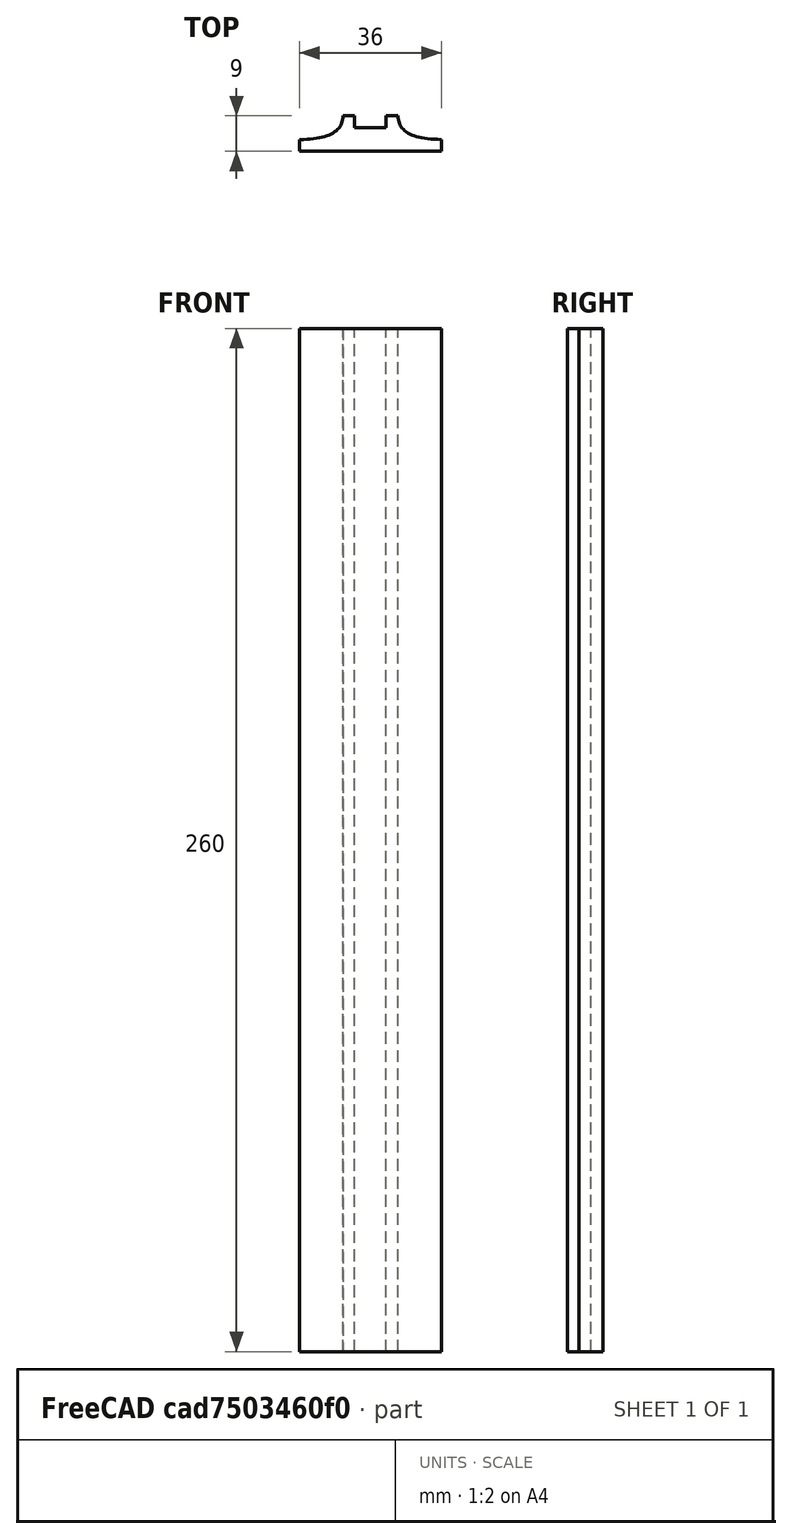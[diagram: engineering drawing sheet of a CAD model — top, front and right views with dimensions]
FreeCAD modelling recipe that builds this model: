
FCSTD DOCUMENT  (FreeCAD 0.19R0.19.2)
Label: laptopStand303.FCStd
License: All rights reserved
LicenseURL: http://en.wikipedia.org/wiki/All_rights_reserved
objects: Sketcher::SketchObject×12, Part::Extrusion×1
note: 13 computed .brp shape members not serialized (recipe doc carries the construction recipe); baked Part::Feature solids carry a one-line shape summary decoded from their .brp

FEATURE [Sketcher::SketchObject] Sketch001  label="legTop"
  FullyConstrained = true
  MapMode = 4
  Placement = pos=(0,0,0) rot=(0.57735,0.57735,0.57735;2.0944rad)
  sketch-geometry (41):
    g0: BSplineCurve PolesCount=3 KnotsCount=2 Degree=2 IsPeriodic=0
    g1: ArcOfCircle CenterX=73.1223 CenterY=-32.291 CenterZ=0 NormalX=0 NormalY=0 NormalZ=1 AngleXU=0 Radius=13 StartAngle=5.92268 EndAngle=9.06428
    g2: ArcOfCircle CenterX=66.7816 CenterY=-49.1439 CenterZ=0 NormalX=0 NormalY=0 NormalZ=1 AngleXU=0 Radius=13 StartAngle=2.78068 EndAngle=5.92131
    g3-g6: Circle x4 (B-spline internal-alignment scaffolding for g7; pole/knot coordinates omitted)
    g7: BSplineCurve PolesCount=4 KnotsCount=2 Degree=3 IsPeriodic=0
    g8: GeomPoint X=28.8094 Y=-19.0875 Z=0
    g9: GeomPoint X=47.0443 Y=-50.4712 Z=0
    g10: Circle CenterX=53.5586 CenterY=-23.2695 CenterZ=0 NormalX=0 NormalY=0 NormalZ=1 AngleXU=0 Radius=3.24518
    g11: LineSegment StartX=17.2232 StartY=-16.0875 StartZ=0 EndX=17.2232 EndY=-19.0875 EndZ=0
    g12: ArcOfCircle CenterX=17.2475 CenterY=-181.166 CenterZ=0 NormalX=0 NormalY=0 NormalZ=1 AngleXU=0 Radius=13 StartAngle=5.92268 EndAngle=7.49361
    g13: ArcOfCircle CenterX=29.5716 CenterY=-148.408 CenterZ=0 NormalX=0 NormalY=0 NormalZ=1 AngleXU=0 Radius=13 StartAngle=4.35228 EndAngle=5.92131
    g14: ArcOfCircle CenterX=35.8967 CenterY=-131.555 CenterZ=0 NormalX=0 NormalY=0 NormalZ=1 AngleXU=0 Radius=13 StartAngle=5.92268 EndAngle=7.49902
    g15: ArcOfCircle CenterX=48.1805 CenterY=-98.7782 CenterZ=0 NormalX=0 NormalY=0 NormalZ=1 AngleXU=0 Radius=13 StartAngle=4.34921 EndAngle=5.92131
    g16: ArcOfCircle CenterX=54.5183 CenterY=-81.9247 CenterZ=0 NormalX=0 NormalY=0 NormalZ=1 AngleXU=0 Radius=13 StartAngle=5.92268 EndAngle=8.70432
    g17: ArcOfCircle CenterX=20.184 CenterY=-217.506 CenterZ=0 NormalX=0 NormalY=0 NormalZ=1 AngleXU=0 Radius=3.81084 StartAngle=1.88136 EndAngle=6.80465
    g18: ArcOfCircle CenterX=36.3663 CenterY=-113.042 CenterZ=0 NormalX=0 NormalY=0 NormalZ=1 AngleXU=0 Radius=3.60555 StartAngle=0.230024 EndAngle=5.3372
    g19: ArcOfCircle CenterX=17.7945 CenterY=-162.686 CenterZ=0 NormalX=0 NormalY=0 NormalZ=1 AngleXU=0 Radius=3.60555 StartAngle=0.230024 EndAngle=5.3372
    g20: ArcOfCircle CenterX=49.8795 CenterY=-62.6074 CenterZ=0 NormalX=0 NormalY=0 NormalZ=1 AngleXU=0 Radius=3.84187 StartAngle=4.46973 EndAngle=9.40343
    g21: LineSegment StartX=48.9563 StartY=-66.3367 StartZ=0 EndX=44.7488 EndY=-73.3482 EndZ=0
    g22: LineSegment StartX=41.085 StartY=-66.3176 StartZ=0 EndX=46.0385 EndY=-62.5254 EndZ=0
    g23: LineSegment StartX=47.0443 StartY=-50.4712 StartZ=0 EndX=41.085 EndY=-66.3176 EndZ=0
    g24: LineSegment StartX=17.2232 StartY=-16.0875 StartZ=0 EndX=117.223 EndY=-16.0875 EndZ=0
    g25: LineSegment StartX=28.8094 StartY=-19.0875 StartZ=0 EndX=17.2232 EndY=-19.0875 EndZ=0
    g26: LineSegment StartX=117.223 StartY=-16.0875 StartZ=0 EndX=117.223 EndY=-19.0875 EndZ=0
    g27: LineSegment StartX=85.2866 StartY=-36.8766 StartZ=0 EndX=78.9396 EndY=-53.7463 EndZ=0
    g28: LineSegment StartX=60.9579 StartY=-27.7053 StartZ=0 EndX=54.6191 EndY=-44.5532 EndZ=0
    g29: LineSegment StartX=23.4884 StartY=-215.608 StartZ=0 EndX=94.6579 EndY=-26.1359 EndZ=0
    g30: LineSegment StartX=19.0195 StartY=-213.878 StartZ=0 EndX=29.4118 EndY=-185.752 EndZ=0
    g31: LineSegment StartX=22.7134 StartY=-166.661 StartZ=0 EndX=21.8316 EndY=-169.001 EndZ=0
    g32: LineSegment StartX=19.9036 StartY=-165.61 StartZ=0 EndX=22.7134 EndY=-166.661 EndZ=0
    g33: LineSegment StartX=21.3051 StartY=-161.864 StartZ=0 EndX=24.1149 EndY=-162.915 EndZ=0
    g34: LineSegment StartX=24.1149 StartY=-162.915 StartZ=0 EndX=24.9906 EndY=-160.574 EndZ=0
    g35: LineSegment StartX=41.7296 StartY=-153.01 StartZ=0 EndX=48.061 EndY=-136.14 EndZ=0
    g36: LineSegment StartX=41.2852 StartY=-117.017 StartZ=0 EndX=40.4148 EndY=-119.365 EndZ=0
    g37: LineSegment StartX=38.4753 StartY=-115.966 StartZ=0 EndX=41.2852 EndY=-117.017 EndZ=0
    g38: LineSegment StartX=39.8769 StartY=-112.22 StartZ=0 EndX=42.6867 EndY=-113.271 EndZ=0
    g39: LineSegment StartX=42.6867 StartY=-113.271 StartZ=0 EndX=43.5622 EndY=-110.93 EndZ=0
    g40: LineSegment StartX=66.6827 StartY=-86.5104 StartZ=0 EndX=60.3386 EndY=-103.381 EndZ=0
  constraints (65):
    c: Block(g0)
    c: Block(g1)
    c: Block(g2)
    c: Weight(g3) = 1
    c: Equal(g3,g4)
    c: Equal(g3,g5)
    c: Equal(g3,g6)
    c: InternalAlignment(g3-g6 -> g7) x4
    c: InternalAlignment(g8,g7)
    c: InternalAlignment(g9,g7)
    c: Block(g10)
    c: Block(g7)
    c: Vertical(g11)
    c: Block(g12)
    c: Block(g13)
    c: Block(g14)
    c: Block(g15)
    c: Block(g16)
    c: Block(g17)
    c: Block(g18)
    c: Block(g19)
    c: Block(g20)
    c: Coincident(g21,g20)
    c: Coincident(g21,g16)
    c: Coincident(g22,g20)
    c: Block(g22)
    c: Coincident(g23,g7)
    c: Coincident(g23,g22)
    c: Coincident(g24,g11)
    c: Horizontal(g24)
    c: Coincident(g25,g7)
    c: Coincident(g25,g11)
    c: Horizontal(g25)
    c: Coincident(g26,g24)
    c: Coincident(g26,g0)
    c: Vertical(g26)
    c: Block(g24)
    c: Coincident(g27,g1)
    c: Coincident(g27,g2)
    c: Coincident(g28,g1)
    c: Coincident(g28,g2)
    c: Coincident(g29,g17)
    c: Coincident(g29,g0)
    c: Coincident(g30,g17)
    c: Coincident(g30,g12)
    c: Coincident(g31,g12)
    c: Coincident(g32,g19)
    c: Coincident(g32,g31)
    c: Block(g31)
    c: Coincident(g33,g19)
    c: Coincident(g34,g33)
    c: Coincident(g34,g13)
    c: Block(g34)
    c: Coincident(g35,g13)
    c: Coincident(g35,g14)
    c: Coincident(g36,g14)
    c: Coincident(g37,g18)
    c: Coincident(g37,g36)
    c: Block(g36)
    c: Coincident(g38,g18)
    c: Coincident(g39,g38)
    c: Coincident(g39,g15)
    c: Block(g39)
    c: Coincident(g40,g16)
    c: Coincident(g40,g15)
FEATURE [Sketcher::SketchObject] Sketch002
  FullyConstrained = true
  sketch-geometry (20):
    g0: LineSegment StartX=-2.77179 StartY=-200.304 StartZ=0 EndX=5.22821 EndY=-200.304 EndZ=0
    g1: LineSegment StartX=5.22821 StartY=-200.304 StartZ=0 EndX=5.22821 EndY=-197.304 EndZ=0
    g2: LineSegment StartX=-2.77179 StartY=-200.304 StartZ=0 EndX=-2.77179 EndY=-197.304 EndZ=0
    g3: LineSegment StartX=5.22821 StartY=-197.304 StartZ=0 EndX=8.22821 EndY=-197.304 EndZ=0
    g4: LineSegment StartX=-2.77179 StartY=-197.304 StartZ=0 EndX=-5.77179 EndY=-197.304 EndZ=0
    g5: LineSegment StartX=19.2282 StartY=-203.304 StartZ=0 EndX=19.2282 EndY=-206.304 EndZ=0
    g6: LineSegment StartX=-16.7718 StartY=-203.304 StartZ=0 EndX=-16.7718 EndY=-206.304 EndZ=0
    g7: LineSegment StartX=-16.7718 StartY=-206.304 StartZ=0 EndX=19.2282 EndY=-206.304 EndZ=0
    g8: Circle CenterX=-16.7718 CenterY=-203.304 CenterZ=0 NormalX=0 NormalY=0 NormalZ=1 AngleXU=0 Radius=1
    g9: Circle CenterX=-5.77179 CenterY=-203.304 CenterZ=0 NormalX=0 NormalY=0 NormalZ=1 AngleXU=0 Radius=1
    g10: Circle CenterX=-5.77179 CenterY=-197.304 CenterZ=0 NormalX=0 NormalY=0 NormalZ=1 AngleXU=0 Radius=1
    g11: BSplineCurve PolesCount=3 KnotsCount=2 Degree=2 IsPeriodic=0
    g12: GeomPoint X=-16.7718 Y=-203.304 Z=0
    g13: GeomPoint X=-5.77179 Y=-197.304 Z=0
    g14: Circle CenterX=19.2282 CenterY=-203.304 CenterZ=0 NormalX=0 NormalY=0 NormalZ=1 AngleXU=0 Radius=1
    g15: Circle CenterX=8.22821 CenterY=-203.304 CenterZ=0 NormalX=0 NormalY=0 NormalZ=1 AngleXU=0 Radius=1
    g16: Circle CenterX=8.22821 CenterY=-197.304 CenterZ=0 NormalX=0 NormalY=0 NormalZ=1 AngleXU=0 Radius=1
    g17: BSplineCurve PolesCount=3 KnotsCount=2 Degree=2 IsPeriodic=0
    g18: GeomPoint X=19.2282 Y=-203.304 Z=0
    g19: GeomPoint X=8.22821 Y=-197.304 Z=0
  constraints (41):
    c: Horizontal(g0)
    c: Distance(g0) = 8
    c: Coincident(g1,g0)
    c: Vertical(g1)
    c: Distance(g1) = 3
    c: Coincident(g2,g0)
    c: Vertical(g2)
    c: Distance(g2) = 3
    c: Coincident(g3,g1)
    c: Horizontal(g3)
    c: Distance(g3) = 3
    c: Coincident(g4,g2)
    c: Horizontal(g4)
    c: Distance(g4) = 3
    c: Vertical(g5)
    c: Vertical(g6)
    c: Coincident(g7,g6)
    c: Coincident(g7,g5)
    c: Weight(g8) = 1
    c: Equal(g8,g9)
    c: Equal(g8,g10)
    c: Coincident(g11,g4)
    c: InternalAlignment(g8,g11)
    c: InternalAlignment(g9,g11)
    c: InternalAlignment(g10,g11)
    c: InternalAlignment(g12,g11)
    c: InternalAlignment(g13,g11)
    c: Coincident(g17,g5)
    c: Weight(g14) = 1
    c: Equal(g14,g15)
    c: Equal(g14,g16)
    c: Coincident(g17,g3)
    c: InternalAlignment(g14,g17)
    c: InternalAlignment(g15,g17)
    c: InternalAlignment(g16,g17)
    c: InternalAlignment(g18,g17)
    c: InternalAlignment(g19,g17)
    c: Block(g7)
    c: Block(g17)
    c: Block(g11)
    c: Block(g6)
FEATURE [Part::Extrusion] Extrude003
  Base = -> Sketch002
  Dir = (0,0,1)
  DirMode = 2
  FaceMakerClass = Part::FaceMakerBullseye
  LengthFwd = 260
  LengthRev = 0
  Solid = true
  Symmetric = false
FEATURE [Sketcher::SketchObject] Sketch003  label="original"
  FullyConstrained = false
  sketch-geometry (469):
    g0: LineSegment StartX=-42.9272 StartY=136.221 StartZ=0 EndX=-42.9272 EndY=-103.779 EndZ=0
    g1: LineSegment StartX=407.073 StartY=136.221 StartZ=0 EndX=407.073 EndY=-103.779 EndZ=0
    g2: ArcOfCircle CenterX=-26.9272 CenterY=-83.7794 CenterZ=0 NormalX=0 NormalY=0 NormalZ=1 AngleXU=0 Radius=8 StartAngle=3.14159 EndAngle=6.28319
    g3: ArcOfCircle CenterX=391.073 CenterY=-83.7794 CenterZ=0 NormalX=0 NormalY=0 NormalZ=1 AngleXU=0 Radius=8 StartAngle=3.14159 EndAngle=6.28319
    g4: Circle CenterX=175.022 CenterY=27.0628 CenterZ=0 NormalX=0 NormalY=0 NormalZ=1 AngleXU=0 Radius=1
    g5: Circle CenterX=179.022 CenterY=24.8665 CenterZ=0 NormalX=0 NormalY=0 NormalZ=1 AngleXU=0 Radius=1
    g6: Circle CenterX=179.022 CenterY=27.0628 CenterZ=0 NormalX=0 NormalY=0 NormalZ=1 AngleXU=0 Radius=1
    g7: BSplineCurve PolesCount=3 KnotsCount=2 Degree=2 IsPeriodic=0
    g8: GeomPoint X=175.022 Y=27.0628 Z=0
    g9: GeomPoint X=179.022 Y=27.0628 Z=0
    g10: Circle CenterX=189.124 CenterY=27.0628 CenterZ=0 NormalX=0 NormalY=0 NormalZ=1 AngleXU=0 Radius=1
    g11: Circle CenterX=185.124 CenterY=24.8665 CenterZ=0 NormalX=0 NormalY=0 NormalZ=1 AngleXU=0 Radius=1
    g12: Circle CenterX=185.124 CenterY=27.0628 CenterZ=0 NormalX=0 NormalY=0 NormalZ=1 AngleXU=0 Radius=1
    g13: BSplineCurve PolesCount=3 KnotsCount=2 Degree=2 IsPeriodic=0
    g14: GeomPoint X=189.124 Y=27.0628 Z=0
    g15: GeomPoint X=185.124 Y=27.0628 Z=0
    g16: Circle CenterX=175.022 CenterY=5.37834 CenterZ=0 NormalX=0 NormalY=0 NormalZ=1 AngleXU=0 Radius=1
    g17: Circle CenterX=179.022 CenterY=7.57463 CenterZ=0 NormalX=0 NormalY=0 NormalZ=1 AngleXU=0 Radius=1
    g18: Circle CenterX=179.022 CenterY=5.34704 CenterZ=0 NormalX=0 NormalY=0 NormalZ=1 AngleXU=0 Radius=1
    g19: BSplineCurve PolesCount=3 KnotsCount=2 Degree=2 IsPeriodic=0
    g20: GeomPoint X=175.022 Y=5.37834 Z=0
    g21: GeomPoint X=179.022 Y=5.34704 Z=0
    g22: Circle CenterX=189.124 CenterY=5.37834 CenterZ=0 NormalX=0 NormalY=0 NormalZ=1 AngleXU=0 Radius=1
    g23: Circle CenterX=185.124 CenterY=7.57463 CenterZ=0 NormalX=0 NormalY=0 NormalZ=1 AngleXU=0 Radius=1
    g24: Circle CenterX=185.124 CenterY=5.34704 CenterZ=0 NormalX=0 NormalY=0 NormalZ=1 AngleXU=0 Radius=1
    g25: BSplineCurve PolesCount=3 KnotsCount=2 Degree=2 IsPeriodic=0
    g26: GeomPoint X=189.124 Y=5.37834 Z=0
    g27: GeomPoint X=185.124 Y=5.34704 Z=0
    g28: Circle CenterX=165.871 CenterY=18.1458 CenterZ=0 NormalX=0 NormalY=0 NormalZ=1 AngleXU=0 Radius=1
    g29: Circle CenterX=169.377 CenterY=16.2206 CenterZ=0 NormalX=0 NormalY=0 NormalZ=1 AngleXU=0 Radius=1
    g30: Circle CenterX=165.871 CenterY=14.2956 CenterZ=0 NormalX=0 NormalY=0 NormalZ=1 AngleXU=0 Radius=1
    g31: BSplineCurve PolesCount=3 KnotsCount=2 Degree=2 IsPeriodic=0
    g32: GeomPoint X=165.871 Y=18.1458 Z=0
    g33: GeomPoint X=165.871 Y=14.2956 Z=0
    g34: Circle CenterX=198.275 CenterY=18.1318 CenterZ=0 NormalX=0 NormalY=0 NormalZ=1 AngleXU=0 Radius=1
    g35: Circle CenterX=194.768 CenterY=16.2206 CenterZ=0 NormalX=0 NormalY=0 NormalZ=1 AngleXU=0 Radius=1
    g36: Circle CenterX=198.264 CenterY=14.2963 CenterZ=0 NormalX=0 NormalY=0 NormalZ=1 AngleXU=0 Radius=1
    g37: BSplineCurve PolesCount=3 KnotsCount=2 Degree=2 IsPeriodic=0
    g38: GeomPoint X=198.275 Y=18.1318 Z=0
    g39: GeomPoint X=198.264 Y=14.2963 Z=0
    g40: LineSegment StartX=407.073 StartY=-103.779 StartZ=0 EndX=-42.9272 EndY=-103.779 EndZ=0
    g41: Circle CenterX=125.607 CenterY=54.1951 CenterZ=0 NormalX=0 NormalY=0 NormalZ=1 AngleXU=0 Radius=1
    g42: Circle CenterX=139.632 CenterY=46.4944 CenterZ=0 NormalX=0 NormalY=0 NormalZ=1 AngleXU=0 Radius=1
    g43: Circle CenterX=127.326 CenterY=56.7187 CenterZ=0 NormalX=0 NormalY=0 NormalZ=1 AngleXU=0 Radius=1
    g44: BSplineCurve PolesCount=3 KnotsCount=2 Degree=2 IsPeriodic=0
    g45: GeomPoint X=125.607 Y=54.1951 Z=0
    g46: GeomPoint X=127.326 Y=56.7187 Z=0
    g47: Circle CenterX=236.824 CenterY=56.7187 CenterZ=0 NormalX=0 NormalY=0 NormalZ=1 AngleXU=0 Radius=1
    g48: Circle CenterX=224.513 CenterY=46.4944 CenterZ=0 NormalX=0 NormalY=0 NormalZ=1 AngleXU=0 Radius=1
    g49: Circle CenterX=238.538 CenterY=54.1951 CenterZ=0 NormalX=0 NormalY=0 NormalZ=1 AngleXU=0 Radius=1
    g50: BSplineCurve PolesCount=3 KnotsCount=2 Degree=2 IsPeriodic=0
    g51: GeomPoint X=236.824 Y=56.7187 Z=0
    g52: GeomPoint X=238.538 Y=54.1951 Z=0
    g53: Circle CenterX=238.538 CenterY=-21.7516 CenterZ=0 NormalX=0 NormalY=0 NormalZ=1 AngleXU=0 Radius=1
    g54: Circle CenterX=224.513 CenterY=-14.0532 CenterZ=0 NormalX=0 NormalY=0 NormalZ=1 AngleXU=0 Radius=1
    g55: Circle CenterX=236.584 CenterY=-24.2775 CenterZ=0 NormalX=0 NormalY=0 NormalZ=1 AngleXU=0 Radius=1
    g56: BSplineCurve PolesCount=3 KnotsCount=2 Degree=2 IsPeriodic=0
    g57: GeomPoint X=238.538 Y=-21.7516 Z=0
    g58: GeomPoint X=236.584 Y=-24.2775 Z=0
    g59: Circle CenterX=125.607 CenterY=-21.7539 CenterZ=0 NormalX=0 NormalY=0 NormalZ=1 AngleXU=0 Radius=1
    g60: Circle CenterX=139.632 CenterY=-14.0532 CenterZ=0 NormalX=0 NormalY=0 NormalZ=1 AngleXU=0 Radius=1
    g61: Circle CenterX=127.325 CenterY=-24.2775 CenterZ=0 NormalX=0 NormalY=0 NormalZ=1 AngleXU=0 Radius=1
    g62: BSplineCurve PolesCount=3 KnotsCount=2 Degree=2 IsPeriodic=0
    g63: GeomPoint X=125.607 Y=-21.7539 Z=0
    g64: GeomPoint X=127.325 Y=-24.2775 Z=0
    g65: Circle CenterX=302.996 CenterY=111.695 CenterZ=0 NormalX=0 NormalY=0 NormalZ=1 AngleXU=0 Radius=1
    g66: Circle CenterX=306.073 CenterY=114.251 CenterZ=0 NormalX=0 NormalY=0 NormalZ=1 AngleXU=0 Radius=1
    g67: Circle CenterX=306.073 CenterY=110.251 CenterZ=0 NormalX=0 NormalY=0 NormalZ=1 AngleXU=0 Radius=1
    g68: BSplineCurve PolesCount=3 KnotsCount=2 Degree=2 IsPeriodic=0
    g69: GeomPoint X=302.996 Y=111.695 Z=0
    g70: GeomPoint X=306.073 Y=110.251 Z=0
    g71: Circle CenterX=306.073 CenterY=95.2763 CenterZ=0 NormalX=0 NormalY=0 NormalZ=1 AngleXU=0 Radius=1
    g72: Circle CenterX=306.073 CenterY=91.2763 CenterZ=0 NormalX=0 NormalY=0 NormalZ=1 AngleXU=0 Radius=1
    g73: Circle CenterX=302.567 CenterY=89.3511 CenterZ=0 NormalX=0 NormalY=0 NormalZ=1 AngleXU=0 Radius=1
    g74: BSplineCurve PolesCount=3 KnotsCount=2 Degree=2 IsPeriodic=0
    g75: GeomPoint X=306.073 Y=95.2763 Z=0
    g76: GeomPoint X=302.567 Y=89.3511 Z=0
    g77: LineSegment StartX=306.073 StartY=110.251 StartZ=0 EndX=306.073 EndY=95.2763 EndZ=0
    g78: LineSegment StartX=302.996 StartY=111.695 StartZ=0 EndX=236.824 EndY=56.7187 EndZ=0
    g79: LineSegment StartX=238.538 StartY=54.1951 StartZ=0 EndX=302.567 EndY=89.3511 EndZ=0
    g80: Circle CenterX=61.1496 CenterY=111.695 CenterZ=0 NormalX=0 NormalY=0 NormalZ=1 AngleXU=0 Radius=1
    g81: Circle CenterX=58.0728 CenterY=114.251 CenterZ=0 NormalX=0 NormalY=0 NormalZ=1 AngleXU=0 Radius=1
    g82: Circle CenterX=58.0728 CenterY=110.251 CenterZ=0 NormalX=0 NormalY=0 NormalZ=1 AngleXU=0 Radius=1
    g83: BSplineCurve PolesCount=3 KnotsCount=2 Degree=2 IsPeriodic=0
    g84: GeomPoint X=61.1496 Y=111.695 Z=0
    g85: GeomPoint X=58.0728 Y=110.251 Z=0
    g86: Circle CenterX=61.5791 CenterY=89.3511 CenterZ=0 NormalX=0 NormalY=0 NormalZ=1 AngleXU=0 Radius=1
    g87: Circle CenterX=58.0728 CenterY=91.2763 CenterZ=0 NormalX=0 NormalY=0 NormalZ=1 AngleXU=0 Radius=1
    g88: Circle CenterX=58.0728 CenterY=95.2763 CenterZ=0 NormalX=0 NormalY=0 NormalZ=1 AngleXU=0 Radius=1
    g89: BSplineCurve PolesCount=3 KnotsCount=2 Degree=2 IsPeriodic=0
    g90: GeomPoint X=61.5791 Y=89.3511 Z=0
    g91: GeomPoint X=58.0728 Y=95.2763 Z=0
    g92: LineSegment StartX=58.0728 StartY=110.251 StartZ=0 EndX=58.0728 EndY=95.2763 EndZ=0
    g93: LineSegment StartX=61.1496 StartY=111.695 StartZ=0 EndX=127.326 EndY=56.7187 EndZ=0
    g94: LineSegment StartX=125.607 StartY=54.1951 StartZ=0 EndX=61.5791 EndY=89.3511 EndZ=0
    g95: Circle CenterX=61.5791 CenterY=-56.9099 CenterZ=0 NormalX=0 NormalY=0 NormalZ=1 AngleXU=0 Radius=1
    g96: Circle CenterX=58.0728 CenterY=-58.8351 CenterZ=0 NormalX=0 NormalY=0 NormalZ=1 AngleXU=0 Radius=1
    g97: Circle CenterX=58.0728 CenterY=-62.8351 CenterZ=0 NormalX=0 NormalY=0 NormalZ=1 AngleXU=0 Radius=1
    g98: BSplineCurve PolesCount=3 KnotsCount=2 Degree=2 IsPeriodic=0
    g99: GeomPoint X=61.5791 Y=-56.9099 Z=0
    g100: GeomPoint X=58.0728 Y=-62.8351 Z=0
    g101: Circle CenterX=58.0728 CenterY=-77.8102 CenterZ=0 NormalX=0 NormalY=0 NormalZ=1 AngleXU=0 Radius=1
    g102: Circle CenterX=58.0728 CenterY=-81.8102 CenterZ=0 NormalX=0 NormalY=0 NormalZ=1 AngleXU=0 Radius=1
    g103: Circle CenterX=61.1496 CenterY=-79.2541 CenterZ=0 NormalX=0 NormalY=0 NormalZ=1 AngleXU=0 Radius=1
    g104: BSplineCurve PolesCount=3 KnotsCount=2 Degree=2 IsPeriodic=0
    g105: GeomPoint X=58.0728 Y=-77.8102 Z=0
    g106: GeomPoint X=61.1496 Y=-79.2541 Z=0
    g107: LineSegment StartX=58.0728 StartY=-62.8351 StartZ=0 EndX=58.0728 EndY=-77.8102 EndZ=0
    g108: LineSegment StartX=61.1496 StartY=-79.2541 StartZ=0 EndX=127.325 EndY=-24.2775 EndZ=0
    g109: LineSegment StartX=125.607 StartY=-21.7539 StartZ=0 EndX=61.5791 EndY=-56.9099 EndZ=0
    g110: Circle CenterX=302.567 CenterY=-56.9099 CenterZ=0 NormalX=0 NormalY=0 NormalZ=1 AngleXU=0 Radius=1
    g111: Circle CenterX=306.073 CenterY=-58.8351 CenterZ=0 NormalX=0 NormalY=0 NormalZ=1 AngleXU=0 Radius=1
    g112: Circle CenterX=306.073 CenterY=-62.8351 CenterZ=0 NormalX=0 NormalY=0 NormalZ=1 AngleXU=0 Radius=1
    g113: BSplineCurve PolesCount=3 KnotsCount=2 Degree=2 IsPeriodic=0
    g114: GeomPoint X=302.567 Y=-56.9099 Z=0
    g115: GeomPoint X=306.073 Y=-62.8351 Z=0
    g116: Circle CenterX=302.996 CenterY=-79.2541 CenterZ=0 NormalX=0 NormalY=0 NormalZ=1 AngleXU=0 Radius=1
    g117: Circle CenterX=306.073 CenterY=-81.8102 CenterZ=0 NormalX=0 NormalY=0 NormalZ=1 AngleXU=0 Radius=1
    g118: Circle CenterX=306.073 CenterY=-77.8102 CenterZ=0 NormalX=0 NormalY=0 NormalZ=1 AngleXU=0 Radius=1
    g119: BSplineCurve PolesCount=3 KnotsCount=2 Degree=2 IsPeriodic=0
    g120: GeomPoint X=302.996 Y=-79.2541 Z=0
    g121: GeomPoint X=306.073 Y=-77.8102 Z=0
    g122: LineSegment StartX=306.073 StartY=-62.8351 StartZ=0 EndX=306.073 EndY=-77.8102 EndZ=0
    g123: LineSegment StartX=302.996 StartY=-79.2541 StartZ=0 EndX=236.584 EndY=-24.2775 EndZ=0
    g124: LineSegment StartX=238.538 StartY=-21.7516 StartZ=0 EndX=302.567 EndY=-56.9099 EndZ=0
    g125: Circle CenterX=61.6457 CenterY=-88.8112 CenterZ=0 NormalX=0 NormalY=0 NormalZ=1 AngleXU=0 Radius=1
    g126: Circle CenterX=58.0728 CenterY=-91.7794 CenterZ=0 NormalX=0 NormalY=0 NormalZ=1 AngleXU=0 Radius=1
    g127: Circle CenterX=63.9135 CenterY=-91.7791 CenterZ=0 NormalX=0 NormalY=0 NormalZ=1 AngleXU=0 Radius=1
    g128: BSplineCurve PolesCount=3 KnotsCount=2 Degree=2 IsPeriodic=0
    g129: GeomPoint X=61.6457 Y=-88.8112 Z=0
    g130: GeomPoint X=63.9135 Y=-91.7791 Z=0
    g131: Circle CenterX=179.022 CenterY=-85.8163 CenterZ=0 NormalX=0 NormalY=0 NormalZ=1 AngleXU=0 Radius=1
    g132: Circle CenterX=179.022 CenterY=-91.7794 CenterZ=0 NormalX=0 NormalY=0 NormalZ=1 AngleXU=0 Radius=1
    g133: Circle CenterX=171.895 CenterY=-91.7791 CenterZ=0 NormalX=0 NormalY=0 NormalZ=1 AngleXU=0 Radius=1
    g134: BSplineCurve PolesCount=3 KnotsCount=2 Degree=2 IsPeriodic=0
    g135: GeomPoint X=179.022 Y=-85.8163 Z=0
    g136: GeomPoint X=171.895 Y=-91.7791 Z=0
    g137: Circle CenterX=185.124 CenterY=-86.2028 CenterZ=0 NormalX=0 NormalY=0 NormalZ=1 AngleXU=0 Radius=1
    g138: Circle CenterX=185.124 CenterY=-91.7794 CenterZ=0 NormalX=0 NormalY=0 NormalZ=1 AngleXU=0 Radius=1
    g139: Circle CenterX=191.747 CenterY=-91.7794 CenterZ=0 NormalX=0 NormalY=0 NormalZ=1 AngleXU=0 Radius=1
    g140: BSplineCurve PolesCount=3 KnotsCount=2 Degree=2 IsPeriodic=0
    g141: GeomPoint X=185.124 Y=-86.2028 Z=0
    g142: GeomPoint X=191.747 Y=-91.7794 Z=0
    g143: Circle CenterX=299.888 CenterY=-86.6413 CenterZ=0 NormalX=0 NormalY=0 NormalZ=1 AngleXU=0 Radius=1
    g144: Circle CenterX=306.073 CenterY=-91.7794 CenterZ=0 NormalX=0 NormalY=0 NormalZ=1 AngleXU=0 Radius=1
    g145: Circle CenterX=298.776 CenterY=-91.7794 CenterZ=0 NormalX=0 NormalY=0 NormalZ=1 AngleXU=0 Radius=1
    g146: BSplineCurve PolesCount=3 KnotsCount=2 Degree=2 IsPeriodic=0
    g147: GeomPoint X=299.888 Y=-86.6413 Z=0
    g148: GeomPoint X=298.776 Y=-91.7794 Z=0
    g149: LineSegment StartX=189.124 StartY=5.37834 StartZ=0 EndX=299.888 EndY=-86.6413 EndZ=0
    g150: LineSegment StartX=298.776 StartY=-91.7794 StartZ=0 EndX=191.747 EndY=-91.7794 EndZ=0
    g151: LineSegment StartX=185.124 StartY=-86.2028 StartZ=0 EndX=185.124 EndY=5.34704 EndZ=0
    g152: LineSegment StartX=179.022 StartY=5.34704 StartZ=0 EndX=179.022 EndY=-85.8163 EndZ=0
    g153: LineSegment StartX=171.895 StartY=-91.7791 StartZ=0 EndX=63.9135 EndY=-91.7791 EndZ=0
    g154: LineSegment StartX=61.6457 StartY=-88.8112 StartZ=0 EndX=175.022 EndY=5.37834 EndZ=0
    g155: Circle CenterX=302.073 CenterY=124.221 CenterZ=0 NormalX=0 NormalY=0 NormalZ=1 AngleXU=0 Radius=1
    g156: Circle CenterX=306.073 CenterY=124.221 CenterZ=0 NormalX=0 NormalY=0 NormalZ=1 AngleXU=0 Radius=1
    g157: Circle CenterX=302.996 CenterY=121.665 CenterZ=0 NormalX=0 NormalY=0 NormalZ=1 AngleXU=0 Radius=1
    g158: BSplineCurve PolesCount=3 KnotsCount=2 Degree=2 IsPeriodic=0
    g159: GeomPoint X=302.073 Y=124.221 Z=0
    g160: GeomPoint X=302.996 Y=121.665 Z=0
    g161: Circle CenterX=189.124 CenterY=124.221 CenterZ=0 NormalX=0 NormalY=0 NormalZ=1 AngleXU=0 Radius=1
    g162: Circle CenterX=185.124 CenterY=124.221 CenterZ=0 NormalX=0 NormalY=0 NormalZ=1 AngleXU=0 Radius=1
    g163: Circle CenterX=185.124 CenterY=120.221 CenterZ=0 NormalX=0 NormalY=0 NormalZ=1 AngleXU=0 Radius=1
    g164: BSplineCurve PolesCount=3 KnotsCount=2 Degree=2 IsPeriodic=0
    g165: GeomPoint X=189.124 Y=124.221 Z=0
    g166: GeomPoint X=185.124 Y=120.221 Z=0
    g167: Circle CenterX=175.022 CenterY=124.221 CenterZ=0 NormalX=0 NormalY=0 NormalZ=1 AngleXU=0 Radius=1
    g168: Circle CenterX=179.022 CenterY=124.221 CenterZ=0 NormalX=0 NormalY=0 NormalZ=1 AngleXU=0 Radius=1
    g169: Circle CenterX=179.022 CenterY=120.221 CenterZ=0 NormalX=0 NormalY=0 NormalZ=1 AngleXU=0 Radius=1
    g170: BSplineCurve PolesCount=3 KnotsCount=2 Degree=2 IsPeriodic=0
    g171: GeomPoint X=175.022 Y=124.221 Z=0
    g172: GeomPoint X=179.022 Y=120.221 Z=0
    g173: Circle CenterX=62.0728 CenterY=124.221 CenterZ=0 NormalX=0 NormalY=0 NormalZ=1 AngleXU=0 Radius=1
    g174: Circle CenterX=58.0728 CenterY=124.221 CenterZ=0 NormalX=0 NormalY=0 NormalZ=1 AngleXU=0 Radius=1
    g175: Circle CenterX=61.1496 CenterY=121.665 CenterZ=0 NormalX=0 NormalY=0 NormalZ=1 AngleXU=0 Radius=1
    g176: BSplineCurve PolesCount=3 KnotsCount=2 Degree=2 IsPeriodic=0
    g177: GeomPoint X=62.0728 Y=124.221 Z=0
    g178: GeomPoint X=61.1496 Y=121.665 Z=0
    g179: LineSegment StartX=179.022 StartY=120.221 StartZ=0 EndX=179.022 EndY=27.0628 EndZ=0
    g180: LineSegment StartX=185.124 StartY=27.0628 StartZ=0 EndX=185.124 EndY=120.221 EndZ=0
    g181: LineSegment StartX=302.996 StartY=121.665 StartZ=0 EndX=189.124 EndY=27.0628 EndZ=0
    g182: LineSegment StartX=175.022 StartY=27.0628 StartZ=0 EndX=61.1496 EndY=121.665 EndZ=0
    g183: Circle CenterX=61.5791 CenterY=75.4095 CenterZ=0 NormalX=0 NormalY=0 NormalZ=1 AngleXU=0 Radius=1
    g184: Circle CenterX=58.0728 CenterY=77.3346 CenterZ=0 NormalX=0 NormalY=0 NormalZ=1 AngleXU=0 Radius=1
    g185: Circle CenterX=58.0728 CenterY=73.3346 CenterZ=0 NormalX=0 NormalY=0 NormalZ=1 AngleXU=0 Radius=1
    g186: BSplineCurve PolesCount=3 KnotsCount=2 Degree=2 IsPeriodic=0
    g187: GeomPoint X=61.5791 Y=75.4095 Z=0
    g188: GeomPoint X=58.0728 Y=73.3346 Z=0
    g189: Circle CenterX=58.0728 CenterY=-40.8935 CenterZ=0 NormalX=0 NormalY=0 NormalZ=1 AngleXU=0 Radius=1
    g190: Circle CenterX=58.0728 CenterY=-44.8935 CenterZ=0 NormalX=0 NormalY=0 NormalZ=1 AngleXU=0 Radius=1
    g191: Circle CenterX=61.5791 CenterY=-42.9683 CenterZ=0 NormalX=0 NormalY=0 NormalZ=1 AngleXU=0 Radius=1
    g192: BSplineCurve PolesCount=3 KnotsCount=2 Degree=2 IsPeriodic=0
    g193: GeomPoint X=58.0728 Y=-40.8935 Z=0
    g194: GeomPoint X=61.5791 Y=-42.9683 Z=0
    g195: LineSegment StartX=61.5791 StartY=-42.9683 StartZ=0 EndX=165.871 EndY=14.2956 EndZ=0
    g196: LineSegment StartX=165.871 StartY=18.1458 StartZ=0 EndX=61.5791 EndY=75.4095 EndZ=0
    g197: LineSegment StartX=58.0728 StartY=73.3346 StartZ=0 EndX=58.0728 EndY=-40.8935 EndZ=0
    g198: Circle CenterX=302.567 CenterY=-42.9683 CenterZ=0 NormalX=0 NormalY=0 NormalZ=1 AngleXU=0 Radius=1
    g199: Circle CenterX=306.073 CenterY=-44.8935 CenterZ=0 NormalX=0 NormalY=0 NormalZ=1 AngleXU=0 Radius=1
    g200: Circle CenterX=306.073 CenterY=-40.8935 CenterZ=0 NormalX=0 NormalY=0 NormalZ=1 AngleXU=0 Radius=1
    g201: BSplineCurve PolesCount=3 KnotsCount=2 Degree=2 IsPeriodic=0
    g202: GeomPoint X=302.567 Y=-42.9683 Z=0
    g203: GeomPoint X=306.073 Y=-40.8935 Z=0
    g204: Circle CenterX=306.073 CenterY=73.3346 CenterZ=0 NormalX=0 NormalY=0 NormalZ=1 AngleXU=0 Radius=1
    g205: Circle CenterX=306.073 CenterY=77.3346 CenterZ=0 NormalX=0 NormalY=0 NormalZ=1 AngleXU=0 Radius=1
    g206: Circle CenterX=302.535 CenterY=75.4095 CenterZ=0 NormalX=0 NormalY=0 NormalZ=1 AngleXU=0 Radius=1
    g207: BSplineCurve PolesCount=3 KnotsCount=2 Degree=2 IsPeriodic=0
    g208: GeomPoint X=306.073 Y=73.3346 Z=0
    g209: GeomPoint X=302.535 Y=75.4095 Z=0
    g210: LineSegment StartX=302.567 StartY=-42.9683 StartZ=0 EndX=198.264 EndY=14.2963 EndZ=0
    g211: LineSegment StartX=198.275 StartY=18.1318 StartZ=0 EndX=302.535 EndY=75.4095 EndZ=0
    g212: LineSegment StartX=306.073 StartY=73.3346 StartZ=0 EndX=306.073 EndY=-40.8935 EndZ=0
    g213: LineSegment StartX=322.073 StartY=105.865 StartZ=0 EndX=328.643 EndY=105.865 EndZ=0
    g214: LineSegment StartX=318.073 StartY=120.221 StartZ=0 EndX=318.073 EndY=109.865 EndZ=0
    g215: LineSegment StartX=336.157 StartY=107.779 StartZ=0 EndX=362.567 EndY=122.294 EndZ=0
    g216: Circle CenterX=362.073 CenterY=124.221 CenterZ=0 NormalX=0 NormalY=0 NormalZ=1 AngleXU=0 Radius=1
    g217: Circle CenterX=366.073 CenterY=124.221 CenterZ=0 NormalX=0 NormalY=0 NormalZ=1 AngleXU=0 Radius=1
    g218: Circle CenterX=362.567 CenterY=122.294 CenterZ=0 NormalX=0 NormalY=0 NormalZ=1 AngleXU=0 Radius=1
    g219: BSplineCurve PolesCount=3 KnotsCount=2 Degree=2 IsPeriodic=0
    g220: GeomPoint X=362.073 Y=124.221 Z=0
    g221: GeomPoint X=362.567 Y=122.294 Z=0
    g222: Circle CenterX=322.073 CenterY=124.221 CenterZ=0 NormalX=0 NormalY=0 NormalZ=1 AngleXU=0 Radius=1
    g223: Circle CenterX=318.073 CenterY=124.221 CenterZ=0 NormalX=0 NormalY=0 NormalZ=1 AngleXU=0 Radius=1
    g224: Circle CenterX=318.073 CenterY=120.221 CenterZ=0 NormalX=0 NormalY=0 NormalZ=1 AngleXU=0 Radius=1
    g225: BSplineCurve PolesCount=3 KnotsCount=2 Degree=2 IsPeriodic=0
    g226: GeomPoint X=322.073 Y=124.221 Z=0
    g227: GeomPoint X=318.073 Y=120.221 Z=0
    g228: Circle CenterX=322.073 CenterY=105.865 CenterZ=0 NormalX=0 NormalY=0 NormalZ=1 AngleXU=0 Radius=1
    g229: Circle CenterX=318.073 CenterY=105.865 CenterZ=0 NormalX=0 NormalY=0 NormalZ=1 AngleXU=0 Radius=1
    g230: Circle CenterX=318.073 CenterY=109.865 CenterZ=0 NormalX=0 NormalY=0 NormalZ=1 AngleXU=0 Radius=1
    g231: BSplineCurve PolesCount=3 KnotsCount=2 Degree=2 IsPeriodic=0
    g232: GeomPoint X=322.073 Y=105.865 Z=0
    g233: GeomPoint X=318.073 Y=109.865 Z=0
    g234: Circle CenterX=336.157 CenterY=107.779 CenterZ=0 NormalX=0 NormalY=0 NormalZ=1 AngleXU=0 Radius=1
    g235: Circle CenterX=332.651 CenterY=105.853 CenterZ=0 NormalX=0 NormalY=0 NormalZ=1 AngleXU=0 Radius=1
    g236: Circle CenterX=328.643 CenterY=105.865 CenterZ=0 NormalX=0 NormalY=0 NormalZ=1 AngleXU=0 Radius=1
    g237: BSplineCurve PolesCount=3 KnotsCount=2 Degree=2 IsPeriodic=0
    g238: GeomPoint X=336.157 Y=107.779 Z=0
    g239: GeomPoint X=328.643 Y=105.865 Z=0
    g240: LineSegment StartX=322.073 StartY=124.221 StartZ=0 EndX=362.073 EndY=124.221 EndZ=0
    g241: Circle CenterX=371.567 CenterY=-80.8644 CenterZ=0 NormalX=0 NormalY=0 NormalZ=1 AngleXU=0 Radius=1
    g242: Circle CenterX=375.073 CenterY=-82.7896 CenterZ=0 NormalX=0 NormalY=0 NormalZ=1 AngleXU=0 Radius=1
    g243: Circle CenterX=375.073 CenterY=-78.7896 CenterZ=0 NormalX=0 NormalY=0 NormalZ=1 AngleXU=0 Radius=1
    g244: BSplineCurve PolesCount=3 KnotsCount=2 Degree=2 IsPeriodic=0
    g245: GeomPoint X=371.567 Y=-80.8644 Z=0
    g246: GeomPoint X=375.073 Y=-78.7896 Z=0
    g247: Circle CenterX=321.579 CenterY=-53.4075 CenterZ=0 NormalX=0 NormalY=0 NormalZ=1 AngleXU=0 Radius=1
    g248: Circle CenterX=318.073 CenterY=-51.4823 CenterZ=0 NormalX=0 NormalY=0 NormalZ=1 AngleXU=0 Radius=1
    g249: Circle CenterX=318.073 CenterY=-47.4805 CenterZ=0 NormalX=0 NormalY=0 NormalZ=1 AngleXU=0 Radius=1
    g250: BSplineCurve PolesCount=3 KnotsCount=2 Degree=2 IsPeriodic=0
    g251: GeomPoint X=321.579 Y=-53.4075 Z=0
    g252: GeomPoint X=318.073 Y=-47.4805 Z=0
    g253: LineSegment StartX=371.567 StartY=-80.8644 StartZ=0 EndX=321.579 EndY=-53.4075 EndZ=0
    g254: Circle CenterX=321.579 CenterY=-67.3492 CenterZ=0 NormalX=0 NormalY=0 NormalZ=1 AngleXU=0 Radius=1
    g255: Circle CenterX=318.073 CenterY=-65.424 CenterZ=0 NormalX=0 NormalY=0 NormalZ=1 AngleXU=0 Radius=1
    g256: Circle CenterX=318.073 CenterY=-69.424 CenterZ=0 NormalX=0 NormalY=0 NormalZ=1 AngleXU=0 Radius=1
    g257: BSplineCurve PolesCount=3 KnotsCount=2 Degree=2 IsPeriodic=0
    g258: GeomPoint X=321.579 Y=-67.3492 Z=0
    g259: GeomPoint X=318.073 Y=-69.424 Z=0
    g260: Circle CenterX=362.567 CenterY=-89.8542 CenterZ=0 NormalX=0 NormalY=0 NormalZ=1 AngleXU=0 Radius=1
    g261: Circle CenterX=366.073 CenterY=-91.7794 CenterZ=0 NormalX=0 NormalY=0 NormalZ=1 AngleXU=0 Radius=1
    g262: Circle CenterX=362.073 CenterY=-91.7794 CenterZ=0 NormalX=0 NormalY=0 NormalZ=1 AngleXU=0 Radius=1
    g263: BSplineCurve PolesCount=3 KnotsCount=2 Degree=2 IsPeriodic=0
    g264: GeomPoint X=362.567 Y=-89.8542 Z=0
    g265: GeomPoint X=362.073 Y=-91.7794 Z=0
    g266: Circle CenterX=322.073 CenterY=-91.7794 CenterZ=0 NormalX=0 NormalY=0 NormalZ=1 AngleXU=0 Radius=1
    g267: Circle CenterX=318.073 CenterY=-91.7794 CenterZ=0 NormalX=0 NormalY=0 NormalZ=1 AngleXU=0 Radius=1
    g268: Circle CenterX=318.073 CenterY=-87.7794 CenterZ=0 NormalX=0 NormalY=0 NormalZ=1 AngleXU=0 Radius=1
    g269: BSplineCurve PolesCount=3 KnotsCount=2 Degree=2 IsPeriodic=0
    g270: GeomPoint X=322.073 Y=-91.7794 Z=0
    g271: GeomPoint X=318.073 Y=-87.7794 Z=0
    g272: LineSegment StartX=362.567 StartY=-89.8542 StartZ=0 EndX=321.579 EndY=-67.3492 EndZ=0
    g273: LineSegment StartX=318.073 StartY=-69.424 StartZ=0 EndX=318.073 EndY=-87.7794 EndZ=0
    g274: LineSegment StartX=322.073 StartY=-91.7794 StartZ=0 EndX=362.073 EndY=-91.7794 EndZ=0
    g275: Circle CenterX=2.07281 CenterY=124.221 CenterZ=0 NormalX=0 NormalY=0 NormalZ=1 AngleXU=0 Radius=1
    g276: Circle CenterX=1.57905 CenterY=122.295 CenterZ=0 NormalX=0 NormalY=0 NormalZ=1 AngleXU=0 Radius=1
    g277: BSplineCurve PolesCount=3 KnotsCount=2 Degree=2 IsPeriodic=0
    g278: GeomPoint X=2.07281 Y=124.221 Z=0
    g279: GeomPoint X=1.57905 Y=122.295 Z=0
    g280: Circle CenterX=42.0728 CenterY=124.221 CenterZ=0 NormalX=0 NormalY=0 NormalZ=1 AngleXU=0 Radius=1
    g281: Circle CenterX=46.0728 CenterY=124.221 CenterZ=0 NormalX=0 NormalY=0 NormalZ=1 AngleXU=0 Radius=1
    g282: Circle CenterX=46.0728 CenterY=120.221 CenterZ=0 NormalX=0 NormalY=0 NormalZ=1 AngleXU=0 Radius=1
    g283: BSplineCurve PolesCount=3 KnotsCount=2 Degree=2 IsPeriodic=0
    g284: GeomPoint X=42.0728 Y=124.221 Z=0
    g285: GeomPoint X=46.0728 Y=120.221 Z=0
    g286: Circle CenterX=46.0728 CenterY=109.865 CenterZ=0 NormalX=0 NormalY=0 NormalZ=1 AngleXU=0 Radius=1
    g287: Circle CenterX=46.0728 CenterY=105.865 CenterZ=0 NormalX=0 NormalY=0 NormalZ=1 AngleXU=0 Radius=1
    g288: Circle CenterX=42.0728 CenterY=105.865 CenterZ=0 NormalX=0 NormalY=0 NormalZ=1 AngleXU=0 Radius=1
    g289: BSplineCurve PolesCount=3 KnotsCount=2 Degree=2 IsPeriodic=0
    g290: GeomPoint X=46.0728 Y=109.865 Z=0
    g291: GeomPoint X=42.0728 Y=105.865 Z=0
    g292: Circle CenterX=35.5028 CenterY=105.865 CenterZ=0 NormalX=0 NormalY=0 NormalZ=1 AngleXU=0 Radius=1
    g293: Circle CenterX=31.5028 CenterY=105.865 CenterZ=0 NormalX=0 NormalY=0 NormalZ=1 AngleXU=0 Radius=1
    g294: Circle CenterX=27.9965 CenterY=107.79 CenterZ=0 NormalX=0 NormalY=0 NormalZ=1 AngleXU=0 Radius=1
    g295: BSplineCurve PolesCount=3 KnotsCount=2 Degree=2 IsPeriodic=0
    g296: GeomPoint X=35.5028 Y=105.865 Z=0
    g297: GeomPoint X=27.9965 Y=107.79 Z=0
    g298: LineSegment StartX=2.07281 StartY=124.221 StartZ=0 EndX=42.0728 EndY=124.221 EndZ=0
    g299: LineSegment StartX=46.0728 StartY=120.221 StartZ=0 EndX=46.0728 EndY=109.865 EndZ=0
    g300: LineSegment StartX=42.0728 StartY=105.865 StartZ=0 EndX=35.5028 EndY=105.865 EndZ=0
    g301: LineSegment StartX=27.9965 StartY=107.79 StartZ=0 EndX=1.57905 EndY=122.295 EndZ=0
    g302: Circle CenterX=42.5666 CenterY=-67.3492 CenterZ=0 NormalX=0 NormalY=0 NormalZ=1 AngleXU=0 Radius=1
    g303: Circle CenterX=46.0728 CenterY=-65.424 CenterZ=0 NormalX=0 NormalY=0 NormalZ=1 AngleXU=0 Radius=1
    g304: Circle CenterX=46.0728 CenterY=-69.424 CenterZ=0 NormalX=0 NormalY=0 NormalZ=1 AngleXU=0 Radius=1
    g305: BSplineCurve PolesCount=3 KnotsCount=2 Degree=2 IsPeriodic=0
    g306: GeomPoint X=42.5666 Y=-67.3492 Z=0
    g307: GeomPoint X=46.0728 Y=-69.424 Z=0
    g308: Circle CenterX=46.0728 CenterY=-87.7794 CenterZ=0 NormalX=0 NormalY=0 NormalZ=1 AngleXU=0 Radius=1
    g309: Circle CenterX=46.0728 CenterY=-91.7794 CenterZ=0 NormalX=0 NormalY=0 NormalZ=1 AngleXU=0 Radius=1
    g310: Circle CenterX=42.0728 CenterY=-91.7794 CenterZ=0 NormalX=0 NormalY=0 NormalZ=1 AngleXU=0 Radius=1
    g311: BSplineCurve PolesCount=3 KnotsCount=2 Degree=2 IsPeriodic=0
    g312: GeomPoint X=46.0728 Y=-87.7794 Z=0
    g313: GeomPoint X=42.0728 Y=-91.7794 Z=0
    g314: Circle CenterX=2.07281 CenterY=-91.7794 CenterZ=0 NormalX=0 NormalY=0 NormalZ=1 AngleXU=0 Radius=1
    g315: Circle CenterX=-1.92719 CenterY=-91.7794 CenterZ=0 NormalX=0 NormalY=0 NormalZ=1 AngleXU=0 Radius=1
    g316: Circle CenterX=1.57905 CenterY=-89.8542 CenterZ=0 NormalX=0 NormalY=0 NormalZ=1 AngleXU=0 Radius=1
    g317: BSplineCurve PolesCount=3 KnotsCount=2 Degree=2 IsPeriodic=0
    g318: GeomPoint X=2.07281 Y=-91.7794 Z=0
    g319: GeomPoint X=1.57905 Y=-89.8542 Z=0
    g320: LineSegment StartX=2.07281 StartY=-91.7794 StartZ=0 EndX=42.0728 EndY=-91.7794 EndZ=0
    g321: LineSegment StartX=46.0728 StartY=-87.7794 StartZ=0 EndX=46.0728 EndY=-69.424 EndZ=0
    g322: LineSegment StartX=42.5666 StartY=-67.3492 StartZ=0 EndX=1.57905 EndY=-89.8542 EndZ=0
    g323: Circle CenterX=322.073 CenterY=76.4095 CenterZ=0 NormalX=0 NormalY=0 NormalZ=1 AngleXU=0 Radius=4
    g324: BSplineCurve PolesCount=3 KnotsCount=2 Degree=2 IsPeriodic=0
    g325: GeomPoint X=318.073 Y=72.4095 Z=0
    g326: GeomPoint X=322.073 Y=76.4095 Z=0
    g327: Circle CenterX=375.073 CenterY=72.4095 CenterZ=0 NormalX=0 NormalY=0 NormalZ=1 AngleXU=0 Radius=1
    g328: Circle CenterX=375.073 CenterY=76.4095 CenterZ=0 NormalX=0 NormalY=0 NormalZ=1 AngleXU=0 Radius=1
    g329: Circle CenterX=371.073 CenterY=76.4095 CenterZ=0 NormalX=0 NormalY=0 NormalZ=1 AngleXU=0 Radius=1
    g330: BSplineCurve PolesCount=3 KnotsCount=2 Degree=2 IsPeriodic=0
    g331: GeomPoint X=375.073 Y=72.4095 Z=0
    g332: GeomPoint X=371.073 Y=76.4095 Z=0
    g333: LineSegment StartX=322.073 StartY=76.4095 StartZ=0 EndX=371.073 EndY=76.4095 EndZ=0
    g334: LineSegment StartX=318.073 StartY=72.4095 StartZ=0 EndX=318.073 EndY=-47.4805 EndZ=0
    g335: LineSegment StartX=375.073 StartY=72.4095 StartZ=0 EndX=375.073 EndY=-78.7896 EndZ=0
    g336: ArcOfCircle CenterX=-26.9272 CenterY=22.1087 CenterZ=0 NormalX=0 NormalY=0 NormalZ=1 AngleXU=0 Radius=4 StartAngle=5e-16 EndAngle=3.14159
    g337: LineSegment StartX=-22.9272 StartY=22.1087 StartZ=0 EndX=-18.9272 EndY=-83.7794 EndZ=0
    g338: LineSegment StartX=-34.9272 StartY=-83.7794 StartZ=0 EndX=-30.9272 EndY=22.1087 EndZ=0
    g339: ArcOfCircle CenterX=391.073 CenterY=22.1087 CenterZ=0 NormalX=0 NormalY=0 NormalZ=1 AngleXU=0 Radius=4 StartAngle=0 EndAngle=3.14159
    g340: LineSegment StartX=387.073 StartY=22.1087 StartZ=0 EndX=383.073 EndY=-83.7794 EndZ=0
    g341: LineSegment StartX=395.073 StartY=22.1087 StartZ=0 EndX=399.073 EndY=-83.7794 EndZ=0
    g342: Circle CenterX=-10.9272 CenterY=-78.7794 CenterZ=0 NormalX=0 NormalY=0 NormalZ=1 AngleXU=0 Radius=1
    g343: Circle CenterX=-10.9272 CenterY=-82.7794 CenterZ=0 NormalX=0 NormalY=0 NormalZ=1 AngleXU=0 Radius=1
    g344: Circle CenterX=-7.42095 CenterY=-80.8542 CenterZ=0 NormalX=0 NormalY=0 NormalZ=1 AngleXU=0 Radius=1
    g345: BSplineCurve PolesCount=3 KnotsCount=2 Degree=2 IsPeriodic=0
    g346: GeomPoint X=-10.9272 Y=-78.7794 Z=0
    g347: GeomPoint X=-7.42095 Y=-80.8542 Z=0
    g348: Circle CenterX=42.5666 CenterY=-53.4075 CenterZ=0 NormalX=0 NormalY=0 NormalZ=1 AngleXU=0 Radius=1
    g349: Circle CenterX=46.0728 CenterY=-51.4823 CenterZ=0 NormalX=0 NormalY=0 NormalZ=1 AngleXU=0 Radius=1
    g350: Circle CenterX=46.0728 CenterY=-47.4823 CenterZ=0 NormalX=0 NormalY=0 NormalZ=1 AngleXU=0 Radius=1
    g351: BSplineCurve PolesCount=3 KnotsCount=2 Degree=2 IsPeriodic=0
    g352: GeomPoint X=42.5666 Y=-53.4075 Z=0
    g353: GeomPoint X=46.0728 Y=-47.4823 Z=0
    g354: Circle CenterX=46.0728 CenterY=72.4095 CenterZ=0 NormalX=0 NormalY=0 NormalZ=1 AngleXU=0 Radius=1
    g355: Circle CenterX=46.0728 CenterY=76.4095 CenterZ=0 NormalX=0 NormalY=0 NormalZ=1 AngleXU=0 Radius=1
    g356: Circle CenterX=42.0728 CenterY=76.4095 CenterZ=0 NormalX=0 NormalY=0 NormalZ=1 AngleXU=0 Radius=1
    g357: BSplineCurve PolesCount=3 KnotsCount=2 Degree=2 IsPeriodic=0
    g358: GeomPoint X=46.0728 Y=72.4095 Z=0
    g359: GeomPoint X=42.0728 Y=76.4095 Z=0
    g360: Circle CenterX=-6.92719 CenterY=76.4095 CenterZ=0 NormalX=0 NormalY=0 NormalZ=1 AngleXU=0 Radius=1
    g361: Circle CenterX=-10.9272 CenterY=76.4095 CenterZ=0 NormalX=0 NormalY=0 NormalZ=1 AngleXU=0 Radius=1
    g362: Circle CenterX=-10.9272 CenterY=72.4095 CenterZ=0 NormalX=0 NormalY=0 NormalZ=1 AngleXU=0 Radius=1
    g363: BSplineCurve PolesCount=3 KnotsCount=2 Degree=2 IsPeriodic=0
    g364: GeomPoint X=-6.92719 Y=76.4095 Z=0
    g365: GeomPoint X=-10.9272 Y=72.4095 Z=0
    g366: LineSegment StartX=-10.9272 StartY=72.4095 StartZ=0 EndX=-10.9272 EndY=-78.7794 EndZ=0
    g367: LineSegment StartX=-7.42095 StartY=-80.8542 StartZ=0 EndX=42.5666 EndY=-53.4075 EndZ=0
    g368: LineSegment StartX=46.0728 StartY=-47.4823 StartZ=0 EndX=46.0728 EndY=72.4095 EndZ=0
    g369: LineSegment StartX=42.0728 StartY=76.4095 StartZ=0 EndX=-6.92719 EndY=76.4095 EndZ=0
    g370: LineSegment StartX=-42.9272 StartY=136.221 StartZ=0 EndX=407.073 EndY=136.221 EndZ=0
    g371: LineSegment StartX=232.072 StartY=136.221 StartZ=0 EndX=220.072 EndY=136.221 EndZ=0
    g372: LineSegment StartX=232.072 StartY=136.221 StartZ=0 EndX=232.072 EndY=124.221 EndZ=0
    g373: LineSegment StartX=220.072 StartY=136.221 StartZ=0 EndX=220.072 EndY=124.221 EndZ=0
    g374: LineSegment StartX=220.072 StartY=136.221 StartZ=0 EndX=226.072 EndY=136.221 EndZ=0
    g375: LineSegment StartX=220.072 StartY=136.221 StartZ=0 EndX=220.072 EndY=130.221 EndZ=0
    g376: LineSegment StartX=220.072 StartY=124.221 StartZ=0 EndX=226.072 EndY=124.221 EndZ=0
    g377: LineSegment StartX=232.072 StartY=124.221 StartZ=0 EndX=232.072 EndY=127.221 EndZ=0
    g378: LineSegment StartX=232.072 StartY=136.221 StartZ=0 EndX=232.072 EndY=133.221 EndZ=0
    g379-g383: Circle x5 (B-spline internal-alignment scaffolding for g384; pole/knot coordinates omitted)
    g384: BSplineCurve PolesCount=5 KnotsCount=3 Degree=3 IsPeriodic=0
    g385: GeomPoint X=232.072 Y=133.221 Z=0
    g386: GeomPoint X=223.072 Y=130.221 Z=0
    g387: GeomPoint X=232.072 Y=127.221 Z=0
    g388: LineSegment StartX=189.124 StartY=124.221 StartZ=0 EndX=302.073 EndY=124.221 EndZ=0
    g389: LineSegment StartX=132.072 StartY=136.221 StartZ=0 EndX=132.072 EndY=124.221 EndZ=0
    g390: LineSegment StartX=132.072 StartY=136.221 StartZ=0 EndX=144.072 EndY=136.221 EndZ=0
    g391: LineSegment StartX=144.072 StartY=136.221 StartZ=0 EndX=144.072 EndY=124.221 EndZ=0
    g392: LineSegment StartX=144.072 StartY=136.221 StartZ=0 EndX=138.072 EndY=136.221 EndZ=0
    g393: LineSegment StartX=144.072 StartY=136.221 StartZ=0 EndX=144.072 EndY=130.221 EndZ=0
    g394: LineSegment StartX=132.072 StartY=136.221 StartZ=0 EndX=132.072 EndY=133.221 EndZ=0
    g395: LineSegment StartX=132.072 StartY=133.221 StartZ=0 EndX=132.072 EndY=127.221 EndZ=0
    g396-g400: Circle x5 (B-spline internal-alignment scaffolding for g401; pole/knot coordinates omitted)
    g401: BSplineCurve PolesCount=5 KnotsCount=3 Degree=3 IsPeriodic=0
    g402: GeomPoint X=132.072 Y=133.221 Z=0
    g403: GeomPoint X=141.072 Y=130.221 Z=0
    g404: GeomPoint X=132.072 Y=127.221 Z=0
    g405: LineSegment StartX=132.072 StartY=124.221 StartZ=0 EndX=175.022 EndY=124.221 EndZ=0
    g406: LineSegment StartX=62.0728 StartY=124.221 StartZ=0 EndX=132.072 EndY=124.221 EndZ=0
    g407: LineSegment StartX=132.072 StartY=136.221 StartZ=0 EndX=131.457 EndY=138.832 EndZ=0
    ... +61 more geometry lines
  constraints (808):
    c: Vertical(g0)
    c: Vertical(g1)
    c: Block(g1)
    c: Block(g0)
    c: Weight(g4) = 1
    c: Equal(g4,g5)
    c: Equal(g4,g6)
    c: InternalAlignment(g4,g7)
    c: InternalAlignment(g5,g7)
    c: InternalAlignment(g6,g7)
    c: InternalAlignment(g8,g7)
    c: InternalAlignment(g9,g7)
    c: Weight(g10) = 1
    c: Equal(g10,g11)
    c: Equal(g10,g12)
    c: InternalAlignment(g10,g13)
    c: InternalAlignment(g11,g13)
    c: InternalAlignment(g12,g13)
    c: InternalAlignment(g14,g13)
    c: InternalAlignment(g15,g13)
    c: Block(g13)
    c: Block(g7)
    c: Weight(g16) = 1
    c: Equal(g16,g17)
    c: Equal(g16,g18)
    c: InternalAlignment(g16,g19)
    c: InternalAlignment(g17,g19)
    c: InternalAlignment(g18,g19)
    c: InternalAlignment(g20,g19)
    c: InternalAlignment(g21,g19)
    c: Weight(g22) = 1
    c: Equal(g22,g23)
    c: Equal(g22,g24)
    c: InternalAlignment(g22,g25)
    c: InternalAlignment(g23,g25)
    c: InternalAlignment(g24,g25)
    c: InternalAlignment(g26,g25)
    c: InternalAlignment(g27,g25)
    c: Block(g25)
    c: Block(g19)
    c: Weight(g28) = 1
    c: Equal(g28,g29)
    c: Equal(g28,g30)
    c: InternalAlignment(g28,g31)
    c: InternalAlignment(g29,g31)
    c: InternalAlignment(g30,g31)
    c: InternalAlignment(g32,g31)
    c: InternalAlignment(g33,g31)
    c: Weight(g34) = 1
    c: Equal(g34,g35)
    c: Equal(g34,g36)
    c: InternalAlignment(g34,g37)
    c: InternalAlignment(g35,g37)
    c: InternalAlignment(g36,g37)
    c: InternalAlignment(g38,g37)
    c: InternalAlignment(g39,g37)
    c: Block(g31)
    c: Block(g37)
    c: Coincident(g40,g1)
    c: Coincident(g40,g0)
    c: Horizontal(g40)
    c: Distance(g40) = 450
    c: Weight(g41) = 1
    c: Equal(g41,g42)
    c: Equal(g41,g43)
    c: InternalAlignment(g41,g44)
    c: InternalAlignment(g42,g44)
    c: InternalAlignment(g43,g44)
    c: InternalAlignment(g45,g44)
    c: InternalAlignment(g46,g44)
    c: Block(g44)
    c: Weight(g47) = 1
    c: Equal(g47,g48)
    c: Equal(g47,g49)
    c: InternalAlignment(g47,g50)
    c: InternalAlignment(g48,g50)
    c: InternalAlignment(g49,g50)
    c: InternalAlignment(g51,g50)
    c: InternalAlignment(g52,g50)
    c: Block(g50)
    c: Weight(g53) = 1
    c: Equal(g53,g54)
    c: Equal(g53,g55)
    c: InternalAlignment(g53,g56)
    c: InternalAlignment(g54,g56)
    c: InternalAlignment(g55,g56)
    c: InternalAlignment(g57,g56)
    c: InternalAlignment(g58,g56)
    c: Block(g56)
    c: Weight(g59) = 1
    c: Equal(g59,g60)
    c: Equal(g59,g61)
    c: InternalAlignment(g59,g62)
    c: InternalAlignment(g60,g62)
    c: InternalAlignment(g61,g62)
    c: InternalAlignment(g63,g62)
    c: InternalAlignment(g64,g62)
    c: Block(g62)
    c: Weight(g65) = 1
    c: Equal(g65,g66)
    c: Equal(g65,g67)
    c: InternalAlignment(g65,g68)
    c: InternalAlignment(g66,g68)
    c: InternalAlignment(g67,g68)
    c: InternalAlignment(g69,g68)
    c: InternalAlignment(g70,g68)
    c: Weight(g71) = 1
    c: Equal(g71,g72)
    c: Equal(g71,g73)
    c: InternalAlignment(g71,g74)
    c: InternalAlignment(g72,g74)
    c: InternalAlignment(g73,g74)
    c: InternalAlignment(g75,g74)
    c: InternalAlignment(g76,g74)
    c: Block(g68)
    c: Block(g74)
    c: Coincident(g77,g68)
    c: Coincident(g77,g74)
    c: Vertical(g77)
    c: Coincident(g78,g68)
    c: Coincident(g78,g50)
    c: Coincident(g79,g50)
    c: Coincident(g79,g74)
    c: Weight(g80) = 1
    c: Equal(g80,g81)
    c: Equal(g80,g82)
    c: InternalAlignment(g80,g83)
    c: InternalAlignment(g81,g83)
    c: InternalAlignment(g82,g83)
    c: InternalAlignment(g84,g83)
    c: InternalAlignment(g85,g83)
    c: Weight(g86) = 1
    c: Equal(g86,g87)
    c: Equal(g86,g88)
    c: InternalAlignment(g86,g89)
    c: InternalAlignment(g87,g89)
    c: InternalAlignment(g88,g89)
    c: InternalAlignment(g90,g89)
    c: InternalAlignment(g91,g89)
    c: Block(g83)
    c: Block(g89)
    c: Coincident(g92,g83)
    c: Coincident(g92,g89)
    c: Vertical(g92)
    c: Coincident(g93,g83)
    c: Coincident(g93,g44)
    c: Coincident(g94,g44)
    c: Coincident(g94,g89)
    c: Weight(g95) = 1
    c: Equal(g95,g96)
    c: Equal(g95,g97)
    c: InternalAlignment(g95,g98)
    c: InternalAlignment(g96,g98)
    c: InternalAlignment(g97,g98)
    c: InternalAlignment(g99,g98)
    c: InternalAlignment(g100,g98)
    c: Weight(g101) = 1
    c: Equal(g101,g102)
    c: Equal(g101,g103)
    c: InternalAlignment(g101,g104)
    c: InternalAlignment(g102,g104)
    c: InternalAlignment(g103,g104)
    c: InternalAlignment(g105,g104)
    c: InternalAlignment(g106,g104)
    c: Block(g98)
    c: Block(g104)
    c: Coincident(g107,g98)
    c: Coincident(g107,g104)
    c: Vertical(g107)
    c: Coincident(g108,g104)
    c: Coincident(g108,g62)
    c: Coincident(g109,g62)
    c: Coincident(g109,g98)
    c: Weight(g110) = 1
    c: Equal(g110,g111)
    c: Equal(g110,g112)
    c: InternalAlignment(g110,g113)
    c: InternalAlignment(g111,g113)
    c: InternalAlignment(g112,g113)
    c: InternalAlignment(g114,g113)
    c: InternalAlignment(g115,g113)
    c: Weight(g116) = 1
    c: Equal(g116,g117)
    c: Equal(g116,g118)
    c: InternalAlignment(g116,g119)
    c: InternalAlignment(g117,g119)
    c: InternalAlignment(g118,g119)
    c: InternalAlignment(g120,g119)
    c: InternalAlignment(g121,g119)
    c: Block(g113)
    c: Block(g119)
    c: Coincident(g122,g113)
    c: Coincident(g122,g119)
    c: Vertical(g122)
    c: Coincident(g123,g119)
    c: Coincident(g123,g56)
    c: Coincident(g124,g56)
    c: Coincident(g124,g113)
    c: Weight(g125) = 1
    c: Equal(g125,g126)
    c: Equal(g125,g127)
    c: InternalAlignment(g125,g128)
    c: InternalAlignment(g126,g128)
    c: InternalAlignment(g127,g128)
    c: InternalAlignment(g129,g128)
    c: InternalAlignment(g130,g128)
    c: Weight(g131) = 1
    c: Equal(g131,g132)
    c: Equal(g131,g133)
    c: InternalAlignment(g131,g134)
    c: InternalAlignment(g132,g134)
    c: InternalAlignment(g133,g134)
    c: InternalAlignment(g135,g134)
    c: InternalAlignment(g136,g134)
    c: Weight(g137) = 1
    c: Equal(g137,g138)
    c: Equal(g137,g139)
    c: InternalAlignment(g137,g140)
    c: InternalAlignment(g138,g140)
    c: InternalAlignment(g139,g140)
    c: InternalAlignment(g141,g140)
    c: InternalAlignment(g142,g140)
    c: Weight(g143) = 1
    c: Equal(g143,g144)
    c: Equal(g143,g145)
    c: InternalAlignment(g143,g146)
    c: InternalAlignment(g144,g146)
    c: InternalAlignment(g145,g146)
    c: InternalAlignment(g147,g146)
    c: InternalAlignment(g148,g146)
    c: Block(g146)
    c: Block(g140)
    c: Block(g134)
    c: Block(g128)
    c: Coincident(g149,g25)
    c: Coincident(g149,g146)
    c: Coincident(g150,g146)
    c: Coincident(g150,g140)
    c: Horizontal(g150)
    c: Coincident(g151,g140)
    c: Coincident(g151,g25)
    c: Vertical(g151)
    c: Coincident(g152,g19)
    c: Coincident(g152,g134)
    c: Vertical(g152)
    c: Coincident(g153,g134)
    c: Coincident(g153,g128)
    c: Horizontal(g153)
    c: Coincident(g154,g128)
    c: Coincident(g154,g19)
    c: Weight(g155) = 1
    c: Equal(g155,g156)
    c: Equal(g155,g157)
    c: InternalAlignment(g155,g158)
    c: InternalAlignment(g156,g158)
    c: InternalAlignment(g157,g158)
    c: InternalAlignment(g159,g158)
    c: InternalAlignment(g160,g158)
    c: Weight(g161) = 1
    c: Equal(g161,g162)
    c: Equal(g161,g163)
    c: InternalAlignment(g161,g164)
    c: InternalAlignment(g162,g164)
    c: InternalAlignment(g163,g164)
    c: InternalAlignment(g165,g164)
    c: InternalAlignment(g166,g164)
    c: Weight(g167) = 1
    c: Equal(g167,g168)
    c: Equal(g167,g169)
    c: InternalAlignment(g167,g170)
    c: InternalAlignment(g168,g170)
    c: InternalAlignment(g169,g170)
    c: InternalAlignment(g171,g170)
    c: InternalAlignment(g172,g170)
    c: Weight(g173) = 1
    c: Equal(g173,g174)
    c: Equal(g173,g175)
    c: InternalAlignment(g173,g176)
    c: InternalAlignment(g174,g176)
    c: InternalAlignment(g175,g176)
    c: InternalAlignment(g177,g176)
    c: InternalAlignment(g178,g176)
    c: Block(g176)
    c: Block(g170)
    c: Block(g164)
    c: Block(g158)
    c: Coincident(g179,g170)
    c: Coincident(g179,g7)
    c: Vertical(g179)
    c: Coincident(g180,g13)
    c: Coincident(g180,g164)
    c: Vertical(g180)
    c: Coincident(g181,g158)
    c: Coincident(g181,g13)
    c: Coincident(g182,g7)
    c: Weight(g183) = 1
    c: Equal(g183,g184)
    c: Equal(g183,g185)
    c: InternalAlignment(g183,g186)
    c: InternalAlignment(g184,g186)
    c: InternalAlignment(g185,g186)
    c: InternalAlignment(g187,g186)
    c: InternalAlignment(g188,g186)
    c: Weight(g189) = 1
    c: Equal(g189,g190)
    c: Equal(g189,g191)
    c: InternalAlignment(g189,g192)
    c: InternalAlignment(g190,g192)
    c: InternalAlignment(g191,g192)
    c: InternalAlignment(g193,g192)
    c: InternalAlignment(g194,g192)
    c: Block(g192)
    c: Block(g186)
    c: Coincident(g195,g192)
    c: Coincident(g195,g31)
    c: Coincident(g196,g31)
    c: Coincident(g196,g186)
    c: Coincident(g197,g186)
    c: Coincident(g197,g192)
    c: Vertical(g197)
    c: Weight(g198) = 1
    c: Equal(g198,g199)
    c: Equal(g198,g200)
    c: InternalAlignment(g198,g201)
    c: InternalAlignment(g199,g201)
    c: InternalAlignment(g200,g201)
    c: InternalAlignment(g202,g201)
    c: InternalAlignment(g203,g201)
    c: Weight(g204) = 1
    c: Equal(g204,g205)
    c: Equal(g204,g206)
    c: InternalAlignment(g204,g207)
    c: InternalAlignment(g205,g207)
    c: InternalAlignment(g206,g207)
    c: InternalAlignment(g208,g207)
    c: InternalAlignment(g209,g207)
    c: Block(g207)
    c: Block(g201)
    c: Coincident(g210,g201)
    c: Coincident(g210,g37)
    c: Coincident(g211,g37)
    c: Coincident(g211,g207)
    c: Coincident(g212,g207)
    c: Coincident(g212,g201)
    c: Vertical(g212)
    c: Horizontal(g213)
    c: Block(g213)
    c: Vertical(g214)
    c: Block(g214)
    c: Block(g215)
    c: Weight(g216) = 1
    c: Equal(g216,g217)
    c: Equal(g216,g218)
    c: InternalAlignment(g216,g219)
    c: InternalAlignment(g217,g219)
    c: InternalAlignment(g218,g219)
    c: InternalAlignment(g220,g219)
    c: InternalAlignment(g221,g219)
    c: Weight(g222) = 1
    c: Equal(g222,g223)
    c: Equal(g222,g224)
    c: InternalAlignment(g222,g225)
    c: InternalAlignment(g223,g225)
    c: InternalAlignment(g224,g225)
    c: InternalAlignment(g226,g225)
    c: InternalAlignment(g227,g225)
    c: Weight(g228) = 1
    c: Equal(g228,g229)
    c: Equal(g228,g230)
    c: InternalAlignment(g228,g231)
    c: InternalAlignment(g229,g231)
    c: InternalAlignment(g230,g231)
    c: InternalAlignment(g232,g231)
    c: InternalAlignment(g233,g231)
    c: Weight(g234) = 1
    c: Equal(g234,g235)
    c: Equal(g234,g236)
    c: InternalAlignment(g234,g237)
    c: InternalAlignment(g235,g237)
    c: InternalAlignment(g236,g237)
    c: InternalAlignment(g238,g237)
    c: InternalAlignment(g239,g237)
    c: Block(g219)
    c: Block(g225)
    c: Block(g231)
    c: Block(g237)
    c: Coincident(g240,g225)
    c: Coincident(g240,g219)
    c: Horizontal(g240)
    c: Block(g182)
    c: Weight(g241) = 1
    c: Equal(g241,g242)
    c: Equal(g241,g243)
    c: InternalAlignment(g241,g244)
    c: InternalAlignment(g242,g244)
    c: InternalAlignment(g243,g244)
    c: InternalAlignment(g245,g244)
    c: InternalAlignment(g246,g244)
    c: Weight(g247) = 1
    c: Equal(g247,g248)
    c: Equal(g247,g249)
    c: InternalAlignment(g247,g250)
    c: InternalAlignment(g248,g250)
    c: InternalAlignment(g249,g250)
    c: InternalAlignment(g251,g250)
    c: InternalAlignment(g252,g250)
    c: Block(g244)
    c: Block(g250)
    c: Coincident(g253,g244)
    c: Coincident(g253,g250)
    c: Weight(g254) = 1
    c: Equal(g254,g255)
    c: Equal(g254,g256)
    c: InternalAlignment(g254,g257)
    c: InternalAlignment(g255,g257)
    c: InternalAlignment(g256,g257)
    c: InternalAlignment(g258,g257)
    c: InternalAlignment(g259,g257)
    c: Weight(g260) = 1
    c: Equal(g260,g261)
    c: Equal(g260,g262)
    c: InternalAlignment(g260,g263)
    c: InternalAlignment(g261,g263)
    c: InternalAlignment(g262,g263)
    c: InternalAlignment(g264,g263)
    c: InternalAlignment(g265,g263)
    c: Weight(g266) = 1
    c: Equal(g266,g267)
    c: Equal(g266,g268)
    c: InternalAlignment(g266,g269)
    c: InternalAlignment(g267,g269)
    c: InternalAlignment(g268,g269)
    c: InternalAlignment(g270,g269)
    c: InternalAlignment(g271,g269)
    c: Block(g269)
    c: Block(g263)
    c: Block(g257)
    c: Coincident(g272,g263)
    c: Coincident(g272,g257)
    c: Coincident(g273,g257)
    c: Coincident(g273,g269)
    c: Vertical(g273)
    c: Coincident(g274,g269)
    c: Coincident(g274,g263)
    c: Horizontal(g274)
    c: Weight(g275) = 1
    c: Equal(g275,g276)
    c: InternalAlignment(g275,g277)
    c: InternalAlignment(g276,g277)
    c: InternalAlignment(g278,g277)
    c: InternalAlignment(g279,g277)
    c: Weight(g280) = 1
    c: InternalAlignment(g281,g283)
    c: InternalAlignment(g282,g283)
    c: InternalAlignment(g284,g283)
    c: InternalAlignment(g285,g283)
    c: Weight(g286) = 1
    c: Equal(g286,g287)
    c: Equal(g286,g288)
    c: InternalAlignment(g286,g289)
    c: InternalAlignment(g287,g289)
    c: InternalAlignment(g288,g289)
    c: InternalAlignment(g290,g289)
    c: InternalAlignment(g291,g289)
    c: Equal(g292,g293)
    c: Equal(g292,g294)
    c: InternalAlignment(g292,g295)
    c: InternalAlignment(g293,g295)
    c: InternalAlignment(g294,g295)
    c: InternalAlignment(g296,g295)
    c: InternalAlignment(g297,g295)
    c: Block(g283)
    c: Block(g289)
    c: Block(g295)
    c: Block(g277)
    c: Coincident(g298,g277)
    c: Coincident(g298,g283)
    c: Horizontal(g298)
    c: Coincident(g299,g283)
    c: Coincident(g299,g289)
    c: Vertical(g299)
    c: Coincident(g300,g289)
    c: Coincident(g300,g295)
    c: Horizontal(g300)
    c: Coincident(g301,g295)
    c: Coincident(g301,g277)
    c: Weight(g302) = 1
    c: Equal(g302,g303)
    c: Equal(g302,g304)
    c: InternalAlignment(g302,g305)
    c: InternalAlignment(g303,g305)
    c: InternalAlignment(g304,g305)
    c: InternalAlignment(g306,g305)
    c: InternalAlignment(g307,g305)
    c: Weight(g308) = 1
    c: Equal(g308,g309)
    c: Equal(g308,g310)
    c: InternalAlignment(g308,g311)
    c: InternalAlignment(g309,g311)
    c: InternalAlignment(g310,g311)
    c: InternalAlignment(g312,g311)
    c: Weight(g314) = 1
    c: Equal(g314,g315)
    c: Equal(g314,g316)
    c: InternalAlignment(g314,g317)
    c: InternalAlignment(g315,g317)
    c: InternalAlignment(g316,g317)
    c: InternalAlignment(g318,g317)
    c: InternalAlignment(g319,g317)
    c: Block(g317)
    c: Block(g311)
    c: Block(g305)
    c: Coincident(g320,g317)
    c: Coincident(g320,g311)
    c: Horizontal(g320)
    c: Coincident(g321,g311)
    c: Coincident(g321,g305)
    c: Vertical(g321)
    c: Coincident(g322,g305)
    c: Coincident(g322,g317)
    c: InternalAlignment(g323,g324)
    c: InternalAlignment(g325,g324)
    c: InternalAlignment(g326,g324)
    c: Block(g324)
    c: Equal(g327,g328)
    c: Equal(g327,g329)
    c: InternalAlignment(g327,g330)
    c: InternalAlignment(g328,g330)
    c: InternalAlignment(g329,g330)
    c: InternalAlignment(g331,g330)
    c: InternalAlignment(g332,g330)
    c: Block(g330)
    c: Coincident(g333,g324)
    c: Horizontal(g333)
    c: Block(g333)
    c: Coincident(g334,g324)
    c: Coincident(g334,g250)
    c: Vertical(g334)
    c: Coincident(g335,g330)
    c: Coincident(g335,g244)
    c: Vertical(g335)
    c: Block(g336)
    c: Block(g2)
    c: Distance(g334) = 119.89
    c: Coincident(g337,g336)
    c: Coincident(g337,g2)
    c: Coincident(g338,g2)
    c: Coincident(g338,g336)
    c: Block(g3)
    c: Block(g339)
    c: Coincident(g340,g339)
    c: Coincident(g340,g3)
    c: Coincident(g341,g339)
    c: Coincident(g341,g3)
    c: Block(g341)
    c: Block(g340)
    c: Weight(g342) = 1
    c: Equal(g342,g344)
    c: InternalAlignment(g342,g345)
    c: InternalAlignment(g343,g345)
    c: InternalAlignment(g344,g345)
    c: InternalAlignment(g346,g345)
    c: InternalAlignment(g347,g345)
    c: InternalAlignment(g352,g351)
    c: InternalAlignment(g353,g351)
    c: InternalAlignment(g355,g357)
    c: Horizontal(g369)
    c: Coincident(g370,g0)
    c: Horizontal(g370)
    c: Block(g370)
    c: Distance(g370) = 450
    c: Horizontal(g371)
    c: Distance(g371) = 12
    c: Coincident(g373,g371)
    c: Vertical(g373)
    c: Horizontal(g374)
    c: Vertical(g375)
    c: Distance(g375) = 6
    c: Coincident(g375,g371)
    c: Coincident(g374,g371)
    c: Block(g373)
    c: Coincident(g376,g373)
    c: Horizontal(g376)
    c: Distance(g376) = 6
    c: Vertical(g377)
    c: Distance(g377) = 3
    c: Vertical(g378)
    c: Distance(g378) = 3
    c: Coincident(g372,g377)
    c: Coincident(g384,g378)
    c: Weight(g379) = 1
    c: Equal(g379,g380)
    c: Coincident(g380,g374)
    c: Equal(g379,g381)
    c: Coincident(g381,g375)
    c: Equal(g379,g382)
    c: Coincident(g382,g376)
    c: Equal(g379,g383)
    c: Coincident(g384,g377)
    c: InternalAlignment(g379-g383 -> g384) x5
    c: InternalAlignment(g385,g384)
    c: InternalAlignment(g386,g384)
    c: InternalAlignment(g387,g384)
    c: Coincident(g388,g164)
    c: Coincident(g388,g158)
    c: Coincident(g392,g390)
    c: Vertical(g393)
    c: Distance(g393) = 6
    c: Coincident(g393,g390)
    c: Vertical(g394)
    c: Distance(g394) = 3
    c: Vertical(g395)
    c: Distance(g395) = 6
    c: Coincident(g395,g394)
    c: Coincident(g401,g394)
    c: Weight(g396) = 1
    c: Equal(g396,g397)
    c: Coincident(g397,g392)
    c: Equal(g396,g398)
    c: Coincident(g398,g393)
    c: Equal(g396,g399)
    c: Equal(g396,g400)
    c: Coincident(g401,g395)
    c: InternalAlignment(g396-g400 -> g401) x5
    c: InternalAlignment(g402,g401)
    c: InternalAlignment(g403,g401)
    c: InternalAlignment(g404,g401)
    c: Coincident(g405,g389)
    c: Coincident(g405,g170)
    c: Horizontal(g405)
    c: Block(g401)
    c: Coincident(g406,g176)
    c: Coincident(g406,g389)
    c: Horizontal(g406)
    c: Block(g405)
    c: Coincident(g408,g389)
    c: PointOnObject(g408,g153)
    c: Vertical(g408)
    c: Block(g409)
    c: Coincident(g410,g409)
    c: Vertical(g410)
    c: PointOnObject(g410,g40)
    c: Block(g410)
    c: Coincident(g411,g409)
    c: Vertical(g411)
    c: Block(g411)
    c: Vertical(g412)
    c: Distance(g412) = 3
    c: Equal(g379,g415) = 1
    c: Equal(g415,g416)
    c: InternalAlignment(g415,g417)
    c: InternalAlignment(g416,g417)
    c: InternalAlignment(g413,g417)
    c: InternalAlignment(g414,g417)
    c: InternalAlignment(g418,g417)
    c: Block(g417)
    c: Coincident(g418,g412)
    c: Coincident(g419,g417)
    c: PointOnObject(g419,g150)
    c: Vertical(g419)
    c: Distance(g420) = 3
    c: Block(g420)
    c: Distance(g421) = 3
    c: Parallel(g421,g420)
    c: Coincident(g421,g420)
    c: Coincident(g422,g420)
    c: Perpendicular(g422,g420)
    c: Distance(g422) = 3
    c: Coincident(g423,g421)
    c: Perpendicular(g423,g421)
    c: Distance(g423) = 3
    c: Coincident(g424,g420)
    c: Perpendicular(g424,g421)
    c: Distance(g424) = 6
    c: Coincident(g425,g424)
    c: PointOnObject(g423,g425)
    c: Coincident(g426,g420)
    c: PointOnObject(g426,g79)
    c: Block(g426)
    c: Distance(g427) = 2.76
    c: Coincident(g428,g427)
    c: Parallel(g427,g428)
    c: PointOnObject(g428,g181)
    c: Distance(g428) = 2.41
    c: Block(g428)
    c: Coincident(g429,g427)
    c: Distance(g429) = 6.6
    c: Perpendicular(g429,g428)
    c: Distance(g430) = 6.6
    c: Coincident(g431,g429)
    c: Coincident(g431,g430)
    c: Block(g432)
    c: Coincident(g433,g432)
    c: Vertical(g433)
    c: Distance(g433) = 3.6
    c: Coincident(g434,g427)
    c: Parallel(g427,g434)
    c: PointOnObject(g434,g78)
    c: Block(g434)
    c: Coincident(g435,g421)
    c: Parallel(g435,g421)
    c: PointOnObject(g435,g211)
    c: Block(g435)
    c: Coincident(g436,g435)
    c: Vertical(g436)
    c: PointOnObject(g436,g210)
    c: Coincident(g437,g436)
    c: Perpendicular(g437,g210)
    c: Distance(g437) = 3
    c: Coincident(g438,g437)
    c: Block(g437)
    c: Distance(g438) = 3
    c: Parallel(g437,g438)
    c: Coincident(g439,g438)
    c: Distance(g439) = 3
    c: Parallel(g438,g439)
    c: Coincident(g440,g439)
    c: Parallel(g440,g437)
    c: PointOnObject(g440,g124)
    c: PointOnObject(g441,g53)
    c: Tangent(g440,g441)
    c: Coincident(g442,g439)
    c: Perpendicular(g442,g439)
    c: Coincident(g443,g437)
    c: Parallel(g443,g442)
    c: Distance(g443) = 3
    c: Distance(g442) = 3
    c: PointOnObject(g442,g444)
    c: Block(g444)
    c: PointOnObject(g445,g123)
    c: Perpendicular(g123,g445)
    c: Distance(g445) = 2.41
    c: Block(g445)
    c: Coincident(g446,g445)
    c: Perpendicular(g123,g446)
    c: Distance(g446) = 2.76
    c: Coincident(g447,g446)
    c: Perpendicular(g123,g447)
    c: PointOnObject(g447,g149)
    c: Coincident(g448,g445)
    c: Parallel(g123,g448)
    c: Distance(g448) = 6.6
    c: Coincident(g449,g446)
    c: Parallel(g123,g449)
    c: Coincident(g450,g448)
    c: Distance(g449) = 6.6
    c: Coincident(g449,g450)
    c: Block(g149)
    c: Block(g124)
    c: Block(g211)
    c: Block(g181)
    c: Block(g78)
    c: Block(g79)
    c: Block(g430)
    c: Coincident(g451,g447)
    c: Distance(g451) = 46
    c: Parallel(g149,g451)
    c: Coincident(g452,g451)
    c: Horizontal(g452)
    c: PointOnObject(g452,g154)
    c: Coincident(g453,g451)
    c: Vertical(g453)
    c: Distance(g453) = 9
    c: Block(g452)
    c: PointOnObject(g454,g93)
    c: Distance(g455) = 6.6
    c: Distance(g456) = 6.6
    c: Block(g454)
    c: Coincident(g457,g456)
    c: Coincident(g457,g455)
    c: Perpendicular(g457,g182)
    c: Coincident(g458,g455)
    c: Perpendicular(g458,g182)
    c: PointOnObject(g458,g182)
    c: Block(g458)
    c: Block(g457)
    c: Block(g456)
    c: PointOnObject(g459,g196)
    c: Perpendicular(g196,g459)
    c: Distance(g459) = 3
    c: Coincident(g460,g459)
    c: Perpendicular(g196,g460)
    c: Distance(g460) = 3
    c: Coincident(g461,g460)
    c: Perpendicular(g196,g461)
    c: Distance(g461) = 3
    c: Coincident(g462,g461)
    c: Tangent(g462,g41)
    c: PointOnObject(g462,g94)
    c: Block(g462)
    c: Block(g459)
    c: Coincident(g463,g459)
    c: Parallel(g196,g463)
    c: Distance(g463) = 3
    c: Coincident(g464,g461)
    c: Distance(g464) = 3
    c: Parallel(g196,g464)
    c: Coincident(g465,g460)
    c: Distance(g465) = 6
    c: Parallel(g465,g196)
    c: Coincident(g466,g465)
    c: PointOnObject(g464,g466)
    c: Block(g466)
    c: Coincident(g467,g458)
    c: Vertical(g467)
    c: PointOnObject(g467,g195)
    c: Coincident(g468,g467)
    c: Perpendicular(g195,g468)
FEATURE [Sketcher::SketchObject] Sketch004  label="rightSideBottom"
  FullyConstrained = false
  sketch-geometry (91):
    g0: ArcOfCircle CenterX=391.073 CenterY=-83.7794 CenterZ=0 NormalX=0 NormalY=0 NormalZ=1 AngleXU=0 Radius=8 StartAngle=3.14159 EndAngle=6.28319
    g1: Circle CenterX=306.073 CenterY=-81.8102 CenterZ=0 NormalX=0 NormalY=0 NormalZ=1 AngleXU=0 Radius=1
    g2: Circle CenterX=306.073 CenterY=-77.8102 CenterZ=0 NormalX=0 NormalY=0 NormalZ=1 AngleXU=0 Radius=1
    g3: Circle CenterX=302.567 CenterY=-42.9683 CenterZ=0 NormalX=0 NormalY=0 NormalZ=1 AngleXU=0 Radius=1
    g4: Circle CenterX=306.073 CenterY=-44.8935 CenterZ=0 NormalX=0 NormalY=0 NormalZ=1 AngleXU=0 Radius=1
    g5: Circle CenterX=306.073 CenterY=-40.8935 CenterZ=0 NormalX=0 NormalY=0 NormalZ=1 AngleXU=0 Radius=1
    g6: BSplineCurve PolesCount=3 KnotsCount=2 Degree=2 IsPeriodic=0
    g7: GeomPoint X=302.567 Y=-42.9683 Z=0
    g8: GeomPoint X=306.073 Y=-40.8935 Z=0
    g9: Circle CenterX=371.567 CenterY=-80.8644 CenterZ=0 NormalX=0 NormalY=0 NormalZ=1 AngleXU=0 Radius=1
    g10: Circle CenterX=375.073 CenterY=-82.7896 CenterZ=0 NormalX=0 NormalY=0 NormalZ=1 AngleXU=0 Radius=1
    g11: Circle CenterX=375.073 CenterY=-78.7896 CenterZ=0 NormalX=0 NormalY=0 NormalZ=1 AngleXU=0 Radius=1
    g12: GeomPoint X=371.567 Y=-80.8644 Z=0
    g13: GeomPoint X=375.073 Y=-78.7896 Z=0
    g14: Circle CenterX=318.073 CenterY=-51.4823 CenterZ=0 NormalX=0 NormalY=0 NormalZ=1 AngleXU=0 Radius=1
    g15: Circle CenterX=318.073 CenterY=-47.4805 CenterZ=0 NormalX=0 NormalY=0 NormalZ=1 AngleXU=0 Radius=1
    g16: GeomPoint X=321.579 Y=-53.4075 Z=0
    g17: GeomPoint X=318.073 Y=-47.4805 Z=0
    g18: Circle CenterX=321.579 CenterY=-67.3492 CenterZ=0 NormalX=0 NormalY=0 NormalZ=1 AngleXU=0 Radius=1
    g19: Circle CenterX=318.073 CenterY=-65.424 CenterZ=0 NormalX=0 NormalY=0 NormalZ=1 AngleXU=0 Radius=1
    g20: Circle CenterX=318.073 CenterY=-69.424 CenterZ=0 NormalX=0 NormalY=0 NormalZ=1 AngleXU=0 Radius=1
    g21: GeomPoint X=321.579 Y=-67.3492 Z=0
    g22: GeomPoint X=318.073 Y=-69.424 Z=0
    g23: Circle CenterX=362.567 CenterY=-89.8542 CenterZ=0 NormalX=0 NormalY=0 NormalZ=1 AngleXU=0 Radius=1
    g24: Circle CenterX=366.073 CenterY=-91.7794 CenterZ=0 NormalX=0 NormalY=0 NormalZ=1 AngleXU=0 Radius=1
    g25: Circle CenterX=362.073 CenterY=-91.7794 CenterZ=0 NormalX=0 NormalY=0 NormalZ=1 AngleXU=0 Radius=1
    g26: GeomPoint X=362.567 Y=-89.8542 Z=0
    g27: GeomPoint X=362.073 Y=-91.7794 Z=0
    g28: Circle CenterX=322.073 CenterY=-91.7794 CenterZ=0 NormalX=0 NormalY=0 NormalZ=1 AngleXU=0 Radius=1
    g29: Circle CenterX=318.073 CenterY=-91.7794 CenterZ=0 NormalX=0 NormalY=0 NormalZ=1 AngleXU=0 Radius=1
    g30: Circle CenterX=318.073 CenterY=-87.7794 CenterZ=0 NormalX=0 NormalY=0 NormalZ=1 AngleXU=0 Radius=1
    g31: GeomPoint X=322.073 Y=-91.7794 Z=0
    g32: GeomPoint X=318.073 Y=-87.7794 Z=0
    g33: ArcOfCircle CenterX=391.073 CenterY=22.1087 CenterZ=0 NormalX=0 NormalY=0 NormalZ=1 AngleXU=0 Radius=4 StartAngle=0 EndAngle=3.14159
    g34: LineSegment StartX=387.073 StartY=22.1087 StartZ=0 EndX=383.073 EndY=-83.7794 EndZ=0
    g35: LineSegment StartX=395.073 StartY=22.1087 StartZ=0 EndX=399.073 EndY=-83.7794 EndZ=0
    g36: LineSegment StartX=232.072 StartY=-103.779 StartZ=0 EndX=232.072 EndY=-100.779 EndZ=0
    g37: GeomPoint X=232.072 Y=-94.7794 Z=0
    g38: GeomPoint X=223.072 Y=-97.7794 Z=0
    g39: Circle CenterX=232.072 CenterY=-94.7794 CenterZ=0 NormalX=0 NormalY=0 NormalZ=1 AngleXU=0 Radius=1
    g40: Circle CenterX=232.072 CenterY=-100.779 CenterZ=0 NormalX=0 NormalY=0 NormalZ=1 AngleXU=0 Radius=1
    g41: BSplineCurve PolesCount=5 KnotsCount=3 Degree=3 IsPeriodic=0
    g42: GeomPoint X=232.072 Y=-100.779 Z=0
    g43: LineSegment StartX=232.072 StartY=-94.7794 StartZ=0 EndX=232.072 EndY=-91.7794 EndZ=0
    g44: LineSegment StartX=245.072 StartY=-31.3037 StartZ=0 EndX=243.535 EndY=-33.1602 EndZ=0
    g45: LineSegment StartX=241.775 StartY=-35.2862 StartZ=0 EndX=240.266 EndY=-37.1092 EndZ=0
    g46: LineSegment StartX=243.535 StartY=-33.1602 StartZ=0 EndX=248.619 EndY=-37.3688 EndZ=0
    g47: LineSegment StartX=241.775 StartY=-35.2862 StartZ=0 EndX=246.859 EndY=-39.4949 EndZ=0
    g48: LineSegment StartX=248.619 StartY=-37.3688 StartZ=0 EndX=246.859 EndY=-39.4949 EndZ=0
    g49: LineSegment StartX=232.072 StartY=-103.779 StartZ=0 EndX=407.073 EndY=-103.779 EndZ=0
    g50: LineSegment StartX=299.888 StartY=-86.6413 StartZ=0 EndX=240.266 EndY=-37.1092 EndZ=0
    g51: LineSegment StartX=245.072 StartY=-11.4025 StartZ=0 EndX=302.567 EndY=-42.9683 EndZ=0
    g52: BSplineCurve PolesCount=3 KnotsCount=2 Degree=2 IsPeriodic=0
    g53: BSplineCurve PolesCount=3 KnotsCount=2 Degree=2 IsPeriodic=0
    g54: LineSegment StartX=321.579 StartY=-53.4075 StartZ=0 EndX=371.567 EndY=-80.8644 EndZ=0
    g55: BSplineCurve PolesCount=3 KnotsCount=2 Degree=2 IsPeriodic=0
    g56: BSplineCurve PolesCount=3 KnotsCount=2 Degree=2 IsPeriodic=0
    g57: BSplineCurve PolesCount=3 KnotsCount=2 Degree=2 IsPeriodic=0
    g58: LineSegment StartX=318.073 StartY=-69.424 StartZ=0 EndX=318.073 EndY=-87.7794 EndZ=0
    g59: LineSegment StartX=321.579 StartY=-67.3492 StartZ=0 EndX=362.567 EndY=-89.8542 EndZ=0
    g60: LineSegment StartX=362.073 StartY=-91.7794 StartZ=0 EndX=322.073 EndY=-91.7794 EndZ=0
    g61: BSplineCurve PolesCount=3 KnotsCount=2 Degree=2 IsPeriodic=0
    g62: BSplineCurve PolesCount=3 KnotsCount=2 Degree=2 IsPeriodic=0
    g63: LineSegment StartX=245.072 StartY=-31.3037 StartZ=0 EndX=302.996 EndY=-79.2541 EndZ=0
    g64: LineSegment StartX=302.567 StartY=-56.9099 StartZ=0 EndX=239.193 EndY=-22.1109 EndZ=0
    g65: LineSegment StartX=306.073 StartY=-62.8351 StartZ=0 EndX=306.073 EndY=-77.8102 EndZ=0
    g66: BSplineCurve PolesCount=3 KnotsCount=2 Degree=2 IsPeriodic=0
    g67: LineSegment StartX=298.776 StartY=-91.7794 StartZ=0 EndX=232.072 EndY=-91.7794 EndZ=0
    g68: LineSegment StartX=245.072 StartY=-11.4025 StartZ=0 EndX=243.628 EndY=-14.0323 EndZ=0
    g69: LineSegment StartX=240.741 StartY=-19.2917 StartZ=0 EndX=239.193 EndY=-22.1109 EndZ=0
    g70: LineSegment StartX=243.628 StartY=-14.0323 StartZ=0 EndX=246.258 EndY=-15.476 EndZ=0
    g71: LineSegment StartX=240.741 StartY=-19.2917 StartZ=0 EndX=243.37 EndY=-20.7355 EndZ=0
    g72: ArcOfCircle CenterX=247.444 CenterY=-19.5495 CenterZ=0 NormalX=0 NormalY=0 NormalZ=1 AngleXU=0 Radius=4.24264 StartAngle=3.4249 EndAngle=8.13729
    g73: LineSegment StartX=407.073 StartY=-103.779 StartZ=0 EndX=407.073 EndY=48.2206 EndZ=0
    g74: LineSegment StartX=375.073 StartY=48.2206 StartZ=0 EndX=375.073 EndY=-78.7896 EndZ=0
    g75: LineSegment StartX=375.073 StartY=48.2206 StartZ=0 EndX=382.073 EndY=48.2206 EndZ=0
    g76: LineSegment StartX=407.073 StartY=48.2206 StartZ=0 EndX=400.073 EndY=48.2206 EndZ=0
    g77: LineSegment StartX=394.073 StartY=48.2206 StartZ=0 EndX=394.073 EndY=52.2206 EndZ=0
    g78: LineSegment StartX=388.073 StartY=48.2206 StartZ=0 EndX=388.073 EndY=58.2206 EndZ=0
    g79: ArcOfCircle CenterX=385.073 CenterY=61.2206 CenterZ=0 NormalX=0 NormalY=0 NormalZ=1 AngleXU=0 Radius=4.24264 StartAngle=5.49779 EndAngle=10.2102
    g80: ArcOfCircle CenterX=397.073 CenterY=55.2206 CenterZ=0 NormalX=0 NormalY=0 NormalZ=1 AngleXU=0 Radius=4.24264 StartAngle=5.49779 EndAngle=10.2102
    g81: LineSegment StartX=382.073 StartY=58.2206 StartZ=0 EndX=382.073 EndY=48.2206 EndZ=0
    g82: LineSegment StartX=400.073 StartY=52.2206 StartZ=0 EndX=400.073 EndY=48.2206 EndZ=0
    g83: LineSegment StartX=394.073 StartY=48.2206 StartZ=0 EndX=388.073 EndY=48.2206 EndZ=0
    g84: LineSegment StartX=306.073 StartY=-40.8935 StartZ=0 EndX=306.073 EndY=-27.5935 EndZ=0
    g85: LineSegment StartX=318.073 StartY=-27.5935 StartZ=0 EndX=318.073 EndY=-47.4805 EndZ=0
    g86: LineSegment StartX=306.073 StartY=-27.5935 StartZ=0 EndX=310.073 EndY=-27.5935 EndZ=0
    g87: LineSegment StartX=318.073 StartY=-27.5935 StartZ=0 EndX=314.073 EndY=-27.5935 EndZ=0
    g88: LineSegment StartX=310.073 StartY=-27.5935 StartZ=0 EndX=310.073 EndY=-31.5935 EndZ=0
    g89: LineSegment StartX=314.073 StartY=-27.5935 StartZ=0 EndX=314.073 EndY=-31.5935 EndZ=0
    g90: ArcOfCircle CenterX=312.073 CenterY=-33.5935 CenterZ=0 NormalX=0 NormalY=0 NormalZ=1 AngleXU=0 Radius=2.82843 StartAngle=2.35619 EndAngle=7.06858
  constraints (121):
    c: Distance(g44) = 2.41
    c: Block(g44)
    c: Coincident(g46,g44)
    c: Coincident(g49,g36)
    c: Horizontal(g49)
    c: Block(g49)
    c: Coincident(g50,g45)
    c: Block(g50)
    c: Coincident(g51,g6)
    c: Block(g51)
    c: Coincident(g54,g52)
    c: Coincident(g54,g53)
    c: Coincident(g58,g56)
    c: Coincident(g58,g57)
    c: Vertical(g58)
    c: Coincident(g59,g56)
    c: Coincident(g59,g55)
    c: Coincident(g60,g55)
    c: Coincident(g60,g57)
    c: Horizontal(g60)
    c: Block(g61)
    c: Block(g62)
    c: Coincident(g63,g44)
    c: Coincident(g63,g62)
    c: Coincident(g64,g61)
    c: Coincident(g65,g61)
    c: Coincident(g65,g62)
    c: Vertical(g65)
    c: Block(g66)
    c: Coincident(g66,g50)
    c: Coincident(g67,g66)
    c: Coincident(g67,g43)
    c: Horizontal(g67)
    c: Coincident(g68,g51)
    c: Perpendicular(g68,g51)
    c: Coincident(g69,g64)
    c: Coincident(g70,g68)
    c: Distance(g70) = 3
    c: Distance(g71) = 3
    c: Perpendicular(g68,g70)
    c: Coincident(g72,g70)
    c: Coincident(g72,g71)
    c: Block(g72)
    c: Block(g69)
    c: Block(g71)
    c: Block(g54)
    c: Block(g59)
    c: Block(g58)
    c: Block(g60)
    c: Block(g67)
    c: Block(g43)
    c: Block(g36)
    c: Block(g48)
    c: Block(g46)
    c: Block(g47)
    c: Block(g45)
    c: Block(g35)
    c: Block(g34)
    c: Block(g0)
    c: Block(g33)
    c: Block(g52)
    c: Block(g6)
    c: Block(g41)
    c: Block(g57)
    c: Block(g55)
    c: Block(g53)
    c: Block(g68)
    c: Distance(g48) = 2.76
    c: Distance(g47) = 6.6
    c: Distance(g45) = 2.36657
    c: Coincident(g73,g49)
    c: Vertical(g73)
    c: Distance(g73) = 152
    c: Coincident(g74,g53)
    c: Vertical(g74)
    c: Block(g74)
    c: Coincident(g75,g74)
    c: Horizontal(g75)
    c: Distance(g75) = 7
    c: Horizontal(g76)
    c: Distance(g76) = 7
    c: Coincident(g76,g73)
    c: Vertical(g77)
    c: Distance(g77) = 4
    c: Vertical(g78)
    c: Distance(g78) = 10
    c: Coincident(g79,g78)
    c: Coincident(g80,g77)
    c: Block(g80)
    c: Block(g79)
    c: Coincident(g81,g79)
    c: Coincident(g81,g75)
    c: Vertical(g81)
    c: Coincident(g82,g80)
    c: Coincident(g82,g76)
    c: Vertical(g82)
    c: Coincident(g83,g77)
    c: Coincident(g83,g78)
    c: Horizontal(g83)
    c: Coincident(g84,g6)
    c: Vertical(g84)
    c: Distance(g84) = 13.3
    c: Coincident(g85,g52)
    c: Vertical(g85)
    c: Block(g85)
    c: Coincident(g86,g84)
    c: Horizontal(g86)
    c: Distance(g86) = 4
    c: Coincident(g87,g85)
    c: Horizontal(g87)
    c: Distance(g87) = 4
    c: Coincident(g88,g86)
    c: Vertical(g88)
    c: Coincident(g89,g87)
    c: Vertical(g89)
    c: Distance(g88) = 4
    c: Distance(g89) = 4
    c: Coincident(g90,g88)
    c: Coincident(g90,g89)
    c: Block(g90)
    c: Block(g56)
FEATURE [Sketcher::SketchObject] Sketch005  label="middleTop"
  FullyConstrained = true
  sketch-geometry (133):
    g0: Circle CenterX=175.025 CenterY=27.0667 CenterZ=0 NormalX=0 NormalY=0 NormalZ=1 AngleXU=0 Radius=1
    g1: Circle CenterX=179.022 CenterY=24.8665 CenterZ=0 NormalX=0 NormalY=0 NormalZ=1 AngleXU=0 Radius=1
    g2: Circle CenterX=179.022 CenterY=27.0606 CenterZ=0 NormalX=0 NormalY=0 NormalZ=1 AngleXU=0 Radius=1
    g3: BSplineCurve PolesCount=3 KnotsCount=2 Degree=2 IsPeriodic=0
    g4: GeomPoint X=175.025 Y=27.0667 Z=0
    g5: GeomPoint X=179.022 Y=27.0606 Z=0
    g6: Circle CenterX=189.124 CenterY=27.0628 CenterZ=0 NormalX=0 NormalY=0 NormalZ=1 AngleXU=0 Radius=1
    g7: Circle CenterX=185.124 CenterY=24.8665 CenterZ=0 NormalX=0 NormalY=0 NormalZ=1 AngleXU=0 Radius=1
    g8: Circle CenterX=185.124 CenterY=27.0606 CenterZ=0 NormalX=0 NormalY=0 NormalZ=1 AngleXU=0 Radius=1
    g9: BSplineCurve PolesCount=3 KnotsCount=2 Degree=2 IsPeriodic=0
    g10: GeomPoint X=189.124 Y=27.0628 Z=0
    g11: GeomPoint X=185.124 Y=27.0606 Z=0
    g12: Circle CenterX=165.871 CenterY=18.1458 CenterZ=0 NormalX=0 NormalY=0 NormalZ=1 AngleXU=0 Radius=1
    g13: Circle CenterX=169.377 CenterY=16.2206 CenterZ=0 NormalX=0 NormalY=0 NormalZ=1 AngleXU=0 Radius=1
    g14: Circle CenterX=165.871 CenterY=14.2956 CenterZ=0 NormalX=0 NormalY=0 NormalZ=1 AngleXU=0 Radius=1
    g15: BSplineCurve PolesCount=3 KnotsCount=2 Degree=2 IsPeriodic=0
    g16: GeomPoint X=165.871 Y=18.1458 Z=0
    g17: GeomPoint X=165.871 Y=14.2956 Z=0
    g18: Circle CenterX=198.275 CenterY=18.1318 CenterZ=0 NormalX=0 NormalY=0 NormalZ=1 AngleXU=0 Radius=1
    g19: Circle CenterX=194.768 CenterY=16.2206 CenterZ=0 NormalX=0 NormalY=0 NormalZ=1 AngleXU=0 Radius=1
    g20: Circle CenterX=198.264 CenterY=14.2963 CenterZ=0 NormalX=0 NormalY=0 NormalZ=1 AngleXU=0 Radius=1
    g21: BSplineCurve PolesCount=3 KnotsCount=2 Degree=2 IsPeriodic=0
    g22: GeomPoint X=198.275 Y=18.1318 Z=0
    g23: GeomPoint X=198.264 Y=14.2963 Z=0
    g24: Circle CenterX=125.607 CenterY=54.1951 CenterZ=0 NormalX=0 NormalY=0 NormalZ=1 AngleXU=0 Radius=1
    g25: Circle CenterX=139.632 CenterY=46.4944 CenterZ=0 NormalX=0 NormalY=0 NormalZ=1 AngleXU=0 Radius=1
    g26: Circle CenterX=127.326 CenterY=56.7187 CenterZ=0 NormalX=0 NormalY=0 NormalZ=1 AngleXU=0 Radius=1
    g27: BSplineCurve PolesCount=3 KnotsCount=2 Degree=2 IsPeriodic=0
    g28: GeomPoint X=125.607 Y=54.1951 Z=0
    g29: GeomPoint X=127.326 Y=56.7187 Z=0
    g30: Circle CenterX=236.824 CenterY=56.7187 CenterZ=0 NormalX=0 NormalY=0 NormalZ=1 AngleXU=0 Radius=1
    g31: Circle CenterX=224.513 CenterY=46.4944 CenterZ=0 NormalX=0 NormalY=0 NormalZ=1 AngleXU=0 Radius=1
    g32: Circle CenterX=238.538 CenterY=54.1951 CenterZ=0 NormalX=0 NormalY=0 NormalZ=1 AngleXU=0 Radius=1
    g33: BSplineCurve PolesCount=3 KnotsCount=2 Degree=2 IsPeriodic=0
    g34: GeomPoint X=236.824 Y=56.7187 Z=0
    g35: GeomPoint X=238.538 Y=54.1951 Z=0
    g36: Circle CenterX=189.121 CenterY=124.221 CenterZ=0 NormalX=0 NormalY=0 NormalZ=1 AngleXU=0 Radius=1
    g37: Circle CenterX=185.124 CenterY=124.221 CenterZ=0 NormalX=0 NormalY=0 NormalZ=1 AngleXU=0 Radius=1
    g38: Circle CenterX=185.124 CenterY=120.221 CenterZ=0 NormalX=0 NormalY=0 NormalZ=1 AngleXU=0 Radius=1
    g39: BSplineCurve PolesCount=3 KnotsCount=2 Degree=2 IsPeriodic=0
    g40: GeomPoint X=189.121 Y=124.221 Z=0
    g41: GeomPoint X=185.124 Y=120.221 Z=0
    g42: Circle CenterX=175.022 CenterY=124.221 CenterZ=0 NormalX=0 NormalY=0 NormalZ=1 AngleXU=0 Radius=1
    g43: Circle CenterX=179.022 CenterY=124.221 CenterZ=0 NormalX=0 NormalY=0 NormalZ=1 AngleXU=0 Radius=1
    g44: Circle CenterX=179.022 CenterY=120.221 CenterZ=0 NormalX=0 NormalY=0 NormalZ=1 AngleXU=0 Radius=1
    g45: BSplineCurve PolesCount=3 KnotsCount=2 Degree=2 IsPeriodic=0
    g46: GeomPoint X=175.022 Y=124.221 Z=0
    g47: GeomPoint X=179.022 Y=120.221 Z=0
    g48: LineSegment StartX=232.071 StartY=124.221 StartZ=0 EndX=232.071 EndY=127.221 EndZ=0
    g49-g52: Circle x4 (B-spline internal-alignment scaffolding for g53; pole/knot coordinates omitted)
    g53: BSplineCurve PolesCount=5 KnotsCount=3 Degree=3 IsPeriodic=0
    g54: GeomPoint X=232.072 Y=133.221 Z=0
    g55: GeomPoint X=223.072 Y=130.221 Z=0
    g56: GeomPoint X=232.071 Y=127.221 Z=0
    g57-g61: Circle x5 (B-spline internal-alignment scaffolding for g62; pole/knot coordinates omitted)
    g62: BSplineCurve PolesCount=5 KnotsCount=3 Degree=3 IsPeriodic=0
    g63: GeomPoint X=132.072 Y=133.221 Z=0
    g64: GeomPoint X=141.072 Y=130.221 Z=0
    g65: GeomPoint X=132.072 Y=127.221 Z=0
    g66: ArcOfCircle CenterX=247.391 CenterY=52.0843 CenterZ=0 NormalX=0 NormalY=0 NormalZ=1 AngleXU=0 Radius=4.24264 StartAngle=4.42912 EndAngle=9.14151
    g67: LineSegment StartX=240.687 StartY=51.8263 StartZ=0 EndX=239.192 EndY=54.5542 EndZ=0
    g68: LineSegment StartX=243.575 StartY=46.5669 StartZ=0 EndX=245.072 EndY=43.8408 EndZ=0
    g69: LineSegment StartX=240.168 StartY=69.471 StartZ=0 EndX=241.708 EndY=67.6172 EndZ=0
    g70: LineSegment StartX=246.783 StartY=71.8328 StartZ=0 EndX=248.546 EndY=69.7098 EndZ=0
    g71: LineSegment StartX=245.073 StartY=63.5726 StartZ=0 EndX=243.476 EndY=65.4955 EndZ=0
    g72: LineSegment StartX=123.967 StartY=69.4706 StartZ=0 EndX=122.37 EndY=67.5474 EndZ=0
    g73: LineSegment StartX=232.072 StartY=133.221 StartZ=0 EndX=232.072 EndY=136.221 EndZ=0
    g74: LineSegment StartX=232.072 StartY=136.221 StartZ=0 EndX=132.072 EndY=136.221 EndZ=0
    g75: LineSegment StartX=132.072 StartY=136.221 StartZ=0 EndX=132.072 EndY=133.221 EndZ=0
    g76: LineSegment StartX=132.072 StartY=127.221 StartZ=0 EndX=132.072 EndY=124.221 EndZ=0
    g77: LineSegment StartX=132.072 StartY=124.221 StartZ=0 EndX=175.022 EndY=124.221 EndZ=0
    g78: LineSegment StartX=189.121 StartY=124.221 StartZ=0 EndX=232.071 EndY=124.221 EndZ=0
    g79: LineSegment StartX=185.124 StartY=120.221 StartZ=0 EndX=185.124 EndY=27.0606 EndZ=0
    g80: LineSegment StartX=189.124 StartY=27.0628 StartZ=0 EndX=240.168 EndY=69.471 EndZ=0
    g81: LineSegment StartX=241.708 StartY=67.6172 StartZ=0 EndX=246.783 EndY=71.8328 EndZ=0
    g82: LineSegment StartX=248.546 StartY=69.7098 StartZ=0 EndX=243.476 EndY=65.4955 EndZ=0
    g83: LineSegment StartX=245.073 StartY=63.5726 StartZ=0 EndX=236.824 EndY=56.7187 EndZ=0
    g84: LineSegment StartX=238.538 StartY=54.1951 StartZ=0 EndX=239.192 EndY=54.5542 EndZ=0
    g85: LineSegment StartX=240.687 StartY=51.8263 StartZ=0 EndX=243.317 EndY=53.2701 EndZ=0
    g86: LineSegment StartX=246.205 StartY=48.0108 StartZ=0 EndX=243.575 EndY=46.5669 EndZ=0
    g87: LineSegment StartX=245.072 StartY=43.8408 StartZ=0 EndX=198.275 EndY=18.1318 EndZ=0
    g88: LineSegment StartX=165.871 StartY=18.1458 StartZ=0 EndX=118.934 EndY=43.9178 EndZ=0
    g89: LineSegment StartX=118.934 StartY=43.9178 StartZ=0 EndX=120.377 EndY=46.5474 EndZ=0
    g90: LineSegment StartX=117.748 StartY=47.9913 StartZ=0 EndX=120.377 EndY=46.5474 EndZ=0
    g91: LineSegment StartX=120.635 StartY=53.2507 StartZ=0 EndX=123.265 EndY=51.8068 EndZ=0
    g92: LineSegment StartX=123.265 StartY=51.8068 StartZ=0 EndX=124.73 EndY=54.6766 EndZ=0
    g93: ArcOfCircle CenterX=116.562 CenterY=52.0649 CenterZ=0 NormalX=0 NormalY=0 NormalZ=1 AngleXU=0 Radius=4.24264 StartAngle=0.283267 EndAngle=4.99566
    g94: LineSegment StartX=124.73 StartY=54.6766 StartZ=0 EndX=125.607 EndY=54.1951 EndZ=0
    g95: LineSegment StartX=127.326 StartY=56.7187 StartZ=0 EndX=119.072 EndY=63.5741 EndZ=0
    g96: LineSegment StartX=119.072 StartY=63.5741 StartZ=0 EndX=120.669 EndY=65.4973 EndZ=0
    g97: LineSegment StartX=120.669 StartY=65.4973 StartZ=0 EndX=115.591 EndY=69.7147 EndZ=0
    g98: LineSegment StartX=115.591 StartY=69.7147 StartZ=0 EndX=117.293 EndY=71.7641 EndZ=0
    g99: LineSegment StartX=117.293 StartY=71.7641 StartZ=0 EndX=122.37 EndY=67.5474 EndZ=0
    g100: LineSegment StartX=123.967 StartY=69.4706 StartZ=0 EndX=175.025 EndY=27.0667 EndZ=0
    g101: LineSegment StartX=179.022 StartY=27.0606 StartZ=0 EndX=179.022 EndY=120.221 EndZ=0
    g102-g117: Circle x16 (B-spline internal-alignment scaffolding for g118; pole/knot coordinates omitted)
    g118: BSplineCurve PolesCount=16 KnotsCount=14 Degree=3 IsPeriodic=0
    g119-g132: GeomPoint x14 (B-spline internal-alignment scaffolding for g118; pole/knot coordinates omitted)
  constraints (180):
    c: Weight(g0) = 1
    c: Equal(g0,g1)
    c: Equal(g0,g2)
    c: InternalAlignment(g0,g3)
    c: InternalAlignment(g1,g3)
    c: InternalAlignment(g2,g3)
    c: InternalAlignment(g4,g3)
    c: InternalAlignment(g5,g3)
    c: Weight(g6) = 1
    c: Equal(g6,g7)
    c: Equal(g6,g8)
    c: InternalAlignment(g6,g9)
    c: InternalAlignment(g7,g9)
    c: InternalAlignment(g8,g9)
    c: InternalAlignment(g10,g9)
    c: InternalAlignment(g11,g9)
    c: Block(g9)
    c: Block(g3)
    c: Weight(g12) = 1
    c: Equal(g12,g13)
    c: Equal(g12,g14)
    c: InternalAlignment(g12,g15)
    c: InternalAlignment(g13,g15)
    c: InternalAlignment(g14,g15)
    c: InternalAlignment(g16,g15)
    c: InternalAlignment(g17,g15)
    c: Weight(g18) = 1
    c: Equal(g18,g19)
    c: Equal(g18,g20)
    c: InternalAlignment(g18,g21)
    c: InternalAlignment(g19,g21)
    c: InternalAlignment(g20,g21)
    c: InternalAlignment(g22,g21)
    c: InternalAlignment(g23,g21)
    c: Block(g15)
    c: Block(g21)
    c: Weight(g24) = 1
    c: Equal(g24,g25)
    c: Equal(g24,g26)
    c: InternalAlignment(g24,g27)
    c: InternalAlignment(g25,g27)
    c: InternalAlignment(g26,g27)
    c: InternalAlignment(g28,g27)
    c: InternalAlignment(g29,g27)
    c: Block(g27)
    c: Weight(g30) = 1
    c: Equal(g30,g31)
    c: Equal(g30,g32)
    c: InternalAlignment(g30,g33)
    c: InternalAlignment(g31,g33)
    c: InternalAlignment(g32,g33)
    c: InternalAlignment(g34,g33)
    c: InternalAlignment(g35,g33)
    c: Block(g33)
    c: Weight(g36) = 1
    c: Equal(g36,g37)
    c: Equal(g36,g38)
    c: InternalAlignment(g36,g39)
    c: InternalAlignment(g37,g39)
    c: InternalAlignment(g38,g39)
    c: InternalAlignment(g40,g39)
    c: InternalAlignment(g41,g39)
    c: Weight(g42) = 1
    c: Equal(g42,g43)
    c: Equal(g42,g44)
    c: InternalAlignment(g42,g45)
    c: InternalAlignment(g43,g45)
    c: InternalAlignment(g44,g45)
    c: InternalAlignment(g46,g45)
    c: InternalAlignment(g47,g45)
    c: Block(g45)
    c: Block(g39)
    c: Vertical(g48)
    c: Distance(g48) = 3
    c: Weight(g49) = 1
    c: Equal(g49,g50)
    c: Equal(g49,g51)
    c: Equal(g49,g52)
    c: Coincident(g53,g48)
    c: InternalAlignment(g49-g52 -> g53) x4
    c: InternalAlignment(g54,g53)
    c: InternalAlignment(g55,g53)
    c: InternalAlignment(g56,g53)
    c: Weight(g57) = 1
    c: Equal(g57, g58-g61) x4
    c: InternalAlignment(g57-g61 -> g62) x5
    c: InternalAlignment(g63,g62)
    c: InternalAlignment(g64,g62)
    c: InternalAlignment(g65,g62)
    c: Block(g62)
    c: Block(g67)
    c: Block(g68)
    c: Distance(g69) = 2.41
    c: Distance(g70) = 2.76
    c: Distance(g71) = 2.5
    c: Distance(g72) = 2.5
    c: Block(g66)
    c: Block(g48)
    c: Block(g53)
    c: Coincident(g73,g53)
    c: Vertical(g73)
    c: Distance(g73) = 3
    c: Coincident(g74,g73)
    c: Horizontal(g74)
    c: Distance(g74) = 100
    c: Coincident(g75,g74)
    c: Coincident(g75,g62)
    c: Vertical(g75)
    c: Distance(g75) = 3
    c: Coincident(g76,g62)
    c: Vertical(g76)
    c: Distance(g76) = 3
    c: Coincident(g77,g76)
    c: Coincident(g77,g45)
    c: Horizontal(g77)
    c: Distance(g77) = 42.95
    c: Coincident(g78,g39)
    c: Coincident(g78,g48)
    c: Horizontal(g78)
    c: Distance(g78) = 42.95
    c: Coincident(g79,g39)
    c: Coincident(g79,g9)
    c: Vertical(g79)
    c: Distance(g79) = 93.16
    c: Coincident(g80,g9)
    c: Coincident(g80,g69)
    c: Angle(g80) = 0.693245
    c: Block(g80)
    c: Coincident(g81,g69)
    c: Coincident(g81,g70)
    c: Block(g81)
    c: Coincident(g82,g70)
    c: Coincident(g82,g71)
    c: Block(g82)
    c: Coincident(g83,g71)
    c: Coincident(g83,g33)
    c: Block(g71)
    c: Coincident(g84,g33)
    c: Coincident(g84,g67)
    c: Coincident(g85,g67)
    c: Coincident(g85,g66)
    c: Coincident(g86,g66)
    c: Coincident(g86,g68)
    c: Coincident(g87,g68)
    c: Coincident(g87,g21)
    c: Coincident(g88,g15)
    c: Coincident(g89,g88)
    c: Block(g89)
    c: Coincident(g90,g89)
    c: Block(g90)
    c: Block(g91)
    c: Coincident(g92,g91)
    c: Block(g92)
    c: Coincident(g93,g91)
    c: Coincident(g93,g90)
    c: Block(g93)
    c: Coincident(g94,g92)
    c: Coincident(g94,g27)
    c: Coincident(g95,g27)
    c: Block(g95)
    c: Coincident(g96,g95)
    c: Coincident(g97,g96)
    c: Coincident(g98,g97)
    c: Coincident(g99,g98)
    c: Coincident(g99,g72)
    c: Block(g98)
    c: Block(g96)
    c: Block(g72)
    c: Coincident(g100,g72)
    c: Coincident(g100,g3)
    c: Coincident(g101,g3)
    c: Coincident(g101,g45)
    c: Vertical(g101)
    c: Coincident(g118,g21)
    c: Weight(g102) = 1
    c: Equal(g102, g103-g117) x15
    c: Coincident(g118,g15)
    c: InternalAlignment(g102-g117 -> g118) x16
    c: InternalAlignment(g119-g132 -> g118) x14
    c: Block(g118)
FEATURE [Sketcher::SketchObject] Sketch006  label="leftSideTop"
  FullyConstrained = true
  sketch-geometry (99):
    g0: Circle CenterX=61.1495 CenterY=111.695 CenterZ=0 NormalX=0 NormalY=0 NormalZ=1 AngleXU=0 Radius=1
    g1: Circle CenterX=58.0728 CenterY=114.251 CenterZ=0 NormalX=0 NormalY=0 NormalZ=1 AngleXU=0 Radius=1
    g2: Circle CenterX=58.0728 CenterY=110.251 CenterZ=0 NormalX=0 NormalY=0 NormalZ=1 AngleXU=0 Radius=1
    g3: BSplineCurve PolesCount=3 KnotsCount=2 Degree=2 IsPeriodic=0
    g4: GeomPoint X=61.1495 Y=111.695 Z=0
    g5: GeomPoint X=58.0728 Y=110.251 Z=0
    g6: Circle CenterX=61.5791 CenterY=89.3511 CenterZ=0 NormalX=0 NormalY=0 NormalZ=1 AngleXU=0 Radius=1
    g7: Circle CenterX=58.0728 CenterY=91.2763 CenterZ=0 NormalX=0 NormalY=0 NormalZ=1 AngleXU=0 Radius=1
    g8: Circle CenterX=58.0728 CenterY=95.2763 CenterZ=0 NormalX=0 NormalY=0 NormalZ=1 AngleXU=0 Radius=1
    g9: BSplineCurve PolesCount=3 KnotsCount=2 Degree=2 IsPeriodic=0
    g10: GeomPoint X=61.5791 Y=89.3511 Z=0
    g11: GeomPoint X=58.0728 Y=95.2763 Z=0
    g12: Circle CenterX=62.0728 CenterY=124.221 CenterZ=0 NormalX=0 NormalY=0 NormalZ=1 AngleXU=0 Radius=1
    g13: Circle CenterX=58.0728 CenterY=124.221 CenterZ=0 NormalX=0 NormalY=0 NormalZ=1 AngleXU=0 Radius=1
    g14: Circle CenterX=61.1496 CenterY=121.665 CenterZ=0 NormalX=0 NormalY=0 NormalZ=1 AngleXU=0 Radius=1
    g15: BSplineCurve PolesCount=3 KnotsCount=2 Degree=2 IsPeriodic=0
    g16: GeomPoint X=62.0728 Y=124.221 Z=0
    g17: GeomPoint X=61.1496 Y=121.665 Z=0
    g18: Circle CenterX=61.5791 CenterY=75.4095 CenterZ=0 NormalX=0 NormalY=0 NormalZ=1 AngleXU=0 Radius=1
    g19: Circle CenterX=58.0728 CenterY=77.3346 CenterZ=0 NormalX=0 NormalY=0 NormalZ=1 AngleXU=0 Radius=1
    g20: Circle CenterX=58.0728 CenterY=73.3346 CenterZ=0 NormalX=0 NormalY=0 NormalZ=1 AngleXU=0 Radius=1
    g21: BSplineCurve PolesCount=3 KnotsCount=2 Degree=2 IsPeriodic=0
    g22: GeomPoint X=61.5791 Y=75.4095 Z=0
    g23: GeomPoint X=58.0728 Y=73.3346 Z=0
    g24: Circle CenterX=2.07281 CenterY=124.221 CenterZ=0 NormalX=0 NormalY=0 NormalZ=1 AngleXU=0 Radius=1
    g25: Circle CenterX=1.57905 CenterY=122.295 CenterZ=0 NormalX=0 NormalY=0 NormalZ=1 AngleXU=0 Radius=1
    g26: BSplineCurve PolesCount=3 KnotsCount=2 Degree=2 IsPeriodic=0
    g27: GeomPoint X=2.07281 Y=124.221 Z=0
    g28: GeomPoint X=1.57905 Y=122.295 Z=0
    g29: Circle CenterX=46.0728 CenterY=124.221 CenterZ=0 NormalX=0 NormalY=0 NormalZ=1 AngleXU=0 Radius=1
    g30: Circle CenterX=46.0728 CenterY=120.221 CenterZ=0 NormalX=0 NormalY=0 NormalZ=1 AngleXU=0 Radius=1
    g31: BSplineCurve PolesCount=3 KnotsCount=2 Degree=2 IsPeriodic=0
    g32: GeomPoint X=42.0728 Y=124.221 Z=0
    g33: GeomPoint X=46.0728 Y=120.221 Z=0
    g34: Circle CenterX=46.0728 CenterY=109.865 CenterZ=0 NormalX=0 NormalY=0 NormalZ=1 AngleXU=0 Radius=1
    g35: Circle CenterX=46.0728 CenterY=105.865 CenterZ=0 NormalX=0 NormalY=0 NormalZ=1 AngleXU=0 Radius=1
    g36: Circle CenterX=42.0728 CenterY=105.865 CenterZ=0 NormalX=0 NormalY=0 NormalZ=1 AngleXU=0 Radius=1
    g37: BSplineCurve PolesCount=3 KnotsCount=2 Degree=2 IsPeriodic=0
    g38: GeomPoint X=46.0728 Y=109.865 Z=0
    g39: GeomPoint X=42.0728 Y=105.865 Z=0
    g40: Circle CenterX=35.5028 CenterY=105.865 CenterZ=0 NormalX=0 NormalY=0 NormalZ=1 AngleXU=0 Radius=1
    g41: Circle CenterX=31.5028 CenterY=105.865 CenterZ=0 NormalX=0 NormalY=0 NormalZ=1 AngleXU=0 Radius=1
    g42: Circle CenterX=27.9965 CenterY=107.79 CenterZ=0 NormalX=0 NormalY=0 NormalZ=1 AngleXU=0 Radius=1
    g43: BSplineCurve PolesCount=3 KnotsCount=2 Degree=2 IsPeriodic=0
    g44: GeomPoint X=35.5028 Y=105.865 Z=0
    g45: GeomPoint X=27.9965 Y=107.79 Z=0
    g46-g50: Circle x5 (B-spline internal-alignment scaffolding for g51; pole/knot coordinates omitted)
    g51: BSplineCurve PolesCount=5 KnotsCount=3 Degree=3 IsPeriodic=0
    g52: GeomPoint X=132.072 Y=133.221 Z=0
    g53: GeomPoint X=141.072 Y=130.221 Z=0
    g54: GeomPoint X=132.072 Y=127.221 Z=0
    g55: ArcOfCircle CenterX=116.562 CenterY=52.0649 CenterZ=0 NormalX=0 NormalY=0 NormalZ=1 AngleXU=0 Radius=4.24264 StartAngle=0.283268 EndAngle=4.99566
    g56: LineSegment StartX=123.967 StartY=69.4706 StartZ=0 EndX=122.37 EndY=67.5474 EndZ=0
    g57: LineSegment StartX=117.293 StartY=71.7641 StartZ=0 EndX=115.591 EndY=69.7147 EndZ=0
    g58: LineSegment StartX=120.669 StartY=65.4973 StartZ=0 EndX=119.072 EndY=63.5741 EndZ=0
    g59: LineSegment StartX=124.73 StartY=54.6766 StartZ=0 EndX=123.265 EndY=51.8068 EndZ=0
    g60: LineSegment StartX=120.377 StartY=46.5474 StartZ=0 EndX=118.934 EndY=43.9178 EndZ=0
    g61: BSplineCurve PolesCount=3 KnotsCount=2 Degree=2 IsPeriodic=0
    g62: BSplineCurve PolesCount=3 KnotsCount=2 Degree=2 IsPeriodic=0
    g63: LineSegment StartX=61.5791 StartY=75.4095 StartZ=0 EndX=118.934 EndY=43.9178 EndZ=0
    g64: LineSegment StartX=117.748 StartY=47.9913 StartZ=0 EndX=120.377 EndY=46.5474 EndZ=0
    g65: LineSegment StartX=120.635 StartY=53.2507 StartZ=0 EndX=123.265 EndY=51.8068 EndZ=0
    g66: LineSegment StartX=124.73 StartY=54.6766 StartZ=0 EndX=61.5791 EndY=89.3511 EndZ=0
    g67: LineSegment StartX=58.0728 StartY=95.2763 StartZ=0 EndX=58.0728 EndY=110.251 EndZ=0
    g68: LineSegment StartX=61.1495 StartY=111.695 StartZ=0 EndX=119.072 EndY=63.5741 EndZ=0
    g69: LineSegment StartX=120.669 StartY=65.4973 StartZ=0 EndX=115.591 EndY=69.7147 EndZ=0
    g70: LineSegment StartX=117.293 StartY=71.7641 StartZ=0 EndX=122.37 EndY=67.5474 EndZ=0
    g71: LineSegment StartX=123.967 StartY=69.4706 StartZ=0 EndX=61.1496 EndY=121.665 EndZ=0
    g72: LineSegment StartX=62.0728 StartY=124.221 StartZ=0 EndX=132.072 EndY=124.221 EndZ=0
    g73: LineSegment StartX=132.072 StartY=127.221 StartZ=0 EndX=132.072 EndY=124.221 EndZ=0
    g74: LineSegment StartX=132.072 StartY=133.221 StartZ=0 EndX=132.072 EndY=136.221 EndZ=0
    g75: LineSegment StartX=132.072 StartY=136.221 StartZ=0 EndX=-42.9272 EndY=136.221 EndZ=0
    g76: LineSegment StartX=2.07281 StartY=124.221 StartZ=0 EndX=42.0728 EndY=124.221 EndZ=0
    g77: LineSegment StartX=46.0728 StartY=120.221 StartZ=0 EndX=46.0728 EndY=109.865 EndZ=0
    g78: LineSegment StartX=42.0728 StartY=105.865 StartZ=0 EndX=35.5028 EndY=105.865 EndZ=0
    g79: LineSegment StartX=27.9965 StartY=107.79 StartZ=0 EndX=1.57905 EndY=122.295 EndZ=0
    g80: LineSegment StartX=-6.92718 StartY=76.4095 StartZ=0 EndX=42.0728 EndY=76.4095 EndZ=0
    g81: LineSegment StartX=-17.9272 StartY=48.2206 StartZ=0 EndX=-17.9272 EndY=58.2206 EndZ=0
    g82: LineSegment StartX=-35.9272 StartY=48.2206 StartZ=0 EndX=-35.9272 EndY=52.2206 EndZ=0
    g83: LineSegment StartX=-29.9272 StartY=48.2206 StartZ=0 EndX=-29.9272 EndY=52.2206 EndZ=0
    g84: LineSegment StartX=-23.9272 StartY=48.2206 StartZ=0 EndX=-23.9272 EndY=58.2206 EndZ=0
    g85: ArcOfCircle CenterX=-32.9272 CenterY=55.2206 CenterZ=0 NormalX=0 NormalY=0 NormalZ=1 AngleXU=0 Radius=4.24264 StartAngle=5.49779 EndAngle=10.2102
    g86: ArcOfCircle CenterX=-20.9272 CenterY=61.2206 CenterZ=0 NormalX=0 NormalY=0 NormalZ=1 AngleXU=0 Radius=4.24264 StartAngle=5.49779 EndAngle=10.2102
    g87: LineSegment StartX=-10.9272 StartY=48.2206 StartZ=0 EndX=-10.9272 EndY=72.4095 EndZ=0
    g88: LineSegment StartX=-42.9272 StartY=48.2206 StartZ=0 EndX=-42.9272 EndY=136.221 EndZ=0
    g89: LineSegment StartX=46.0728 StartY=72.4095 StartZ=0 EndX=46.0728 EndY=-27.5905 EndZ=0
    g90: LineSegment StartX=58.0728 StartY=-27.5905 StartZ=0 EndX=58.0728 EndY=73.3346 EndZ=0
    g91: LineSegment StartX=50.0728 StartY=-27.5905 StartZ=0 EndX=50.0728 EndY=-31.5905 EndZ=0
    g92: LineSegment StartX=54.0728 StartY=-27.5905 StartZ=0 EndX=54.0728 EndY=-31.5905 EndZ=0
    g93: ArcOfCircle CenterX=52.0728 CenterY=-33.5905 CenterZ=0 NormalX=0 NormalY=0 NormalZ=1 AngleXU=0 Radius=2.82843 StartAngle=2.35619 EndAngle=7.06858
    g94: LineSegment StartX=46.0728 StartY=-27.5905 StartZ=0 EndX=50.0728 EndY=-27.5905 EndZ=0
    g95: LineSegment StartX=54.0728 StartY=-27.5905 StartZ=0 EndX=58.0728 EndY=-27.5905 EndZ=0
    g96: LineSegment StartX=-17.9272 StartY=48.2206 StartZ=0 EndX=-10.9272 EndY=48.2206 EndZ=0
    g97: LineSegment StartX=-29.9272 StartY=48.2206 StartZ=0 EndX=-23.9272 EndY=48.2206 EndZ=0
    g98: LineSegment StartX=-42.9272 StartY=48.2206 StartZ=0 EndX=-35.9272 EndY=48.2206 EndZ=0
  constraints (172):
    c: Weight(g0) = 1
    c: Equal(g0,g1)
    c: Equal(g0,g2)
    c: InternalAlignment(g0,g3)
    c: InternalAlignment(g1,g3)
    c: InternalAlignment(g2,g3)
    c: InternalAlignment(g4,g3)
    c: InternalAlignment(g5,g3)
    c: Weight(g6) = 1
    c: Equal(g6,g7)
    c: Equal(g6,g8)
    c: InternalAlignment(g6,g9)
    c: InternalAlignment(g7,g9)
    c: InternalAlignment(g8,g9)
    c: InternalAlignment(g10,g9)
    c: InternalAlignment(g11,g9)
    c: Block(g3)
    c: Block(g9)
    c: Weight(g12) = 1
    c: Equal(g12,g13)
    c: Equal(g12,g14)
    c: InternalAlignment(g12,g15)
    c: InternalAlignment(g13,g15)
    c: InternalAlignment(g14,g15)
    c: InternalAlignment(g16,g15)
    c: InternalAlignment(g17,g15)
    c: Block(g15)
    c: Weight(g18) = 1
    c: Equal(g18,g19)
    c: Equal(g18,g20)
    c: InternalAlignment(g18,g21)
    c: InternalAlignment(g19,g21)
    c: InternalAlignment(g20,g21)
    c: InternalAlignment(g22,g21)
    c: InternalAlignment(g23,g21)
    c: Block(g21)
    c: Weight(g24) = 1
    c: Equal(g24,g25)
    c: InternalAlignment(g24,g26)
    c: InternalAlignment(g25,g26)
    c: InternalAlignment(g27,g26)
    c: InternalAlignment(g28,g26)
    c: InternalAlignment(g29,g31)
    c: InternalAlignment(g30,g31)
    c: InternalAlignment(g32,g31)
    c: InternalAlignment(g33,g31)
    c: Weight(g34) = 1
    c: Equal(g34,g35)
    c: Equal(g34,g36)
    c: InternalAlignment(g34,g37)
    c: InternalAlignment(g35,g37)
    c: InternalAlignment(g36,g37)
    c: InternalAlignment(g38,g37)
    c: InternalAlignment(g39,g37)
    c: Equal(g40,g41)
    c: Equal(g40,g42)
    c: InternalAlignment(g40,g43)
    c: InternalAlignment(g41,g43)
    c: InternalAlignment(g42,g43)
    c: InternalAlignment(g44,g43)
    c: InternalAlignment(g45,g43)
    c: Block(g31)
    c: Block(g37)
    c: Block(g43)
    c: Block(g26)
    c: Weight(g46) = 1
    c: Equal(g46, g47-g50) x4
    c: InternalAlignment(g46-g50 -> g51) x5
    c: InternalAlignment(g52,g51)
    c: InternalAlignment(g53,g51)
    c: InternalAlignment(g54,g51)
    c: Block(g51)
    c: Block(g55)
    c: Block(g56)
    c: Block(g57)
    c: Block(g58)
    c: Block(g59)
    c: Block(g60)
    c: Block(g61)
    c: Block(g62)
    c: Coincident(g90,g21)
    c: Coincident(g63,g21)
    c: Coincident(g63,g60)
    c: Coincident(g64,g55)
    c: Coincident(g64,g60)
    c: Coincident(g65,g55)
    c: Coincident(g65,g59)
    c: Coincident(g66,g59)
    c: Coincident(g66,g9)
    c: Coincident(g67,g9)
    c: Coincident(g67,g3)
    c: Vertical(g67)
    c: Coincident(g68,g3)
    c: Coincident(g68,g58)
    c: Coincident(g69,g58)
    c: Coincident(g69,g57)
    c: Coincident(g70,g57)
    c: Coincident(g70,g56)
    c: Coincident(g71,g56)
    c: Coincident(g71,g15)
    c: Coincident(g72,g15)
    c: Horizontal(g72)
    c: Coincident(g73,g51)
    c: Coincident(g73,g72)
    c: Vertical(g73)
    c: Coincident(g74,g51)
    c: Vertical(g74)
    c: Coincident(g75,g74)
    c: Horizontal(g75)
    c: Coincident(g76,g26)
    c: Coincident(g76,g31)
    c: Horizontal(g76)
    c: Coincident(g77,g31)
    c: Coincident(g77,g37)
    c: Vertical(g77)
    c: Coincident(g78,g37)
    c: Coincident(g78,g43)
    c: Horizontal(g78)
    c: Coincident(g79,g43)
    c: Coincident(g79,g26)
    c: Coincident(g80,g62)
    c: Coincident(g80,g61)
    c: Horizontal(g80)
    c: Vertical(g81)
    c: Distance(g81) = 10
    c: Vertical(g82)
    c: Distance(g82) = 4
    c: Vertical(g83)
    c: Distance(g83) = 4
    c: Vertical(g84)
    c: Distance(g84) = 10
    c: Coincident(g85,g83)
    c: Coincident(g85,g82)
    c: Block(g85)
    c: Coincident(g86,g84)
    c: Coincident(g86,g81)
    c: Block(g86)
    c: Coincident(g87,g62)
    c: Vertical(g87)
    c: Coincident(g88,g75)
    c: Vertical(g88)
    c: Block(g75)
    c: Coincident(g89,g61)
    c: Vertical(g89)
    c: Distance(g89) = 100
    c: Block(g90)
    c: Vertical(g91)
    c: Distance(g91) = 4
    c: Vertical(g92)
    c: Distance(g92) = 4
    c: Coincident(g93,g91)
    c: Coincident(g93,g92)
    c: Block(g93)
    c: Coincident(g94,g89)
    c: Coincident(g94,g91)
    c: Horizontal(g94)
    c: Distance(g94) = 4
    c: Coincident(g95,g92)
    c: Coincident(g95,g90)
    c: Horizontal(g95)
    c: Distance(g95) = 4
    c: Block(g87)
    c: Block(g88)
    c: Coincident(g96,g81)
    c: Coincident(g96,g87)
    c: Horizontal(g96)
    c: Coincident(g97,g83)
    c: Coincident(g97,g84)
    c: Horizontal(g97)
    c: Coincident(g98,g88)
    c: Coincident(g98,g82)
    c: Horizontal(g98)
FEATURE [Sketcher::SketchObject] Sketch007  label="leftSideBottom"
  FullyConstrained = true
  sketch-geometry (92):
    g0: ArcOfCircle CenterX=-26.9272 CenterY=-83.7794 CenterZ=0 NormalX=0 NormalY=0 NormalZ=1 AngleXU=0 Radius=8 StartAngle=3.14159 EndAngle=6.28319
    g1: Circle CenterX=61.5791 CenterY=-56.9099 CenterZ=0 NormalX=0 NormalY=0 NormalZ=1 AngleXU=0 Radius=1
    g2: Circle CenterX=58.0728 CenterY=-58.8351 CenterZ=0 NormalX=0 NormalY=0 NormalZ=1 AngleXU=0 Radius=1
    g3: Circle CenterX=58.0728 CenterY=-62.8351 CenterZ=0 NormalX=0 NormalY=0 NormalZ=1 AngleXU=0 Radius=1
    g4: BSplineCurve PolesCount=3 KnotsCount=2 Degree=2 IsPeriodic=0
    g5: GeomPoint X=61.5791 Y=-56.9099 Z=0
    g6: GeomPoint X=58.0728 Y=-62.8351 Z=0
    g7: Circle CenterX=58.0728 CenterY=-77.8102 CenterZ=0 NormalX=0 NormalY=0 NormalZ=1 AngleXU=0 Radius=1
    g8: Circle CenterX=58.0728 CenterY=-81.8102 CenterZ=0 NormalX=0 NormalY=0 NormalZ=1 AngleXU=0 Radius=1
    g9: Circle CenterX=61.1496 CenterY=-79.2541 CenterZ=0 NormalX=0 NormalY=0 NormalZ=1 AngleXU=0 Radius=1
    g10: BSplineCurve PolesCount=3 KnotsCount=2 Degree=2 IsPeriodic=0
    g11: GeomPoint X=58.0728 Y=-77.8102 Z=0
    g12: GeomPoint X=61.1496 Y=-79.2541 Z=0
    g13: Circle CenterX=61.6457 CenterY=-88.8112 CenterZ=0 NormalX=0 NormalY=0 NormalZ=1 AngleXU=0 Radius=1
    g14: Circle CenterX=58.0728 CenterY=-91.7794 CenterZ=0 NormalX=0 NormalY=0 NormalZ=1 AngleXU=0 Radius=1
    g15: Circle CenterX=63.9135 CenterY=-91.8014 CenterZ=0 NormalX=0 NormalY=0 NormalZ=1 AngleXU=0 Radius=1
    g16: BSplineCurve PolesCount=3 KnotsCount=2 Degree=2 IsPeriodic=0
    g17: GeomPoint X=61.6457 Y=-88.8112 Z=0
    g18: GeomPoint X=63.9135 Y=-91.8014 Z=0
    g19: Circle CenterX=58.0728 CenterY=-40.8935 CenterZ=0 NormalX=0 NormalY=0 NormalZ=1 AngleXU=0 Radius=1
    g20: Circle CenterX=58.0728 CenterY=-44.8935 CenterZ=0 NormalX=0 NormalY=0 NormalZ=1 AngleXU=0 Radius=1
    g21: Circle CenterX=61.5791 CenterY=-42.9683 CenterZ=0 NormalX=0 NormalY=0 NormalZ=1 AngleXU=0 Radius=1
    g22: BSplineCurve PolesCount=3 KnotsCount=2 Degree=2 IsPeriodic=0
    g23: GeomPoint X=58.0728 Y=-40.8935 Z=0
    g24: GeomPoint X=61.5791 Y=-42.9683 Z=0
    g25: Circle CenterX=42.5666 CenterY=-67.3492 CenterZ=0 NormalX=0 NormalY=0 NormalZ=1 AngleXU=0 Radius=1
    g26: Circle CenterX=46.0728 CenterY=-65.424 CenterZ=0 NormalX=0 NormalY=0 NormalZ=1 AngleXU=0 Radius=1
    g27: Circle CenterX=46.0728 CenterY=-69.424 CenterZ=0 NormalX=0 NormalY=0 NormalZ=1 AngleXU=0 Radius=1
    g28: BSplineCurve PolesCount=3 KnotsCount=2 Degree=2 IsPeriodic=0
    g29: GeomPoint X=42.5666 Y=-67.3492 Z=0
    g30: GeomPoint X=46.0728 Y=-69.424 Z=0
    g31: Circle CenterX=2.07281 CenterY=-91.7794 CenterZ=0 NormalX=0 NormalY=0 NormalZ=1 AngleXU=0 Radius=1
    g32: Circle CenterX=-1.92719 CenterY=-91.7794 CenterZ=0 NormalX=0 NormalY=0 NormalZ=1 AngleXU=0 Radius=1
    g33: Circle CenterX=1.57905 CenterY=-89.8542 CenterZ=0 NormalX=0 NormalY=0 NormalZ=1 AngleXU=0 Radius=1
    g34: BSplineCurve PolesCount=3 KnotsCount=2 Degree=2 IsPeriodic=0
    g35: GeomPoint X=2.07281 Y=-91.7794 Z=0
    g36: GeomPoint X=1.57905 Y=-89.8542 Z=0
    g37: ArcOfCircle CenterX=-26.9272 CenterY=22.1087 CenterZ=0 NormalX=0 NormalY=0 NormalZ=1 AngleXU=0 Radius=4 StartAngle=5e-16 EndAngle=3.14159
    g38: Circle CenterX=-10.9272 CenterY=-78.7794 CenterZ=0 NormalX=0 NormalY=0 NormalZ=1 AngleXU=0 Radius=1
    g39: Circle CenterX=-10.9272 CenterY=-82.7794 CenterZ=0 NormalX=0 NormalY=0 NormalZ=1 AngleXU=0 Radius=1
    g40: Circle CenterX=-7.42095 CenterY=-80.8542 CenterZ=0 NormalX=0 NormalY=0 NormalZ=1 AngleXU=0 Radius=1
    g41: BSplineCurve PolesCount=3 KnotsCount=2 Degree=2 IsPeriodic=0
    g42: GeomPoint X=-10.9272 Y=-78.7794 Z=0
    g43: GeomPoint X=-7.42095 Y=-80.8542 Z=0
    g44: BSplineCurve PolesCount=3 KnotsCount=2 Degree=2 IsPeriodic=0
    g45: GeomPoint X=42.5666 Y=-53.4075 Z=0
    g46: GeomPoint X=46.0728 Y=-47.4823 Z=0
    g47: BSplineCurve PolesCount=5 KnotsCount=3 Degree=3 IsPeriodic=0
    g48: LineSegment StartX=124.814 StartY=-22.1885 StartZ=0 EndX=123.265 EndY=-19.3655 EndZ=0
    g49: ArcOfCircle CenterX=116.562 CenterY=-19.6236 CenterZ=0 NormalX=0 NormalY=0 NormalZ=1 AngleXU=0 Radius=4.24264 StartAngle=1.28753 EndAngle=6.00037
    g50: LineSegment StartX=-30.9272 StartY=22.1087 StartZ=0 EndX=-34.9272 EndY=-83.7794 EndZ=0
    g51: LineSegment StartX=-22.9272 StartY=22.1087 StartZ=0 EndX=-18.9272 EndY=-83.7794 EndZ=0
    g52: LineSegment StartX=118.934 StartY=-11.4765 StartZ=0 EndX=120.377 EndY=-14.1062 EndZ=0
    g53: LineSegment StartX=118.86 StartY=-31.3104 StartZ=0 EndX=120.377 EndY=-33.1447 EndZ=0
    g54: LineSegment StartX=115.291 StartY=-37.3514 StartZ=0 EndX=117.05 EndY=-39.4781 EndZ=0
    g55: LineSegment StartX=122.136 StartY=-35.2714 StartZ=0 EndX=123.656 EndY=-37.1092 EndZ=0
    g56: BSplineCurve PolesCount=3 KnotsCount=2 Degree=2 IsPeriodic=0
    g57: LineSegment StartX=132.072 StartY=-100.779 StartZ=0 EndX=132.072 EndY=-103.779 EndZ=0
    g58: LineSegment StartX=132.072 StartY=-91.8014 StartZ=0 EndX=132.072 EndY=-94.7791 EndZ=0
    g59: LineSegment StartX=63.9135 StartY=-91.8014 StartZ=0 EndX=132.072 EndY=-91.8014 EndZ=0
    g60: LineSegment StartX=61.6457 StartY=-88.8112 StartZ=0 EndX=123.656 EndY=-37.1092 EndZ=0
    g61: LineSegment StartX=122.136 StartY=-35.2714 StartZ=0 EndX=117.05 EndY=-39.4781 EndZ=0
    g62: LineSegment StartX=115.291 StartY=-37.3514 StartZ=0 EndX=120.377 EndY=-33.1447 EndZ=0
    g63: LineSegment StartX=118.86 StartY=-31.3104 StartZ=0 EndX=61.1496 EndY=-79.2541 EndZ=0
    g64: LineSegment StartX=58.0728 StartY=-77.8102 StartZ=0 EndX=58.0728 EndY=-62.8351 EndZ=0
    g65: LineSegment StartX=61.5791 StartY=-56.9099 StartZ=0 EndX=124.814 EndY=-22.1885 EndZ=0
    g66: LineSegment StartX=120.636 StartY=-20.8076 StartZ=0 EndX=123.265 EndY=-19.3655 EndZ=0
    g67: LineSegment StartX=117.748 StartY=-15.55 StartZ=0 EndX=120.377 EndY=-14.1062 EndZ=0
    g68: LineSegment StartX=118.934 StartY=-11.4765 StartZ=0 EndX=61.5791 EndY=-42.9683 EndZ=0
    g69: LineSegment StartX=-42.9272 StartY=-103.779 StartZ=0 EndX=132.072 EndY=-103.779 EndZ=0
    g70: LineSegment StartX=42.5666 StartY=-53.4075 StartZ=0 EndX=-7.42095 EndY=-80.8542 EndZ=0
    g71: LineSegment StartX=-10.9272 StartY=-78.7794 StartZ=0 EndX=-10.9272 EndY=48.2206 EndZ=0
    g72: LineSegment StartX=2.07281 StartY=-91.7794 StartZ=0 EndX=42.0728 EndY=-91.7794 EndZ=0
    g73: LineSegment StartX=46.0728 StartY=-87.7794 StartZ=0 EndX=46.0728 EndY=-69.424 EndZ=0
    g74: LineSegment StartX=42.5666 StartY=-67.3492 StartZ=0 EndX=1.57905 EndY=-89.8542 EndZ=0
    g75: LineSegment StartX=-42.9272 StartY=-103.779 StartZ=0 EndX=-42.9272 EndY=48.2206 EndZ=0
    g76: LineSegment StartX=-17.9272 StartY=48.2206 StartZ=0 EndX=-17.9272 EndY=58.2206 EndZ=0
    g77: LineSegment StartX=-35.9272 StartY=48.2206 StartZ=0 EndX=-35.9272 EndY=52.2206 EndZ=0
    g78: LineSegment StartX=-29.9272 StartY=48.2206 StartZ=0 EndX=-29.9272 EndY=52.2206 EndZ=0
    g79: LineSegment StartX=-23.9272 StartY=48.2206 StartZ=0 EndX=-23.9272 EndY=58.2206 EndZ=0
    g80: ArcOfCircle CenterX=-32.9272 CenterY=55.2206 CenterZ=0 NormalX=0 NormalY=0 NormalZ=1 AngleXU=0 Radius=4.24264 StartAngle=5.49779 EndAngle=10.2102
    g81: ArcOfCircle CenterX=-20.9272 CenterY=61.2206 CenterZ=0 NormalX=0 NormalY=0 NormalZ=1 AngleXU=0 Radius=4.24264 StartAngle=5.49779 EndAngle=10.2102
    g82: LineSegment StartX=-17.9272 StartY=48.2206 StartZ=0 EndX=-10.9272 EndY=48.2206 EndZ=0
    g83: LineSegment StartX=-42.9272 StartY=48.2206 StartZ=0 EndX=-35.9272 EndY=48.2206 EndZ=0
    g84: LineSegment StartX=50.0728 StartY=-27.5905 StartZ=0 EndX=50.0728 EndY=-31.5905 EndZ=0
    g85: LineSegment StartX=54.0728 StartY=-27.5905 StartZ=0 EndX=54.0728 EndY=-31.5905 EndZ=0
    g86: ArcOfCircle CenterX=52.0728 CenterY=-33.5905 CenterZ=0 NormalX=0 NormalY=0 NormalZ=1 AngleXU=0 Radius=2.82843 StartAngle=2.35619 EndAngle=7.06858
    g87: LineSegment StartX=46.0728 StartY=-27.5905 StartZ=0 EndX=50.0728 EndY=-27.5905 EndZ=0
    g88: LineSegment StartX=54.0728 StartY=-27.5905 StartZ=0 EndX=58.0728 EndY=-27.5905 EndZ=0
    g89: LineSegment StartX=46.0728 StartY=-27.5905 StartZ=0 EndX=46.0728 EndY=-47.4823 EndZ=0
    g90: LineSegment StartX=58.0728 StartY=-27.5905 StartZ=0 EndX=58.0728 EndY=-40.8935 EndZ=0
    g91: LineSegment StartX=-29.9272 StartY=48.2206 StartZ=0 EndX=-23.9272 EndY=48.2206 EndZ=0
  constraints (170):
    c: Weight(g1) = 1
    c: Equal(g1,g2)
    c: Equal(g1,g3)
    c: InternalAlignment(g1,g4)
    c: InternalAlignment(g2,g4)
    c: InternalAlignment(g3,g4)
    c: InternalAlignment(g5,g4)
    c: InternalAlignment(g6,g4)
    c: Weight(g7) = 1
    c: Equal(g7,g8)
    c: Equal(g7,g9)
    c: InternalAlignment(g7,g10)
    c: InternalAlignment(g8,g10)
    c: InternalAlignment(g9,g10)
    c: InternalAlignment(g11,g10)
    c: InternalAlignment(g12,g10)
    c: Block(g4)
    c: Block(g10)
    c: Weight(g13) = 1
    c: Equal(g13,g14)
    c: Equal(g13,g15)
    c: InternalAlignment(g13,g16)
    c: InternalAlignment(g14,g16)
    c: InternalAlignment(g15,g16)
    c: InternalAlignment(g17,g16)
    c: InternalAlignment(g18,g16)
    c: Block(g16)
    c: Weight(g19) = 1
    c: Equal(g19,g20)
    c: Equal(g19,g21)
    c: InternalAlignment(g19,g22)
    c: InternalAlignment(g20,g22)
    c: InternalAlignment(g21,g22)
    c: InternalAlignment(g23,g22)
    c: InternalAlignment(g24,g22)
    c: Block(g22)
    c: Weight(g25) = 1
    c: Equal(g25,g26)
    c: Equal(g25,g27)
    c: InternalAlignment(g25,g28)
    c: InternalAlignment(g26,g28)
    c: InternalAlignment(g27,g28)
    c: InternalAlignment(g29,g28)
    c: InternalAlignment(g30,g28)
    c: Weight(g31) = 1
    c: Equal(g31,g32)
    c: Equal(g31,g33)
    c: InternalAlignment(g31,g34)
    c: InternalAlignment(g32,g34)
    c: InternalAlignment(g33,g34)
    c: InternalAlignment(g35,g34)
    c: InternalAlignment(g36,g34)
    c: Block(g34)
    c: Block(g28)
    c: Block(g37)
    c: Block(g0)
    c: Weight(g38) = 1
    c: Equal(g38,g40)
    c: InternalAlignment(g38,g41)
    c: InternalAlignment(g39,g41)
    c: InternalAlignment(g40,g41)
    c: InternalAlignment(g42,g41)
    c: InternalAlignment(g43,g41)
    c: InternalAlignment(g45,g44)
    c: InternalAlignment(g46,g44)
    c: Block(g47)
    c: Block(g44)
    c: Block(g41)
    c: Block(g48)
    c: Block(g49)
    c: Coincident(g50,g37)
    c: Coincident(g50,g0)
    c: Coincident(g51,g37)
    c: Coincident(g51,g0)
    c: Block(g51)
    c: Block(g50)
    c: Block(g52)
    c: Block(g53)
    c: Block(g54)
    c: Block(g55)
    c: Block(g56)
    c: Coincident(g57,g47)
    c: Vertical(g57)
    c: Coincident(g58,g47)
    c: Vertical(g58)
    c: Coincident(g59,g16)
    c: Coincident(g59,g58)
    c: Horizontal(g59)
    c: Coincident(g60,g16)
    c: Coincident(g60,g55)
    c: Coincident(g61,g55)
    c: Coincident(g61,g54)
    c: Coincident(g62,g54)
    c: Coincident(g62,g53)
    c: Coincident(g63,g53)
    c: Coincident(g63,g10)
    c: Coincident(g64,g10)
    c: Coincident(g64,g4)
    c: Vertical(g64)
    c: Coincident(g65,g4)
    c: Coincident(g65,g48)
    c: Coincident(g66,g49)
    c: Coincident(g66,g48)
    c: Coincident(g67,g49)
    c: Coincident(g67,g52)
    c: Coincident(g68,g52)
    c: Coincident(g68,g22)
    c: Coincident(g69,g57)
    c: Horizontal(g69)
    c: Coincident(g70,g44)
    c: Coincident(g70,g41)
    c: Coincident(g71,g41)
    c: Vertical(g71)
    c: Coincident(g72,g34)
    c: Coincident(g72,g56)
    c: Horizontal(g72)
    c: Coincident(g73,g56)
    c: Coincident(g73,g28)
    c: Vertical(g73)
    c: Coincident(g74,g28)
    c: Coincident(g74,g34)
    c: Block(g69)
    c: Coincident(g75,g69)
    c: Vertical(g75)
    c: Distance(g75) = 152
    c: Block(g71)
    c: Vertical(g76)
    c: Distance(g76) = 10
    c: Vertical(g77)
    c: Distance(g77) = 4
    c: Vertical(g78)
    c: Distance(g78) = 4
    c: Vertical(g79)
    c: Distance(g79) = 10
    c: Coincident(g80,g78)
    c: Coincident(g80,g77)
    c: Block(g80)
    c: Coincident(g81,g79)
    c: Coincident(g81,g76)
    c: Block(g81)
    c: Coincident(g82,g76)
    c: Coincident(g82,g71)
    c: Horizontal(g82)
    c: Coincident(g83,g75)
    c: Coincident(g83,g77)
    c: Horizontal(g83)
    c: Distance(g83) = 7
    c: Distance(g82) = 7
    c: Vertical(g84)
    c: Distance(g84) = 4
    c: Vertical(g85)
    c: Distance(g85) = 4
    c: Coincident(g86,g84)
    c: Coincident(g86,g85)
    c: Block(g86)
    c: Coincident(g87,g84)
    c: Horizontal(g87)
    c: Distance(g87) = 4
    c: Coincident(g88,g85)
    c: Horizontal(g88)
    c: Distance(g88) = 4
    c: Coincident(g89,g87)
    c: Coincident(g89,g44)
    c: Vertical(g89)
    c: Coincident(g90,g88)
    c: Coincident(g90,g22)
    c: Vertical(g90)
    c: Coincident(g91,g78)
    c: Coincident(g91,g79)
    c: Horizontal(g91)
FEATURE [Sketcher::SketchObject] Sketch008  label="rightSideTop"
  FullyConstrained = false
  sketch-geometry (108):
    g0: Circle CenterX=302.996 CenterY=111.695 CenterZ=0 NormalX=0 NormalY=0 NormalZ=1 AngleXU=0 Radius=1
    g1: Circle CenterX=306.073 CenterY=114.251 CenterZ=0 NormalX=0 NormalY=0 NormalZ=1 AngleXU=0 Radius=1
    g2: Circle CenterX=306.073 CenterY=110.251 CenterZ=0 NormalX=0 NormalY=0 NormalZ=1 AngleXU=0 Radius=1
    g3: BSplineCurve PolesCount=3 KnotsCount=2 Degree=2 IsPeriodic=0
    g4: GeomPoint X=302.996 Y=111.695 Z=0
    g5: GeomPoint X=306.073 Y=110.251 Z=0
    g6: Circle CenterX=306.073 CenterY=95.2763 CenterZ=0 NormalX=0 NormalY=0 NormalZ=1 AngleXU=0 Radius=1
    g7: Circle CenterX=306.073 CenterY=91.2763 CenterZ=0 NormalX=0 NormalY=0 NormalZ=1 AngleXU=0 Radius=1
    g8: Circle CenterX=302.567 CenterY=89.3511 CenterZ=0 NormalX=0 NormalY=0 NormalZ=1 AngleXU=0 Radius=1
    g9: BSplineCurve PolesCount=3 KnotsCount=2 Degree=2 IsPeriodic=0
    g10: GeomPoint X=306.073 Y=95.2763 Z=0
    g11: GeomPoint X=302.567 Y=89.3511 Z=0
    g12: LineSegment StartX=306.073 StartY=110.251 StartZ=0 EndX=306.073 EndY=95.2763 EndZ=0
    g13: Circle CenterX=302.073 CenterY=124.221 CenterZ=0 NormalX=0 NormalY=0 NormalZ=1 AngleXU=0 Radius=1
    g14: Circle CenterX=306.073 CenterY=124.221 CenterZ=0 NormalX=0 NormalY=0 NormalZ=1 AngleXU=0 Radius=1
    g15: Circle CenterX=302.996 CenterY=121.665 CenterZ=0 NormalX=0 NormalY=0 NormalZ=1 AngleXU=0 Radius=1
    g16: BSplineCurve PolesCount=3 KnotsCount=2 Degree=2 IsPeriodic=0
    g17: GeomPoint X=302.073 Y=124.221 Z=0
    g18: GeomPoint X=302.996 Y=121.665 Z=0
    g19: Circle CenterX=306.073 CenterY=73.3346 CenterZ=0 NormalX=0 NormalY=0 NormalZ=1 AngleXU=0 Radius=1
    g20: Circle CenterX=306.073 CenterY=77.3346 CenterZ=0 NormalX=0 NormalY=0 NormalZ=1 AngleXU=0 Radius=1
    g21: Circle CenterX=302.535 CenterY=75.4095 CenterZ=0 NormalX=0 NormalY=0 NormalZ=1 AngleXU=0 Radius=1
    g22: BSplineCurve PolesCount=3 KnotsCount=2 Degree=2 IsPeriodic=0
    g23: GeomPoint X=306.073 Y=73.3346 Z=0
    g24: GeomPoint X=302.535 Y=75.4095 Z=0
    g25: Circle CenterX=362.073 CenterY=124.221 CenterZ=0 NormalX=0 NormalY=0 NormalZ=1 AngleXU=0 Radius=1
    g26: Circle CenterX=366.073 CenterY=124.221 CenterZ=0 NormalX=0 NormalY=0 NormalZ=1 AngleXU=0 Radius=1
    g27: Circle CenterX=362.567 CenterY=122.294 CenterZ=0 NormalX=0 NormalY=0 NormalZ=1 AngleXU=0 Radius=1
    g28: BSplineCurve PolesCount=3 KnotsCount=2 Degree=2 IsPeriodic=0
    g29: GeomPoint X=362.073 Y=124.221 Z=0
    g30: GeomPoint X=362.567 Y=122.294 Z=0
    g31: Circle CenterX=322.073 CenterY=124.221 CenterZ=0 NormalX=0 NormalY=0 NormalZ=1 AngleXU=0 Radius=1
    g32: Circle CenterX=318.073 CenterY=124.221 CenterZ=0 NormalX=0 NormalY=0 NormalZ=1 AngleXU=0 Radius=1
    g33: Circle CenterX=318.073 CenterY=120.221 CenterZ=0 NormalX=0 NormalY=0 NormalZ=1 AngleXU=0 Radius=1
    g34: BSplineCurve PolesCount=3 KnotsCount=2 Degree=2 IsPeriodic=0
    g35: GeomPoint X=322.073 Y=124.221 Z=0
    g36: GeomPoint X=318.073 Y=120.221 Z=0
    g37: Circle CenterX=322.073 CenterY=105.865 CenterZ=0 NormalX=0 NormalY=0 NormalZ=1 AngleXU=0 Radius=1
    g38: Circle CenterX=318.073 CenterY=105.865 CenterZ=0 NormalX=0 NormalY=0 NormalZ=1 AngleXU=0 Radius=1
    g39: Circle CenterX=318.073 CenterY=109.865 CenterZ=0 NormalX=0 NormalY=0 NormalZ=1 AngleXU=0 Radius=1
    g40: BSplineCurve PolesCount=3 KnotsCount=2 Degree=2 IsPeriodic=0
    g41: GeomPoint X=322.073 Y=105.865 Z=0
    g42: GeomPoint X=318.073 Y=109.865 Z=0
    g43: Circle CenterX=336.157 CenterY=107.779 CenterZ=0 NormalX=0 NormalY=0 NormalZ=1 AngleXU=0 Radius=1
    g44: Circle CenterX=332.651 CenterY=105.853 CenterZ=0 NormalX=0 NormalY=0 NormalZ=1 AngleXU=0 Radius=1
    g45: Circle CenterX=328.643 CenterY=105.865 CenterZ=0 NormalX=0 NormalY=0 NormalZ=1 AngleXU=0 Radius=1
    g46: BSplineCurve PolesCount=3 KnotsCount=2 Degree=2 IsPeriodic=0
    g47: GeomPoint X=336.157 Y=107.779 Z=0
    g48: GeomPoint X=328.643 Y=105.865 Z=0
    g49: Circle CenterX=322.073 CenterY=76.4095 CenterZ=0 NormalX=0 NormalY=0 NormalZ=1 AngleXU=0 Radius=4
    g50: BSplineCurve PolesCount=3 KnotsCount=2 Degree=2 IsPeriodic=0
    g51: GeomPoint X=318.073 Y=72.4095 Z=0
    g52: GeomPoint X=322.073 Y=76.4095 Z=0
    g53: Circle CenterX=375.073 CenterY=72.4095 CenterZ=0 NormalX=0 NormalY=0 NormalZ=1 AngleXU=0 Radius=1
    g54: Circle CenterX=375.073 CenterY=76.4095 CenterZ=0 NormalX=0 NormalY=0 NormalZ=1 AngleXU=0 Radius=1
    g55: Circle CenterX=371.073 CenterY=76.4095 CenterZ=0 NormalX=0 NormalY=0 NormalZ=1 AngleXU=0 Radius=1
    g56: BSplineCurve PolesCount=3 KnotsCount=2 Degree=2 IsPeriodic=0
    g57: GeomPoint X=375.073 Y=72.4095 Z=0
    g58: GeomPoint X=371.073 Y=76.4095 Z=0
    g59: LineSegment StartX=322.073 StartY=76.4095 StartZ=0 EndX=371.073 EndY=76.4095 EndZ=0
    g60: Circle CenterX=232.072 CenterY=133.221 CenterZ=0 NormalX=0 NormalY=0 NormalZ=1 AngleXU=0 Radius=1
    g61: Circle CenterX=226.072 CenterY=136.221 CenterZ=0 NormalX=0 NormalY=0 NormalZ=1 AngleXU=0 Radius=1
    g62: Circle CenterX=226.072 CenterY=124.221 CenterZ=0 NormalX=0 NormalY=0 NormalZ=1 AngleXU=0 Radius=1
    g63: Circle CenterX=232.072 CenterY=127.221 CenterZ=0 NormalX=0 NormalY=0 NormalZ=1 AngleXU=0 Radius=1
    g64: BSplineCurve PolesCount=5 KnotsCount=3 Degree=3 IsPeriodic=0
    g65: GeomPoint X=232.072 Y=133.221 Z=0
    g66: GeomPoint X=223.072 Y=130.221 Z=0
    g67: GeomPoint X=232.072 Y=127.221 Z=0
    g68: LineSegment StartX=240.687 StartY=51.8263 StartZ=0 EndX=243.317 EndY=53.2701 EndZ=0
    g69: LineSegment StartX=243.575 StartY=46.5669 StartZ=0 EndX=246.205 EndY=48.0108 EndZ=0
    g70: ArcOfCircle CenterX=247.391 CenterY=52.0843 CenterZ=0 NormalX=0 NormalY=0 NormalZ=1 AngleXU=0 Radius=4.24264 StartAngle=4.42912 EndAngle=9.14151
    g71: LineSegment StartX=243.475 StartY=65.4951 StartZ=0 EndX=245.073 EndY=63.5726 EndZ=0
    g72: LineSegment StartX=243.575 StartY=46.5669 StartZ=0 EndX=245.072 EndY=43.8408 EndZ=0
    g73: LineSegment StartX=245.072 StartY=43.8408 StartZ=0 EndX=302.535 EndY=75.4095 EndZ=0
    g74: LineSegment StartX=239.192 StartY=54.5542 StartZ=0 EndX=302.567 EndY=89.3511 EndZ=0
    g75: LineSegment StartX=232.072 StartY=127.221 StartZ=0 EndX=232.072 EndY=124.221 EndZ=0
    g76: LineSegment StartX=232.072 StartY=136.221 StartZ=0 EndX=232.072 EndY=133.221 EndZ=0
    g77: LineSegment StartX=232.072 StartY=136.221 StartZ=0 EndX=407.073 EndY=136.221 EndZ=0
    g78: LineSegment StartX=322.073 StartY=124.221 StartZ=0 EndX=362.073 EndY=124.221 EndZ=0
    g79: LineSegment StartX=362.567 StartY=122.294 StartZ=0 EndX=336.157 EndY=107.779 EndZ=0
    g80: LineSegment StartX=322.073 StartY=105.865 StartZ=0 EndX=328.643 EndY=105.865 EndZ=0
    g81: LineSegment StartX=318.073 StartY=120.221 StartZ=0 EndX=318.073 EndY=109.865 EndZ=0
    g82: LineSegment StartX=232.072 StartY=124.221 StartZ=0 EndX=302.073 EndY=124.221 EndZ=0
    g83: LineSegment StartX=302.996 StartY=121.665 StartZ=0 EndX=240.171 EndY=69.471 EndZ=0
    g84: LineSegment StartX=240.171 StartY=69.471 StartZ=0 EndX=241.711 EndY=67.6177 EndZ=0
    g85: LineSegment StartX=241.711 StartY=67.6177 StartZ=0 EndX=246.787 EndY=71.8365 EndZ=0
    g86: LineSegment StartX=246.787 StartY=71.8365 StartZ=0 EndX=248.551 EndY=69.712 EndZ=0
    g87: LineSegment StartX=248.551 StartY=69.712 StartZ=0 EndX=243.475 EndY=65.4951 EndZ=0
    g88: LineSegment StartX=245.073 StartY=63.5726 StartZ=0 EndX=302.996 EndY=111.695 EndZ=0
    g89: LineSegment StartX=239.192 StartY=54.5542 StartZ=0 EndX=240.687 EndY=51.8263 EndZ=0
    g90: LineSegment StartX=375.073 StartY=48.2206 StartZ=0 EndX=382.073 EndY=48.2206 EndZ=0
    g91: LineSegment StartX=407.073 StartY=48.2206 StartZ=0 EndX=400.073 EndY=48.2206 EndZ=0
    g92: LineSegment StartX=394.073 StartY=48.2206 StartZ=0 EndX=394.073 EndY=52.2206 EndZ=0
    g93: LineSegment StartX=388.073 StartY=48.2206 StartZ=0 EndX=388.073 EndY=58.2206 EndZ=0
    g94: ArcOfCircle CenterX=385.073 CenterY=61.2206 CenterZ=0 NormalX=0 NormalY=0 NormalZ=1 AngleXU=0 Radius=4.24264 StartAngle=5.49779 EndAngle=10.2102
    g95: ArcOfCircle CenterX=397.073 CenterY=55.2206 CenterZ=0 NormalX=0 NormalY=0 NormalZ=1 AngleXU=0 Radius=4.24264 StartAngle=5.49779 EndAngle=10.2102
    g96: LineSegment StartX=382.073 StartY=58.2206 StartZ=0 EndX=382.073 EndY=48.2206 EndZ=0
    g97: LineSegment StartX=400.073 StartY=52.2206 StartZ=0 EndX=400.073 EndY=48.2206 EndZ=0
    g98: LineSegment StartX=394.073 StartY=48.2206 StartZ=0 EndX=388.073 EndY=48.2206 EndZ=0
    g99: LineSegment StartX=306.073 StartY=-27.5935 StartZ=0 EndX=310.073 EndY=-27.5935 EndZ=0
    g100: LineSegment StartX=318.073 StartY=-27.5935 StartZ=0 EndX=314.073 EndY=-27.5935 EndZ=0
    g101: LineSegment StartX=310.073 StartY=-27.5935 StartZ=0 EndX=310.073 EndY=-31.5935 EndZ=0
    g102: LineSegment StartX=314.073 StartY=-27.5935 StartZ=0 EndX=314.073 EndY=-31.5935 EndZ=0
    g103: ArcOfCircle CenterX=312.073 CenterY=-33.5935 CenterZ=0 NormalX=0 NormalY=0 NormalZ=1 AngleXU=0 Radius=2.82843 StartAngle=2.35619 EndAngle=7.06858
    g104: LineSegment StartX=375.073 StartY=72.4095 StartZ=0 EndX=375.073 EndY=48.2206 EndZ=0
    g105: LineSegment StartX=407.073 StartY=48.2206 StartZ=0 EndX=407.073 EndY=136.221 EndZ=0
    g106: LineSegment StartX=318.073 StartY=-27.5935 StartZ=0 EndX=318.073 EndY=72.4095 EndZ=0
    g107: LineSegment StartX=306.073 StartY=73.3346 StartZ=0 EndX=306.073 EndY=-27.5935 EndZ=0
  constraints (136):
    c: Weight(g0) = 1
    c: Equal(g0,g1)
    c: Equal(g0,g2)
    c: InternalAlignment(g0,g3)
    c: InternalAlignment(g1,g3)
    c: InternalAlignment(g2,g3)
    c: InternalAlignment(g4,g3)
    c: InternalAlignment(g5,g3)
    c: Weight(g6) = 1
    c: Equal(g6,g7)
    c: Equal(g6,g8)
    c: InternalAlignment(g6,g9)
    c: InternalAlignment(g7,g9)
    c: InternalAlignment(g8,g9)
    c: InternalAlignment(g10,g9)
    c: InternalAlignment(g11,g9)
    c: Block(g3)
    c: Block(g9)
    c: Coincident(g12,g3)
    c: Coincident(g12,g9)
    c: Vertical(g12)
    c: Weight(g13) = 1
    c: Equal(g13,g14)
    c: Equal(g13,g15)
    c: InternalAlignment(g14,g16)
    c: InternalAlignment(g15,g16)
    c: InternalAlignment(g17,g16)
    c: InternalAlignment(g18,g16)
    c: Block(g71)
    c: Block(g72)
    c: Coincident(g73,g72)
    c: Coincident(g73,g22)
    c: Block(g73)
    c: Coincident(g70,g69)
    c: Coincident(g70,g68)
    c: Coincident(g74,g9)
    c: Block(g74)
    c: Distance(g71) = 2.5
    c: Block(g64)
    c: Block(g46)
    c: Block(g59)
    c: Coincident(g75,g64)
    c: Vertical(g75)
    c: Coincident(g76,g64)
    c: Vertical(g76)
    c: Coincident(g77,g76)
    c: Horizontal(g77)
    c: Coincident(g78,g34)
    c: Coincident(g78,g28)
    c: Horizontal(g78)
    c: Coincident(g79,g28)
    c: Coincident(g79,g46)
    c: Coincident(g80,g40)
    c: Coincident(g80,g46)
    c: Horizontal(g80)
    c: Coincident(g81,g34)
    c: Coincident(g81,g40)
    c: Vertical(g81)
    c: Block(g34)
    c: Block(g40)
    c: Block(g28)
    c: Coincident(g82,g75)
    c: Coincident(g82,g16)
    c: Horizontal(g82)
    c: Coincident(g83,g16)
    c: Block(g82)
    c: Block(g83)
    c: Block(g16)
    c: Coincident(g84,g83)
    c: Block(g84)
    c: Coincident(g85,g84)
    c: Block(g85)
    c: Coincident(g86,g85)
    c: Coincident(g87,g86)
    c: Coincident(g87,g71)
    c: Block(g87)
    c: Coincident(g88,g71)
    c: Coincident(g88,g3)
    c: Block(g88)
    c: Coincident(g89,g74)
    c: Coincident(g89,g68)
    c: Block(g70)
    c: Block(g68)
    c: Block(g69)
    c: Block(g22)
    c: Block(g50)
    c: Block(g56)
    c: Horizontal(g90)
    c: Distance(g90) = 7
    c: Horizontal(g91)
    c: Distance(g91) = 7
    c: Vertical(g92)
    c: Distance(g92) = 4
    c: Vertical(g93)
    c: Distance(g93) = 10
    c: Coincident(g94,g93)
    c: Coincident(g95,g92)
    c: Block(g95)
    c: Block(g94)
    c: Coincident(g96,g94)
    c: Coincident(g96,g90)
    c: Vertical(g96)
    c: Coincident(g97,g95)
    c: Coincident(g97,g91)
    c: Vertical(g97)
    c: Coincident(g98,g92)
    c: Coincident(g98,g93)
    c: Horizontal(g98)
    c: Horizontal(g99)
    c: Distance(g99) = 4
    c: Horizontal(g100)
    c: Distance(g100) = 4
    c: Coincident(g101,g99)
    c: Vertical(g101)
    c: Coincident(g102,g100)
    c: Vertical(g102)
    c: Distance(g101) = 4
    c: Distance(g102) = 4
    c: Coincident(g103,g101)
    c: Coincident(g103,g102)
    c: Block(g103)
    c: Coincident(g104,g56)
    c: Coincident(g104,g90)
    c: Vertical(g104)
    c: Block(g104)
    c: Coincident(g105,g91)
    c: Coincident(g105,g77)
    c: Vertical(g105)
    c: Block(g77)
    c: Block(g105)
    c: Coincident(g106,g100)
    c: Coincident(g106,g50)
    c: Vertical(g106)
    c: Coincident(g107,g22)
    c: Coincident(g107,g99)
    c: Vertical(g107)
FEATURE [Sketcher::SketchObject] Sketch009  label="middleBottom"
  FullyConstrained = true
  sketch-geometry (109):
    g0: Circle CenterX=175.022 CenterY=5.37834 CenterZ=0 NormalX=0 NormalY=0 NormalZ=1 AngleXU=0 Radius=1
    g1: Circle CenterX=179.022 CenterY=7.57463 CenterZ=0 NormalX=0 NormalY=0 NormalZ=1 AngleXU=0 Radius=1
    g2: Circle CenterX=179.022 CenterY=5.34704 CenterZ=0 NormalX=0 NormalY=0 NormalZ=1 AngleXU=0 Radius=1
    g3: BSplineCurve PolesCount=3 KnotsCount=2 Degree=2 IsPeriodic=0
    g4: GeomPoint X=175.022 Y=5.37834 Z=0
    g5: GeomPoint X=179.022 Y=5.34704 Z=0
    g6: Circle CenterX=189.124 CenterY=5.37834 CenterZ=0 NormalX=0 NormalY=0 NormalZ=1 AngleXU=0 Radius=1
    g7: Circle CenterX=185.124 CenterY=7.57463 CenterZ=0 NormalX=0 NormalY=0 NormalZ=1 AngleXU=0 Radius=1
    g8: Circle CenterX=185.124 CenterY=5.34704 CenterZ=0 NormalX=0 NormalY=0 NormalZ=1 AngleXU=0 Radius=1
    g9: BSplineCurve PolesCount=3 KnotsCount=2 Degree=2 IsPeriodic=0
    g10: GeomPoint X=189.124 Y=5.37834 Z=0
    g11: GeomPoint X=185.124 Y=5.34704 Z=0
    g12: Circle CenterX=224.513 CenterY=-14.0532 CenterZ=0 NormalX=0 NormalY=0 NormalZ=1 AngleXU=0 Radius=1
    g13: Circle CenterX=236.584 CenterY=-24.2775 CenterZ=0 NormalX=0 NormalY=0 NormalZ=1 AngleXU=0 Radius=1
    g14: BSplineCurve PolesCount=3 KnotsCount=2 Degree=2 IsPeriodic=0
    g15: GeomPoint X=236.584 Y=-24.2775 Z=0
    g16: Circle CenterX=125.607 CenterY=-21.7539 CenterZ=0 NormalX=0 NormalY=0 NormalZ=1 AngleXU=0 Radius=1
    g17: Circle CenterX=139.632 CenterY=-14.0532 CenterZ=0 NormalX=0 NormalY=0 NormalZ=1 AngleXU=0 Radius=1
    g18: Circle CenterX=127.325 CenterY=-24.2775 CenterZ=0 NormalX=0 NormalY=0 NormalZ=1 AngleXU=0 Radius=1
    g19: BSplineCurve PolesCount=3 KnotsCount=2 Degree=2 IsPeriodic=0
    g20: GeomPoint X=125.607 Y=-21.7539 Z=0
    g21: GeomPoint X=127.325 Y=-24.2775 Z=0
    g22: Circle CenterX=179.022 CenterY=-85.8163 CenterZ=0 NormalX=0 NormalY=0 NormalZ=1 AngleXU=0 Radius=1
    g23: Circle CenterX=179.022 CenterY=-91.7794 CenterZ=0 NormalX=0 NormalY=0 NormalZ=1 AngleXU=0 Radius=1
    g24: Circle CenterX=171.895 CenterY=-91.8014 CenterZ=0 NormalX=0 NormalY=0 NormalZ=1 AngleXU=0 Radius=1
    g25: BSplineCurve PolesCount=3 KnotsCount=2 Degree=2 IsPeriodic=0
    g26: GeomPoint X=179.022 Y=-85.8163 Z=0
    g27: GeomPoint X=171.895 Y=-91.8014 Z=0
    g28: Circle CenterX=185.124 CenterY=-86.2028 CenterZ=0 NormalX=0 NormalY=0 NormalZ=1 AngleXU=0 Radius=1
    g29: Circle CenterX=185.124 CenterY=-91.7794 CenterZ=0 NormalX=0 NormalY=0 NormalZ=1 AngleXU=0 Radius=1
    g30: Circle CenterX=191.747 CenterY=-91.7794 CenterZ=0 NormalX=0 NormalY=0 NormalZ=1 AngleXU=0 Radius=1
    g31: BSplineCurve PolesCount=3 KnotsCount=2 Degree=2 IsPeriodic=0
    g32: GeomPoint X=185.124 Y=-86.2028 Z=0
    g33: GeomPoint X=191.747 Y=-91.7794 Z=0
    g34: BSplineCurve PolesCount=5 KnotsCount=3 Degree=3 IsPeriodic=0
    g35: LineSegment StartX=132.072 StartY=-100.779 StartZ=0 EndX=132.072 EndY=-103.779 EndZ=0
    g36: GeomPoint X=232.072 Y=-94.7794 Z=0
    g37: GeomPoint X=223.072 Y=-97.7794 Z=0
    g38: Circle CenterX=232.072 CenterY=-94.7794 CenterZ=0 NormalX=0 NormalY=0 NormalZ=1 AngleXU=0 Radius=1
    g39: Circle CenterX=232.072 CenterY=-100.779 CenterZ=0 NormalX=0 NormalY=0 NormalZ=1 AngleXU=0 Radius=1
    g40: BSplineCurve PolesCount=5 KnotsCount=3 Degree=3 IsPeriodic=0
    g41: GeomPoint X=232.072 Y=-100.779 Z=0
    g42: LineSegment StartX=123.656 StartY=-37.1092 StartZ=0 EndX=122.136 EndY=-35.2714 EndZ=0
    g43: LineSegment StartX=117.05 StartY=-39.4781 StartZ=0 EndX=115.291 EndY=-37.3514 EndZ=0
    g44: LineSegment StartX=120.377 StartY=-33.1447 StartZ=0 EndX=118.86 EndY=-31.3104 EndZ=0
    g45: ArcOfCircle CenterX=116.562 CenterY=-19.6236 CenterZ=0 NormalX=0 NormalY=0 NormalZ=1 AngleXU=0 Radius=4.24264 StartAngle=1.28753 EndAngle=5.99992
    g46: LineSegment StartX=240.266 StartY=-37.1092 StartZ=0 EndX=189.124 EndY=5.37834 EndZ=0
    g47: LineSegment StartX=191.747 StartY=-91.7794 StartZ=0 EndX=232.072 EndY=-91.7794 EndZ=0
    g48: LineSegment StartX=232.072 StartY=-91.7794 StartZ=0 EndX=232.072 EndY=-94.7794 EndZ=0
    g49: LineSegment StartX=232.072 StartY=-100.779 StartZ=0 EndX=232.072 EndY=-103.779 EndZ=0
    g50: LineSegment StartX=132.072 StartY=-103.779 StartZ=0 EndX=232.072 EndY=-103.779 EndZ=0
    g51: LineSegment StartX=132.072 StartY=-91.8014 StartZ=0 EndX=132.072 EndY=-94.7791 EndZ=0
    g52: LineSegment StartX=132.072 StartY=-91.8014 StartZ=0 EndX=171.895 EndY=-91.8014 EndZ=0
    g53: LineSegment StartX=179.022 StartY=-85.8163 StartZ=0 EndX=179.022 EndY=5.34704 EndZ=0
    g54: LineSegment StartX=175.022 StartY=5.37834 StartZ=0 EndX=123.656 EndY=-37.1092 EndZ=0
    g55: LineSegment StartX=185.124 StartY=5.34704 StartZ=0 EndX=185.124 EndY=-86.2028 EndZ=0
    g56: LineSegment StartX=122.136 StartY=-35.2714 StartZ=0 EndX=117.05 EndY=-39.4781 EndZ=0
    g57: LineSegment StartX=115.291 StartY=-37.3514 StartZ=0 EndX=120.377 EndY=-33.1447 EndZ=0
    g58: LineSegment StartX=118.86 StartY=-31.3104 StartZ=0 EndX=127.325 EndY=-24.2775 EndZ=0
    g59: LineSegment StartX=125.607 StartY=-21.7539 StartZ=0 EndX=124.815 EndY=-22.1887 EndZ=0
    g60: LineSegment StartX=123.265 StartY=-19.3655 StartZ=0 EndX=124.815 EndY=-22.1887 EndZ=0
    g61: LineSegment StartX=120.636 StartY=-20.8094 StartZ=0 EndX=123.265 EndY=-19.3655 EndZ=0
    g62: LineSegment StartX=117.748 StartY=-15.55 StartZ=0 EndX=120.377 EndY=-14.1062 EndZ=0
    g63: LineSegment StartX=120.377 StartY=-14.1062 StartZ=0 EndX=118.934 EndY=-11.4765 EndZ=0
    g64: LineSegment StartX=236.584 StartY=-24.2775 StartZ=0 EndX=245.072 EndY=-31.3037 EndZ=0
    g65: LineSegment StartX=245.072 StartY=-31.3037 StartZ=0 EndX=243.535 EndY=-33.1602 EndZ=0
    g66: LineSegment StartX=243.535 StartY=-33.1602 StartZ=0 EndX=248.619 EndY=-37.3688 EndZ=0
    g67: LineSegment StartX=248.619 StartY=-37.3688 StartZ=0 EndX=246.855 EndY=-39.5064 EndZ=0
    g68: LineSegment StartX=246.855 StartY=-39.5064 StartZ=0 EndX=241.778 EndY=-35.2889 EndZ=0
    g69: LineSegment StartX=241.778 StartY=-35.2889 StartZ=0 EndX=240.266 EndY=-37.1092 EndZ=0
    g70: LineSegment StartX=243.628 StartY=-14.0323 StartZ=0 EndX=246.258 EndY=-15.476 EndZ=0
    g71: LineSegment StartX=240.741 StartY=-19.2917 StartZ=0 EndX=243.37 EndY=-20.7355 EndZ=0
    g72: ArcOfCircle CenterX=247.444 CenterY=-19.5496 CenterZ=0 NormalX=0 NormalY=0 NormalZ=1 AngleXU=0 Radius=4.24264 StartAngle=3.4249 EndAngle=8.13729
    g73: LineSegment StartX=240.741 StartY=-19.2917 StartZ=0 EndX=239.201 EndY=-22.0968 EndZ=0
    g74: LineSegment StartX=238.538 StartY=-21.7516 StartZ=0 EndX=239.201 EndY=-22.0968 EndZ=0
    g75: LineSegment StartX=245.072 StartY=-11.4025 StartZ=0 EndX=243.628 EndY=-14.0323 EndZ=0
    g76-g91: Circle x16 (B-spline internal-alignment scaffolding for g92; pole/knot coordinates omitted)
    g92: BSplineCurve PolesCount=16 KnotsCount=14 Degree=3 IsPeriodic=0
    g93-g106: GeomPoint x14 (B-spline internal-alignment scaffolding for g92; pole/knot coordinates omitted)
    g107: LineSegment StartX=165.871 StartY=14.2956 StartZ=0 EndX=118.934 EndY=-11.4765 EndZ=0
    g108: LineSegment StartX=198.264 StartY=14.2963 StartZ=0 EndX=245.072 EndY=-11.4025 EndZ=0
  constraints (146):
    c: Weight(g0) = 1
    c: Equal(g0,g1)
    c: Equal(g0,g2)
    c: InternalAlignment(g0,g3)
    c: InternalAlignment(g1,g3)
    c: InternalAlignment(g2,g3)
    c: InternalAlignment(g4,g3)
    c: InternalAlignment(g5,g3)
    c: Weight(g6) = 1
    c: Equal(g6,g7)
    c: Equal(g6,g8)
    c: InternalAlignment(g6,g9)
    c: InternalAlignment(g7,g9)
    c: InternalAlignment(g8,g9)
    c: InternalAlignment(g10,g9)
    c: InternalAlignment(g11,g9)
    c: Block(g9)
    c: Block(g3)
    c: InternalAlignment(g12,g14)
    c: InternalAlignment(g13,g14)
    c: InternalAlignment(g15,g14)
    c: Block(g14)
    c: Weight(g16) = 1
    c: Equal(g16,g17)
    c: Equal(g16,g18)
    c: InternalAlignment(g16,g19)
    c: InternalAlignment(g17,g19)
    c: InternalAlignment(g18,g19)
    c: InternalAlignment(g20,g19)
    c: InternalAlignment(g21,g19)
    c: Block(g19)
    c: Weight(g22) = 1
    c: Equal(g22,g23)
    c: Equal(g22,g24)
    c: InternalAlignment(g22,g25)
    c: InternalAlignment(g23,g25)
    c: InternalAlignment(g24,g25)
    c: InternalAlignment(g26,g25)
    c: InternalAlignment(g27,g25)
    c: Weight(g28) = 1
    c: Equal(g28,g29)
    c: Equal(g28,g30)
    c: InternalAlignment(g28,g31)
    c: InternalAlignment(g29,g31)
    c: InternalAlignment(g30,g31)
    c: InternalAlignment(g32,g31)
    c: InternalAlignment(g33,g31)
    c: Block(g31)
    c: Block(g25)
    c: Block(g34)
    c: Coincident(g35,g34)
    c: Vertical(g35)
    c: Block(g35)
    c: Equal(g38,g39)
    c: InternalAlignment(g38,g40)
    c: InternalAlignment(g39,g40)
    c: InternalAlignment(g36,g40)
    c: InternalAlignment(g37,g40)
    c: InternalAlignment(g41,g40)
    c: Block(g40)
    c: Distance(g42) = 2.385
    c: Distance(g43) = 2.76
    c: Parallel(g42,g44)
    c: Block(g45)
    c: Coincident(g46,g9)
    c: Coincident(g47,g31)
    c: Horizontal(g47)
    c: Block(g47)
    c: Coincident(g48,g47)
    c: Coincident(g48,g40)
    c: Vertical(g48)
    c: Block(g48)
    c: Coincident(g49,g40)
    c: Vertical(g49)
    c: Block(g49)
    c: Coincident(g50,g35)
    c: Coincident(g50,g49)
    c: Horizontal(g50)
    c: Block(g50)
    c: Coincident(g51,g34)
    c: Vertical(g51)
    c: Coincident(g52,g51)
    c: Coincident(g52,g25)
    c: Horizontal(g52)
    c: Coincident(g53,g25)
    c: Coincident(g53,g3)
    c: Vertical(g53)
    c: Coincident(g54,g3)
    c: Coincident(g54,g42)
    c: Coincident(g55,g9)
    c: Coincident(g55,g31)
    c: Vertical(g55)
    c: Block(g42)
    c: Coincident(g56,g42)
    c: Coincident(g56,g43)
    c: Coincident(g57,g43)
    c: Coincident(g57,g44)
    c: Block(g57)
    c: Block(g56)
    c: Coincident(g58,g44)
    c: Coincident(g58,g19)
    c: Block(g58)
    c: Coincident(g59,g19)
    c: Block(g59)
    c: Coincident(g60,g59)
    c: Block(g60)
    c: Coincident(g61,g45)
    c: Coincident(g61,g60)
    c: Coincident(g62,g45)
    c: Coincident(g63,g62)
    c: Block(g63)
    c: Coincident(g64,g14)
    c: Block(g64)
    c: Coincident(g65,g64)
    c: Coincident(g66,g65)
    c: Coincident(g67,g66)
    c: Coincident(g68,g67)
    c: Coincident(g69,g68)
    c: Coincident(g69,g46)
    c: Block(g46)
    c: Block(g68)
    c: Block(g66)
    c: Distance(g70) = 3
    c: Distance(g71) = 3
    c: Coincident(g72,g70)
    c: Coincident(g72,g71)
    c: Block(g72)
    c: Coincident(g73,g71)
    c: Distance(g73) = 3.2
    c: Coincident(g74,g14)
    c: Coincident(g74,g73)
    c: Coincident(g75,g70)
    c: Block(g75)
    c: Block(g73)
    c: Distance(g63) = 3
    c: Distance(g60) = 3.22077
    c: Weight(g76) = 1
    c: Equal(g76, g77-g91) x15
    c: InternalAlignment(g76-g91 -> g92) x16
    c: InternalAlignment(g93-g106 -> g92) x14
    c: Coincident(g107,g92)
    c: Coincident(g107,g63)
    c: Block(g107)
    c: Block(g92)
    c: Coincident(g108,g92)
    c: Coincident(g108,g75)
FEATURE [Sketcher::SketchObject] Sketch010  label="legBottomBack"
  FullyConstrained = true
  MapMode = 4
  Placement = pos=(0,0,0) rot=(0.57735,0.57735,0.57735;2.0944rad)
  sketch-geometry (76):
    g0: Circle CenterX=-17.0256 CenterY=-190.268 CenterZ=0 NormalX=0 NormalY=0 NormalZ=1 AngleXU=0 Radius=10.5072
    g1: Circle CenterX=-37.7758 CenterY=-187.672 CenterZ=0 NormalX=0 NormalY=0 NormalZ=1 AngleXU=0 Radius=5.64388
    g2: Circle CenterX=-51.4606 CenterY=-185.091 CenterZ=0 NormalX=0 NormalY=0 NormalZ=1 AngleXU=0 Radius=3.01653
    g3: Circle CenterX=-60.4835 CenterY=-182.688 CenterZ=0 NormalX=0 NormalY=0 NormalZ=1 AngleXU=0 Radius=2.12826
    g4: Circle CenterX=-3.29005 CenterY=-177.662 CenterZ=0 NormalX=0 NormalY=0 NormalZ=1 AngleXU=0 Radius=3.26661
    g5: ArcOfCircle CenterX=11.0205 CenterY=-198.019 CenterZ=0 NormalX=0 NormalY=0 NormalZ=1 AngleXU=0 Radius=13 StartAngle=2.78068 EndAngle=5.92131
    g6: LineSegment StartX=5.08312 StartY=-176.581 StartZ=0 EndX=-1.14188 EndY=-193.429 EndZ=0
    g7: ArcOfCircle CenterX=17.2475 CenterY=-181.166 CenterZ=0 NormalX=0 NormalY=0 NormalZ=1 AngleXU=0 Radius=13 StartAngle=1.21042 EndAngle=2.78109
    g8: LineSegment StartX=38.8952 StartY=-231.233 StartZ=0 EndX=39.9512 EndY=-228.425 EndZ=0
    g9: ArcOfCircle CenterX=46.9911 CenterY=-209.705 CenterZ=0 NormalX=0 NormalY=0 NormalZ=1 AngleXU=0 Radius=20 StartAngle=2.78766 EndAngle=4.35269
    g10: LineSegment StartX=23.7323 StartY=-126.969 StartZ=0 EndX=17.4091 EndY=-143.817 EndZ=0
    g11: ArcOfCircle CenterX=29.5716 CenterY=-148.408 CenterZ=0 NormalX=0 NormalY=0 NormalZ=1 AngleXU=0 Radius=13 StartAngle=2.78068 EndAngle=4.35262
    g12: ArcOfCircle CenterX=35.8967 CenterY=-131.555 CenterZ=0 NormalX=0 NormalY=0 NormalZ=1 AngleXU=0 Radius=13 StartAngle=1.21584 EndAngle=2.78109
    g13: ArcOfCircle CenterX=48.1805 CenterY=-98.7782 CenterZ=0 NormalX=0 NormalY=0 NormalZ=1 AngleXU=0 Radius=13 StartAngle=2.78068 EndAngle=4.35005
    g14: LineSegment StartX=42.354 StartY=-77.3391 StartZ=0 EndX=36.018 EndY=-94.1875 EndZ=0
    g15: ArcOfCircle CenterX=54.5183 CenterY=-81.9247 CenterZ=0 NormalX=0 NormalY=0 NormalZ=1 AngleXU=0 Radius=13 StartAngle=2.42113 EndAngle=2.78109
    g16: ArcOfCircle CenterX=20.184 CenterY=-217.506 CenterZ=0 NormalX=0 NormalY=0 NormalZ=1 AngleXU=0 Radius=3.81084 StartAngle=1.88136 EndAngle=6.80465
    g17: LineSegment StartX=38.4753 StartY=-115.966 StartZ=0 EndX=41.2852 EndY=-117.017 EndZ=0
    g18: ArcOfCircle CenterX=36.3663 CenterY=-113.042 CenterZ=0 NormalX=0 NormalY=0 NormalZ=1 AngleXU=0 Radius=3.60555 StartAngle=0.230024 EndAngle=5.3372
    g19: LineSegment StartX=39.8769 StartY=-112.22 StartZ=0 EndX=42.6867 EndY=-113.271 EndZ=0
    g20: LineSegment StartX=19.9036 StartY=-165.61 StartZ=0 EndX=22.7134 EndY=-166.661 EndZ=0
    g21: ArcOfCircle CenterX=17.7945 CenterY=-162.686 CenterZ=0 NormalX=0 NormalY=0 NormalZ=1 AngleXU=0 Radius=3.60555 StartAngle=0.230024 EndAngle=5.3372
    g22: LineSegment StartX=21.3051 StartY=-161.864 StartZ=0 EndX=24.1149 EndY=-162.915 EndZ=0
    g23: LineSegment StartX=41.085 StartY=-66.3176 StartZ=0 EndX=46.0385 EndY=-62.5254 EndZ=0
    g24: LineSegment StartX=48.9563 StartY=-66.3367 StartZ=0 EndX=44.7488 EndY=-73.3482 EndZ=0
    g25: ArcOfCircle CenterX=49.8795 CenterY=-62.6074 CenterZ=0 NormalX=0 NormalY=0 NormalZ=1 AngleXU=0 Radius=3.84187 StartAngle=4.46973 EndAngle=9.40343
    g26: LineSegment StartX=43.5724 StartY=-110.934 StartZ=0 EndX=42.6867 EndY=-113.271 EndZ=0
    g27: LineSegment StartX=40.4148 StartY=-119.365 StartZ=0 EndX=41.2852 EndY=-117.017 EndZ=0
    g28: LineSegment StartX=21.8316 StartY=-169.001 StartZ=0 EndX=22.7134 EndY=-166.661 EndZ=0
    g29: LineSegment StartX=24.9948 StartY=-160.575 StartZ=0 EndX=24.1149 EndY=-162.915 EndZ=0
    g30: LineSegment StartX=23.1786 StartY=-202.622 StartZ=0 EndX=19.0195 EndY=-213.878 EndZ=0
    g31: LineSegment StartX=28.2308 StartY=-202.773 StartZ=0 EndX=23.4884 EndY=-215.608 EndZ=0
    g32: LineSegment StartX=-76.2249 StartY=-179.393 StartZ=0 EndX=-72.8553 EndY=-180.66 EndZ=0
    g33: ArcOfCircle CenterX=-71.1257 CenterY=-183.448 CenterZ=0 NormalX=0 NormalY=0 NormalZ=1 AngleXU=0 Radius=3.28025 StartAngle=3.43759 EndAngle=8.40938
    g34: LineSegment StartX=-79.0409 StartY=-186.881 StartZ=0 EndX=38.8952 EndY=-231.233 EndZ=0
    g35-g53: Circle x19 (B-spline internal-alignment scaffolding for g54; pole/knot coordinates omitted)
    g54: BSplineCurve PolesCount=19 KnotsCount=17 Degree=3 IsPeriodic=0
    g55-g71: GeomPoint x17 (B-spline internal-alignment scaffolding for g54; pole/knot coordinates omitted)
    g72: LineSegment StartX=-74.2633 StartY=-184.404 StartZ=0 EndX=-77.6329 EndY=-183.137 EndZ=0
    g73: LineSegment StartX=-79.0409 StartY=-186.881 StartZ=0 EndX=-77.6329 EndY=-183.137 EndZ=0
    g74: LineSegment StartX=8.65492 StartY=-152.553 StartZ=0 EndX=41.085 EndY=-66.3176 EndZ=0
    g75: LineSegment StartX=-74.4658 StartY=-174.715 StartZ=0 EndX=-76.2249 EndY=-179.393 EndZ=0
  constraints (76):
    c: Block(g5)
    c: Block(g7)
    c: Block(g0)
    c: Block(g4)
    c: Block(g1)
    c: Block(g2)
    c: Block(g3)
    c: Block(g9)
    c: Coincident(g8,g9)
    c: Block(g8)
    c: Coincident(g6,g7)
    c: Coincident(g6,g5)
    c: Block(g11)
    c: Block(g12)
    c: Coincident(g10,g12)
    c: Coincident(g10,g11)
    c: Block(g13)
    c: Block(g15)
    c: Coincident(g14,g15)
    c: Coincident(g14,g13)
    c: Block(g16)
    c: Block(g18)
    c: Coincident(g19,g18)
    c: Coincident(g17,g18)
    c: Parallel(g19,g17)
    c: Block(g17)
    c: Block(g19)
    c: Block(g21)
    c: Coincident(g22,g21)
    c: Coincident(g20,g21)
    c: Parallel(g22,g20)
    c: Block(g20)
    c: Block(g22)
    c: Block(g23)
    c: Coincident(g25,g23)
    c: Coincident(g25,g24)
    c: Block(g25)
    c: Block(g24)
    c: Coincident(g26,g19)
    c: Block(g26)
    c: Coincident(g27,g17)
    c: Block(g27)
    c: Coincident(g28,g20)
    c: Coincident(g29,g22)
    c: Block(g29)
    c: Block(g28)
    c: Coincident(g30,g5)
    c: Coincident(g30,g16)
    c: Block(g30)
    c: Coincident(g7,g28)
    c: Coincident(g11,g29)
    c: Coincident(g12,g27)
    c: Coincident(g13,g26)
    c: Coincident(g15,g24)
    c: Coincident(g31,g9)
    c: Coincident(g31,g16)
    c: Distance(g32) = 3.6
    c: Block(g32)
    c: Coincident(g33,g32)
    c: Coincident(g34,g8)
    c: Weight(g35) = 1
    c: Equal(g35, g36-g53) x18
    c: InternalAlignment(g35-g53 -> g54) x19
    c: InternalAlignment(g55-g71 -> g54) x17
    c: Block(g33)
    c: Block(g54)
    c: Coincident(g72,g33)
    c: Coincident(g73,g34)
    c: Block(g34)
    c: Parallel(g72,g34)
    c: Perpendicular(g73,g34)
    c: Coincident(g72,g73)
    c: Coincident(g74,g54)
    c: Coincident(g74,g23)
    c: Coincident(g75,g54)
    c: Coincident(g75,g32)
FEATURE [Sketcher::SketchObject] Sketch011  label="legBottomFront"
  FullyConstrained = true
  MapMode = 4
  Placement = pos=(0,0,0) rot=(0.57735,0.57735,0.57735;2.0944rad)
  sketch-geometry (13):
    g0: LineSegment StartX=-199.665 StartY=-138.314 StartZ=0 EndX=-200.721 EndY=-141.122 EndZ=0
    g1: LineSegment StartX=-200.721 StartY=-141.122 StartZ=0 EndX=-79.0409 EndY=-186.881 EndZ=0
    g2: ArcOfCircle CenterX=-71.1257 CenterY=-183.448 CenterZ=0 NormalX=0 NormalY=0 NormalZ=1 AngleXU=0 Radius=3.28025 StartAngle=3.43759 EndAngle=8.40938
    g3: LineSegment StartX=-74.4626 StartY=-174.707 StartZ=0 EndX=-76.2249 EndY=-179.393 EndZ=0
    g4: LineSegment StartX=-76.2249 StartY=-179.393 StartZ=0 EndX=-72.8553 EndY=-180.66 EndZ=0
    g5: Circle CenterX=-74.4626 CenterY=-174.707 CenterZ=0 NormalX=0 NormalY=0 NormalZ=1 AngleXU=0 Radius=1
    g6: Circle CenterX=-130.185 CenterY=-164.454 CenterZ=0 NormalX=0 NormalY=0 NormalZ=1 AngleXU=0 Radius=1
    g7: Circle CenterX=-199.665 CenterY=-138.314 CenterZ=0 NormalX=0 NormalY=0 NormalZ=1 AngleXU=0 Radius=1
    g8: BSplineCurve PolesCount=3 KnotsCount=2 Degree=2 IsPeriodic=0
    g9: GeomPoint X=-74.4626 Y=-174.707 Z=0
    g10: GeomPoint X=-199.665 Y=-138.314 Z=0
    g11: LineSegment StartX=-77.6329 StartY=-183.137 StartZ=0 EndX=-79.0409 EndY=-186.881 EndZ=0
    g12: LineSegment StartX=-77.6329 StartY=-183.137 StartZ=0 EndX=-74.2633 EndY=-184.404 EndZ=0
  constraints (24):
    c: Coincident(g1,g0)
    c: Block(g0)
    c: Perpendicular(g1,g0)
    c: Distance(g1) = 130
    c: Coincident(g4,g3)
    c: Coincident(g4,g2)
    c: Block(g2)
    c: Block(g4)
    c: Coincident(g8,g3)
    c: Weight(g5) = 1
    c: Equal(g5,g6)
    c: Equal(g5,g7)
    c: Coincident(g8,g0)
    c: InternalAlignment(g5,g8)
    c: InternalAlignment(g6,g8)
    c: InternalAlignment(g7,g8)
    c: InternalAlignment(g9,g8)
    c: InternalAlignment(g10,g8)
    c: Block(g8)
    c: Block(g3)
    c: Coincident(g11,g1)
    c: Coincident(g12,g11)
    c: Coincident(g12,g2)
    c: Block(g12)
FEATURE [Sketcher::SketchObject] Sketch
  FullyConstrained = true
  Placement = pos=(0,0,0) rot=(-1,0,0;4.71239rad)
  sketch-geometry (13):
    g0: LineSegment StartX=19.9194 StartY=-5.9387 StartZ=0 EndX=79.9194 EndY=-5.9387 EndZ=0
    g1: LineSegment StartX=19.9194 StartY=-115.939 StartZ=0 EndX=24.9194 EndY=-115.939 EndZ=0
    g2: LineSegment StartX=79.9194 StartY=-5.9387 StartZ=0 EndX=79.9194 EndY=-10.9387 EndZ=0
    g3: Circle CenterX=79.9194 CenterY=-10.9387 CenterZ=0 NormalX=0 NormalY=0 NormalZ=1 AngleXU=0 Radius=1
    g4: Circle CenterX=24.9194 CenterY=-10.9387 CenterZ=0 NormalX=0 NormalY=0 NormalZ=1 AngleXU=0 Radius=1
    g5: Circle CenterX=24.9194 CenterY=-115.939 CenterZ=0 NormalX=0 NormalY=0 NormalZ=1 AngleXU=0 Radius=1
    g6: BSplineCurve PolesCount=3 KnotsCount=2 Degree=2 IsPeriodic=0
    g7: GeomPoint X=79.9194 Y=-10.9387 Z=0
    g8: GeomPoint X=24.9194 Y=-115.939 Z=0
    g9: LineSegment StartX=19.9194 StartY=-5.9387 StartZ=0 EndX=19.9194 EndY=-115.939 EndZ=0
    g10: Circle CenterX=33.6194 CenterY=-19.6387 CenterZ=0 NormalX=0 NormalY=0 NormalZ=1 AngleXU=0 Radius=8.7
    g11: LineSegment StartX=33.6194 StartY=-19.6387 StartZ=0 EndX=33.6194 EndY=-10.9387 EndZ=0
    g12: Circle CenterX=28.8194 CenterY=-36.6387 CenterZ=0 NormalX=0 NormalY=0 NormalZ=1 AngleXU=0 Radius=3.9
  constraints (28):
    c: Horizontal(g0)
    c: Distance(g0) = 60
    c: Horizontal(g1)
    c: Distance(g1) = 5
    c: Coincident(g2,g0)
    c: Vertical(g2)
    c: Distance(g2) = 5
    c: Coincident(g6,g2)
    c: Weight(g3) = 1
    c: Equal(g3,g4)
    c: Equal(g3,g5)
    c: Coincident(g6,g1)
    c: InternalAlignment(g3,g6)
    c: InternalAlignment(g4,g6)
    c: InternalAlignment(g5,g6)
    c: InternalAlignment(g7,g6)
    c: InternalAlignment(g8,g6)
    c: Coincident(g9,g0)
    c: Coincident(g9,g1)
    c: Vertical(g9)
    c: Block(g4)
    c: Block(g10)
    c: Block(g6)
    c: Coincident(g11,g10)
    c: Vertical(g11)
    c: PointOnObject(g11,g10)
    c: Block(g0)
    c: Block(g12)
